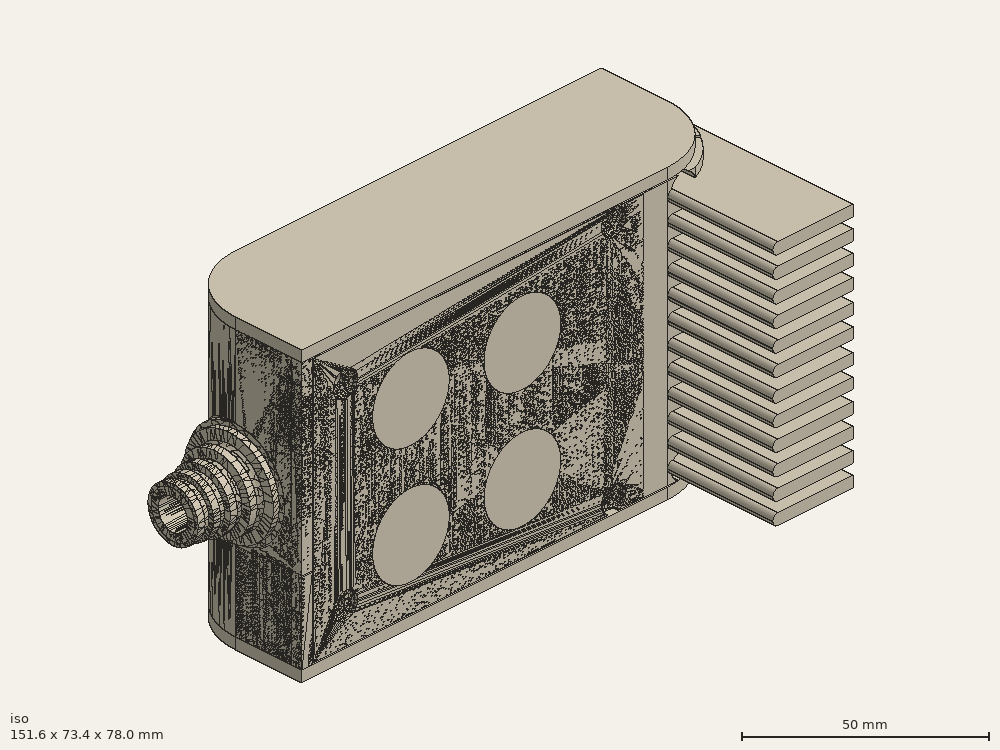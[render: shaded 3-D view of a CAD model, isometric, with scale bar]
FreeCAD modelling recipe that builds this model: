
FCSTD DOCUMENT  (FreeCAD 0.19R0.19.2)
Label: enclosure_1645FCStd
License: All rights reserved
LicenseURL: http://en.wikipedia.org/wiki/All_rights_reserved
objects: Part::Feature×140, Part::Revolution×140, Part::MultiFuse×124, Sketcher::SketchObject×70, Part::Extrusion×55, Part::Cut×53, Part::Cylinder×52, Part::Fillet×51, Part::Box×33, App::MeasureDistance×4
note: 718 computed .brp shape members not serialized (recipe doc carries the construction recipe); baked Part::Feature solids carry a one-line shape summary decoded from their .brp

FEATURE [Sketcher::SketchObject] Sketch  label="topSketch"
  FullyConstrained = true
  sketch-geometry (20):
    g0: LineSegment StartX=5.21097e-06 StartY=3 StartZ=0 EndX=5.21097e-06 EndY=19 EndZ=0
    g1: ArcOfCircle CenterX=19 CenterY=19 CenterZ=0 NormalX=0 NormalY=0 NormalZ=1 AngleXU=0 Radius=19 StartAngle=1.5708 EndAngle=3.14159
    g2: ArcOfCircle CenterX=19 CenterY=19 CenterZ=0 NormalX=0 NormalY=0 NormalZ=1 AngleXU=0 Radius=16 StartAngle=1.5708 EndAngle=3.14159
    g3: LineSegment StartX=114 StartY=35 StartZ=0 EndX=19 EndY=35 EndZ=0
    g4: LineSegment StartX=5.21097e-06 StartY=3 StartZ=0 EndX=5.21097e-06 EndY=0 EndZ=0
    g5: LineSegment StartX=3 StartY=0 StartZ=0 EndX=5.21097e-06 EndY=0 EndZ=0
    g6: LineSegment StartX=3 StartY=19 StartZ=0 EndX=3 EndY=0 EndZ=0
    g7: LineSegment StartX=19 StartY=38 StartZ=0 EndX=124 EndY=38 EndZ=0
    g8: Circle CenterX=119 CenterY=35 CenterZ=0 NormalX=0 NormalY=0 NormalZ=1 AngleXU=0 Radius=1
    g9: Circle CenterX=121 CenterY=35 CenterZ=0 NormalX=0 NormalY=0 NormalZ=1 AngleXU=0 Radius=1
    g10: Circle CenterX=121 CenterY=33 CenterZ=0 NormalX=0 NormalY=0 NormalZ=1 AngleXU=0 Radius=1
    g11: BSplineCurve PolesCount=3 KnotsCount=2 Degree=2 IsPeriodic=0
    g12: GeomPoint X=119 Y=35 Z=0
    g13: GeomPoint X=121 Y=33 Z=0
    g14: LineSegment StartX=119 StartY=35 StartZ=0 EndX=114 EndY=35 EndZ=0
    g15: ArcOfCircle CenterX=105 CenterY=19 CenterZ=0 NormalX=0 NormalY=0 NormalZ=1 AngleXU=0 Radius=19 StartAngle=5.7297 EndAngle=6.28319
    g16: ArcOfCircle CenterX=105 CenterY=19 CenterZ=0 NormalX=0 NormalY=0 NormalZ=1 AngleXU=0 Radius=16 StartAngle=5.60905 EndAngle=6.28319
    g17: LineSegment StartX=121 StartY=33 StartZ=0 EndX=121 EndY=19 EndZ=0
    g18: LineSegment StartX=124 StartY=38 StartZ=0 EndX=124 EndY=19 EndZ=0
    g19: LineSegment StartX=117.5 StartY=9.01251 StartZ=0 EndX=121.163 EndY=9.0125 EndZ=0
  constraints (46):
    c: Vertical(g0)
    c: Block(g0)
    c: Coincident(g1,g0)
    c: Block(g1)
    c: Coincident(g2,g1)
    c: Block(g2)
    c: Coincident(g3,g2)
    c: Horizontal(g3)
    c: Tangent(g3,g2)
    c: Coincident(g4,g0)
    c: Distance(g4) = 3
    c: Vertical(g4)
    c: Coincident(g5,g4)
    c: Horizontal(g5)
    c: Coincident(g6,g2)
    c: Coincident(g6,g5)
    c: Vertical(g6)
    c: Horizontal(g7)
    c: Distance(g7) = 105
    c: Coincident(g7,g1)
    c: Block(g3)
    c: Weight(g8) = 1
    c: Equal(g8,g9)
    c: Equal(g8,g10)
    c: InternalAlignment(g8,g11)
    c: InternalAlignment(g9,g11)
    c: InternalAlignment(g10,g11)
    c: InternalAlignment(g12,g11)
    c: InternalAlignment(g13,g11)
    c: Block(g11)
    c: Coincident(g14,g11)
    c: Coincident(g14,g3)
    c: Horizontal(g14)
    c: Block(g15)
    c: Coincident(g16,g15)
    c: Block(g16)
    c: Coincident(g17,g11)
    c: Coincident(g17,g16)
    c: Vertical(g17)
    c: Distance(g17) = 14
    c: Coincident(g18,g7)
    c: Coincident(g18,g15)
    c: Vertical(g18)
    c: Distance(g18) = 19
    c: Coincident(g19,g16)
    c: Coincident(g19,g15)
FEATURE [Sketcher::SketchObject] Sketch001  label="bottomSketch"
  FullyConstrained = true
  sketch-geometry (32):
    g0: LineSegment StartX=3.3 StartY=-6.03275e-07 StartZ=0 EndX=98 EndY=-6.03275e-07 EndZ=0
    g1: ArcOfCircle CenterX=98 CenterY=19 CenterZ=0 NormalX=0 NormalY=0 NormalZ=1 AngleXU=0 Radius=19 StartAngle=4.71239 EndAngle=5.71103
    g2: LineSegment StartX=6.3 StartY=8 StartZ=0 EndX=3.3 EndY=8 EndZ=0
    g3: LineSegment StartX=3.3 StartY=8 StartZ=0 EndX=3.3 EndY=-6.03275e-07 EndZ=0
    g4: ArcOfCircle CenterX=8.3 CenterY=5 CenterZ=0 NormalX=0 NormalY=0 NormalZ=1 AngleXU=0 Radius=2 StartAngle=3.14159 EndAngle=4.71239
    g5: LineSegment StartX=6.3 StartY=8 StartZ=0 EndX=6.3 EndY=5 EndZ=0
    g6: ArcOfCircle CenterX=98 CenterY=19 CenterZ=0 NormalX=0 NormalY=0 NormalZ=1 AngleXU=0 Radius=12.7 StartAngle=4.71239 EndAngle=6.28319
    g7: LineSegment StartX=94.7 StartY=3 StartZ=0 EndX=8.3 EndY=3 EndZ=0
    g8-g12: Circle x5 (B-spline internal-alignment scaffolding for g13; pole/knot coordinates omitted)
    g13: BSplineCurve PolesCount=5 KnotsCount=3 Degree=3 IsPeriodic=0
    g14: GeomPoint X=98 Y=6.3 Z=0
    g15: GeomPoint X=96.3938 Y=4.71946 Z=0
    g16: GeomPoint X=94.7 Y=3 Z=0
    g17-g23: Circle x7 (B-spline internal-alignment scaffolding for g24; pole/knot coordinates omitted)
    g24: BSplineCurve PolesCount=7 KnotsCount=5 Degree=3 IsPeriodic=0
    g25-g29: GeomPoint x5 (B-spline internal-alignment scaffolding for g24; pole/knot coordinates omitted)
    g30: ArcOfCircle CenterX=98 CenterY=19 CenterZ=0 NormalX=0 NormalY=0 NormalZ=1 AngleXU=0 Radius=15.7 StartAngle=5.81226 EndAngle=6.28319
    g31: LineSegment StartX=110.7 StartY=19 StartZ=0 EndX=113.7 EndY=19 EndZ=0
  constraints (41):
    c: Horizontal(g0)
    c: Coincident(g1,g0)
    c: Block(g1)
    c: Horizontal(g2)
    c: Distance(g2) = 3
    c: Coincident(g3,g2)
    c: Vertical(g3)
    c: Coincident(g3,g0)
    c: Block(g4)
    c: Block(g2)
    c: Coincident(g5,g2)
    c: Coincident(g5,g4)
    c: Vertical(g5)
    c: Coincident(g6,g1)
    c: Block(g6)
    c: Coincident(g7,g4)
    c: Horizontal(g7)
    c: Block(g0)
    c: Block(g7)
    c: Block(g3)
    c: Coincident(g13,g6)
    c: Weight(g8) = 1
    c: Equal(g8, g9-g12) x4
    c: Coincident(g13,g7)
    c: InternalAlignment(g8-g12 -> g13) x5
    c: InternalAlignment(g14,g13)
    c: InternalAlignment(g15,g13)
    c: InternalAlignment(g16,g13)
    c: Block(g13)
    c: Weight(g17) = 1
    c: Equal(g17, g18-g23) x6
    c: Coincident(g24,g1)
    c: InternalAlignment(g17-g23 -> g24) x7
    c: InternalAlignment(g25-g29 -> g24) x5
    c: Block(g24)
    c: Coincident(g30,g24)
    c: Coincident(g31,g6)
    c: Coincident(g31,g30)
    c: Horizontal(g31)
    c: Block(g31)
    c: Block(g30)
FEATURE [Part::Extrusion] Extrude  label="top"
  Base = -> Sketch
  Dir = (0,0,1)
  DirMode = 2
  FaceMakerClass = Part::FaceMakerBullseye
  LengthFwd = 72
  LengthRev = 0
  Solid = true
  Symmetric = false
FEATURE [Part::Extrusion] Extrude001  label="bottom"
  Base = -> Sketch001
  Dir = (0,0,1)
  DirMode = 2
  FaceMakerClass = Part::FaceMakerBullseye
  LengthFwd = 71.4
  LengthRev = 0
  Placement = pos=(0,0,0.3) rot=(0,0,1;0rad)
  Solid = true
  Symmetric = false
FEATURE [Sketcher::SketchObject] Sketch002  label="topSketch001"
  FullyConstrained = true
  sketch-geometry (6):
    g0: ArcOfCircle CenterX=19 CenterY=19 CenterZ=0 NormalX=0 NormalY=0 NormalZ=1 AngleXU=0 Radius=19 StartAngle=1.5708 EndAngle=3.14159
    g1: LineSegment StartX=5.22862e-06 StartY=19 StartZ=0 EndX=5.22862e-06 EndY=1.19904e-11 EndZ=0
    g2: LineSegment StartX=19 StartY=38 StartZ=0 EndX=124 EndY=38 EndZ=0
    g3: LineSegment StartX=5.22862e-06 StartY=1.19904e-11 StartZ=0 EndX=105 EndY=1.19904e-11 EndZ=0
    g4: ArcOfCircle CenterX=105 CenterY=19 CenterZ=0 NormalX=0 NormalY=0 NormalZ=1 AngleXU=0 Radius=19 StartAngle=4.71239 EndAngle=6.28319
    g5: LineSegment StartX=124 StartY=38 StartZ=0 EndX=124 EndY=19 EndZ=0
  constraints (16):
    c: Block(g0)
    c: Coincident(g1,g0)
    c: Vertical(g1)
    c: Horizontal(g2)
    c: Distance(g2) = 105
    c: Coincident(g2,g0)
    c: Distance(g1) = 19
    c: Coincident(g3,g1)
    c: Horizontal(g3)
    c: Distance(g3) = 105
    c: Block(g4)
    c: Coincident(g4,g3)
    c: Coincident(g5,g2)
    c: Coincident(g5,g4)
    c: Vertical(g5)
    c: Distance(g5) = 19
FEATURE [Part::Extrusion] Extrude002  label="sideA"
  Base = -> Sketch002
  Dir = (0,0,1)
  DirMode = 2
  FaceMakerClass = Part::FaceMakerBullseye
  LengthFwd = 3
  LengthRev = 0
  Placement = pos=(0,0,-3) rot=(0,0,1;0rad)
  Solid = true
  Symmetric = false
FEATURE [Sketcher::SketchObject] Sketch003  label="topSketch002"
  FullyConstrained = true
  sketch-geometry (6):
    g0: LineSegment StartX=19 StartY=38 StartZ=0 EndX=117 EndY=38 EndZ=0
    g1: ArcOfCircle CenterX=19 CenterY=19 CenterZ=0 NormalX=0 NormalY=0 NormalZ=1 AngleXU=0 Radius=19 StartAngle=1.5708 EndAngle=3.14159
    g2: LineSegment StartX=117 StartY=38 StartZ=0 EndX=117 EndY=19 EndZ=0
    g3: LineSegment StartX=98 StartY=1.0161e-12 StartZ=0 EndX=5.22862e-06 EndY=1.0161e-12 EndZ=0
    g4: LineSegment StartX=5.22862e-06 StartY=19 StartZ=0 EndX=5.22862e-06 EndY=1.0161e-12 EndZ=0
    g5: ArcOfCircle CenterX=98 CenterY=19 CenterZ=0 NormalX=0 NormalY=0 NormalZ=1 AngleXU=0 Radius=19 StartAngle=4.71239 EndAngle=6.28319
  constraints (16):
    c: Horizontal(g0)
    c: Distance(g0) = 98
    c: Coincident(g1,g0)
    c: Block(g1)
    c: Coincident(g2,g0)
    c: Vertical(g2)
    c: Distance(g2) = 19
    c: Horizontal(g3)
    c: Coincident(g4,g1)
    c: Vertical(g4)
    c: Coincident(g3,g4)
    c: Block(g3)
    c: Coincident(g5,g2)
    c: Coincident(g5,g3)
    c: Block(g0)
    c: Block(g5)
FEATURE [Sketcher::SketchObject] Sketch004
  FullyConstrained = true
  MapMode = 3
  Placement = pos=(0,0,0) rot=(1,0,0;1.5708rad)
  Support = -> [Extrude]
  sketch-geometry (8):
    g0: Circle CenterX=80.351 CenterY=-67.6202 CenterZ=0 NormalX=0 NormalY=0 NormalZ=1 AngleXU=0 Radius=2
    g1: Circle CenterX=80.351 CenterY=-67.6202 CenterZ=0 NormalX=0 NormalY=0 NormalZ=1 AngleXU=0 Radius=3
    g2: Circle CenterX=80.351 CenterY=-4.92017 CenterZ=0 NormalX=0 NormalY=0 NormalZ=1 AngleXU=0 Radius=2
    g3: Circle CenterX=80.351 CenterY=-4.92017 CenterZ=0 NormalX=0 NormalY=0 NormalZ=1 AngleXU=0 Radius=3
    g4: Circle CenterX=23.851 CenterY=-4.92017 CenterZ=0 NormalX=0 NormalY=0 NormalZ=1 AngleXU=0 Radius=2
    g5: Circle CenterX=23.851 CenterY=-4.92017 CenterZ=0 NormalX=0 NormalY=0 NormalZ=1 AngleXU=0 Radius=3
    g6: Circle CenterX=23.851 CenterY=-67.6202 CenterZ=0 NormalX=0 NormalY=0 NormalZ=1 AngleXU=0 Radius=2
    g7: Circle CenterX=23.851 CenterY=-67.6202 CenterZ=0 NormalX=0 NormalY=0 NormalZ=1 AngleXU=0 Radius=3
  constraints (8):
    c: Block(g3)
    c: Block(g2)
    c: Block(g1)
    c: Block(g0)
    c: Block(g6)
    c: Block(g7)
    c: Block(g4)
    c: Block(g5)
FEATURE [Part::Extrusion] Extrude004
  Base = -> Sketch004
  Dir = (0,-1,2e-16)
  DirMode = 2
  FaceMakerClass = Part::FaceMakerBullseye
  LengthFwd = 6
  LengthRev = 0
  Placement = pos=(0,9,0) rot=(0,0,1;0rad)
  Solid = true
  Symmetric = false
FEATURE [Sketcher::SketchObject] Sketch005
  FullyConstrained = true
  MapMode = 3
  Placement = pos=(0,0,0) rot=(1,0,0;1.5708rad)
  Support = -> [Extrude]
  sketch-geometry (8):
    g0: Circle CenterX=80.351 CenterY=-67.6202 CenterZ=0 NormalX=0 NormalY=0 NormalZ=1 AngleXU=0 Radius=3
    g1: Circle CenterX=80.351 CenterY=-4.92017 CenterZ=0 NormalX=0 NormalY=0 NormalZ=1 AngleXU=0 Radius=3
    g2: Circle CenterX=23.851 CenterY=-4.92017 CenterZ=0 NormalX=0 NormalY=0 NormalZ=1 AngleXU=0 Radius=3
    g3: Circle CenterX=23.851 CenterY=-67.6202 CenterZ=0 NormalX=0 NormalY=0 NormalZ=1 AngleXU=0 Radius=3
    g4: Circle CenterX=23.851 CenterY=-67.6202 CenterZ=0 NormalX=0 NormalY=0 NormalZ=1 AngleXU=0 Radius=5
    g5: Circle CenterX=80.351 CenterY=-67.6202 CenterZ=0 NormalX=0 NormalY=0 NormalZ=1 AngleXU=0 Radius=5
    g6: Circle CenterX=23.851 CenterY=-4.92017 CenterZ=0 NormalX=0 NormalY=0 NormalZ=1 AngleXU=0 Radius=5
    g7: Circle CenterX=80.351 CenterY=-4.92017 CenterZ=0 NormalX=0 NormalY=0 NormalZ=1 AngleXU=0 Radius=5
  constraints (8):
    c: Block(g1)
    c: Block(g0)
    c: Block(g3)
    c: Block(g2)
    c: Block(g5)
    c: Block(g4)
    c: Block(g6)
    c: Block(g7)
FEATURE [Part::Extrusion] Extrude005
  Base = -> Sketch005
  Dir = (0,-1,2e-16)
  DirMode = 2
  FaceMakerClass = Part::FaceMakerBullseye
  LengthFwd = 2
  LengthRev = 0
  Solid = true
  Symmetric = false
FEATURE [Sketcher::SketchObject] Sketch006
  FullyConstrained = true
  MapMode = 3
  Placement = pos=(0,0,0) rot=(1,0,0;1.5708rad)
  sketch-geometry (8):
    g0: Circle CenterX=80.351 CenterY=-67.6202 CenterZ=0 NormalX=0 NormalY=0 NormalZ=1 AngleXU=0 Radius=3
    g1: Circle CenterX=80.351 CenterY=-4.92017 CenterZ=0 NormalX=0 NormalY=0 NormalZ=1 AngleXU=0 Radius=3
    g2: Circle CenterX=23.851 CenterY=-4.92017 CenterZ=0 NormalX=0 NormalY=0 NormalZ=1 AngleXU=0 Radius=3
    g3: Circle CenterX=23.851 CenterY=-67.6202 CenterZ=0 NormalX=0 NormalY=0 NormalZ=1 AngleXU=0 Radius=3
    g4: Circle CenterX=23.851 CenterY=-67.6202 CenterZ=0 NormalX=0 NormalY=0 NormalZ=1 AngleXU=0 Radius=5
    g5: Circle CenterX=80.351 CenterY=-67.6202 CenterZ=0 NormalX=0 NormalY=0 NormalZ=1 AngleXU=0 Radius=5
    g6: Circle CenterX=23.851 CenterY=-4.92017 CenterZ=0 NormalX=0 NormalY=0 NormalZ=1 AngleXU=0 Radius=5
    g7: Circle CenterX=80.351 CenterY=-4.92017 CenterZ=0 NormalX=0 NormalY=0 NormalZ=1 AngleXU=0 Radius=5
  constraints (8):
    c: Block(g1)
    c: Block(g0)
    c: Block(g3)
    c: Block(g2)
    c: Block(g5)
    c: Block(g4)
    c: Block(g6)
    c: Block(g7)
FEATURE [Part::Extrusion] Extrude007
  Base = -> Sketch006
  Dir = (0,-1,2e-16)
  DirMode = 2
  FaceMakerClass = Part::FaceMakerBullseye
  LengthFwd = 2
  LengthRev = 0
  Solid = true
  Symmetric = false
FEATURE [Part::Fillet] Fillet
  Base = -> Extrude007
  Edges = 4 edges r=1.99: [Edge6,Edge12,Edge18,Edge24]
FEATURE [Part::Cut] Cut
  Base = -> Extrude005
  Placement = pos=(0,5,0) rot=(0,0,1;0rad)
  Tool = -> Fillet
FEATURE [Part::MultiFuse] Fusion  label="pCBScrews"
  Placement = pos=(-2.5,0,72.3) rot=(0,0,1;0rad)
  Shapes = -> [Extrude004,Cut]
FEATURE [App::MeasureDistance] Distance  label="Distance: 0.69 mm"
  Distance = 0.685967
  P1 = (24.0138,2.9647,0.3)
  P2 = (23.8901,3,-0.373787)
FEATURE [App::MeasureDistance] Distance001  label="Distance: 0.53 mm"
  Distance = 0.533607
  P1 = (80.2939,3,72.2334)
  P2 = (80.281,2.99661,71.7)
FEATURE [Part::Fillet] Fillet001
  Base = -> Extrude001
  Edges = 1 edges r=2.4: [Edge17]
FEATURE [Part::Fillet] Fillet002  label="bottom001"
  Base = -> Fillet001
  Edges = 1 edges r=2.4: [Edge36]
FEATURE [Part::Fillet] Fillet003  label="top001"
  Base = -> Extrude
  Edges = 1 edges r=2: [Edge1]
FEATURE [Sketcher::SketchObject] Sketch007
  FullyConstrained = true
  sketch-geometry (16):
    g0: LineSegment StartX=4 StartY=0 StartZ=0 EndX=4 EndY=2.4 EndZ=0
    g1: LineSegment StartX=4 StartY=2.4 StartZ=0 EndX=7 EndY=2.4 EndZ=0
    g2: LineSegment StartX=4 StartY=0 StartZ=0 EndX=5.7 EndY=0 EndZ=0
    g3: LineSegment StartX=5.7 StartY=0 StartZ=0 EndX=5.7 EndY=-5.6 EndZ=0
    g4-g8: Circle x5 (B-spline internal-alignment scaffolding for g9; pole/knot coordinates omitted)
    g9: BSplineCurve PolesCount=5 KnotsCount=3 Degree=3 IsPeriodic=0
    g10: GeomPoint X=7 Y=2.4 Z=0
    g11: GeomPoint X=10.4582 Y=-1.55472 Z=0
    g12: GeomPoint X=14 Y=-5.6 Z=0
    g13: LineSegment StartX=14 StartY=-5.6 StartZ=0 EndX=14 EndY=-14.1 EndZ=0
    g14: LineSegment StartX=14 StartY=-14.1 StartZ=0 EndX=6.5 EndY=-14.1 EndZ=0
    g15: LineSegment StartX=5.7 StartY=-5.6 StartZ=0 EndX=6.5 EndY=-14.1 EndZ=0
  constraints (28):
    c: Distance(g0) = 2.4
    c: Vertical(g0)
    c: Block(g0)
    c: Coincident(g1,g0)
    c: Horizontal(g1)
    c: Distance(g1) = 3
    c: Coincident(g2,g0)
    c: Horizontal(g2)
    c: Distance(g2) = 1.7
    c: Coincident(g3,g2)
    c: Vertical(g3)
    c: Distance(g3) = 5.6
    c: Coincident(g9,g1)
    c: Weight(g4) = 1
    c: Equal(g4, g5-g8) x4
    c: InternalAlignment(g4-g8 -> g9) x5
    c: InternalAlignment(g10,g9)
    c: InternalAlignment(g11,g9)
    c: InternalAlignment(g12,g9)
    c: Block(g9)
    c: Coincident(g13,g9)
    c: Vertical(g13)
    c: Distance(g13) = 8.5
    c: Coincident(g14,g13)
    c: Horizontal(g14)
    c: Distance(g14) = 7.5
    c: Coincident(g15,g3)
    c: Coincident(g15,g14)
FEATURE [Part::Feature] Face
  shape: bbox 10 x 16.5 x 2e-07 mm, 1 faces, 0 solids (baked)
FEATURE [Part::Revolution] Revolve  label="plugHousing"
  Angle = 360
  Axis = (0,1,0)
  Base = (0,0,0)
  FaceMakerClass = Part::FaceMakerBullseye
  Placement = pos=(0,0,36.15) rot=(0,0,1;0rad)
  Solid = false
  Source = -> Face
  Symmetric = false
FEATURE [Part::Feature] Face001
  shape: bbox 10 x 16.5 x 2e-07 mm, 1 faces, 0 solids (baked)
FEATURE [Part::Revolution] Revolve001  label="plugHousing001"
  Angle = 360
  Axis = (0,1,0)
  Base = (0,0,0)
  FaceMakerClass = Part::FaceMakerBullseye
  Placement = pos=(0,0,36.15) rot=(0,0,1;0rad)
  Solid = false
  Source = -> Face001
  Symmetric = false
FEATURE [Part::MultiFuse] Fusion001  label="plugHousing002"
  Placement = pos=(0,0,0) rot=(0,0,1;1.5708rad)
  Shapes = -> [Revolve001,Revolve]
FEATURE [Part::Feature] Face002
  shape: bbox 10 x 16.5 x 2e-07 mm, 1 faces, 0 solids (baked)
FEATURE [Part::Revolution] Revolve003  label="plugHousing005"
  Angle = 360
  Axis = (0,1,0)
  Base = (0,0,0)
  FaceMakerClass = Part::FaceMakerBullseye
  Placement = pos=(0,0,36.15) rot=(0,0,1;0rad)
  Solid = false
  Source = -> Face002
  Symmetric = false
FEATURE [Part::Feature] Face003
  shape: bbox 10 x 16.5 x 2e-07 mm, 1 faces, 0 solids (baked)
FEATURE [Part::Revolution] Revolve002  label="plugHousing003"
  Angle = 360
  Axis = (0,1,0)
  Base = (0,0,0)
  FaceMakerClass = Part::FaceMakerBullseye
  Placement = pos=(0,0,36.15) rot=(0,0,1;0rad)
  Solid = false
  Source = -> Face003
  Symmetric = false
FEATURE [Part::MultiFuse] Fusion002  label="plugHousing004"
  Placement = pos=(0,0,0) rot=(0,0,1;1.5708rad)
  Shapes = -> [Revolve002,Revolve003]
FEATURE [Part::MultiFuse] Fusion003  label="plugHousing006"
  Placement = pos=(0,19,0) rot=(0,0,1;3.14159rad)
  Shapes = -> [Fusion002,Fusion001]
FEATURE [Part::Feature] Face004
  shape: bbox 10 x 16.5 x 2e-07 mm, 1 faces, 0 solids (baked)
FEATURE [Part::Revolution] Revolve006  label="plugHousing010"
  Angle = 360
  Axis = (0,1,0)
  Base = (0,0,0)
  FaceMakerClass = Part::FaceMakerBullseye
  Placement = pos=(0,0,36.15) rot=(0,0,1;0rad)
  Solid = false
  Source = -> Face004
  Symmetric = false
FEATURE [Part::Feature] Face005
  shape: bbox 10 x 16.5 x 2e-07 mm, 1 faces, 0 solids (baked)
FEATURE [Part::Revolution] Revolve007  label="plugHousing011"
  Angle = 360
  Axis = (0,1,0)
  Base = (0,0,0)
  FaceMakerClass = Part::FaceMakerBullseye
  Placement = pos=(0,0,36.15) rot=(0,0,1;0rad)
  Solid = false
  Source = -> Face005
  Symmetric = false
FEATURE [Part::Feature] Face006
  shape: bbox 10 x 16.5 x 2e-07 mm, 1 faces, 0 solids (baked)
FEATURE [Part::Revolution] Revolve004  label="plugHousing007"
  Angle = 360
  Axis = (0,1,0)
  Base = (0,0,0)
  FaceMakerClass = Part::FaceMakerBullseye
  Placement = pos=(0,0,36.15) rot=(0,0,1;0rad)
  Solid = false
  Source = -> Face006
  Symmetric = false
FEATURE [Part::MultiFuse] Fusion004  label="plugHousing009"
  Placement = pos=(0,0,0) rot=(0,0,1;1.5708rad)
  Shapes = -> [Revolve004,Revolve007]
FEATURE [Part::Feature] Face007
  shape: bbox 10 x 16.5 x 2e-07 mm, 1 faces, 0 solids (baked)
FEATURE [Part::Revolution] Revolve005  label="plugHousing008"
  Angle = 360
  Axis = (0,1,0)
  Base = (0,0,0)
  FaceMakerClass = Part::FaceMakerBullseye
  Placement = pos=(0,0,36.15) rot=(0,0,1;0rad)
  Solid = false
  Source = -> Face007
  Symmetric = false
FEATURE [Part::MultiFuse] Fusion005  label="plugHousing012"
  Placement = pos=(0,0,0) rot=(0,0,1;1.5708rad)
  Shapes = -> [Revolve006,Revolve005]
FEATURE [Part::MultiFuse] Fusion006  label="plugHousing013"
  Placement = pos=(0,19,0) rot=(0,0,1;3.14159rad)
  Shapes = -> [Fusion005,Fusion004]
FEATURE [Part::MultiFuse] Fusion007  label="plugHousing014"
  Placement = pos=(122.621,0,-0.15) rot=(0,0,1;0rad)
  Shapes = -> [Fusion003,Fusion006]
FEATURE [Part::Cylinder] Cylinder002
  Angle = 360
  AttacherType = Attacher::AttachEngine3D
  Height = 20
  Placement = pos=(0,0,36.15) rot=(0,0,1;0rad)
  Radius = 4
FEATURE [Part::Cylinder] Cylinder003
  Angle = 360
  AttacherType = Attacher::AttachEngine3D
  Height = 10
  Placement = pos=(0,0,36.15) rot=(0,0,1;0rad)
  Radius = 4
FEATURE [Part::MultiFuse] Fusion009  label="removeToCreateHoleForPlugHousing"
  Placement = pos=(70,19,36.15) rot=(0,1,0;1.5708rad)
  Shapes = -> [Cylinder002,Cylinder003]
FEATURE [Part::Cylinder] Cylinder004
  Angle = 360
  AttacherType = Attacher::AttachEngine3D
  Height = 20
  Placement = pos=(0,0,36.15) rot=(0,0,1;0rad)
  Radius = 4
FEATURE [Part::Cylinder] Cylinder005
  Angle = 360
  AttacherType = Attacher::AttachEngine3D
  Height = 10
  Placement = pos=(0,0,36.15) rot=(0,0,1;0rad)
  Radius = 4
FEATURE [Part::MultiFuse] Fusion010  label="removeToCreateHoleForPlugHousing001"
  Placement = pos=(70,19,36.15) rot=(0,1,0;1.5708rad)
  Shapes = -> [Cylinder004,Cylinder005]
FEATURE [Part::Cut] Cut001
  Base = -> Fillet003
  Tool = -> Fusion010
FEATURE [Part::Cut] Cut002  label="Bottom"
  Base = -> Fillet002
  Tool = -> Fusion009
FEATURE [Part::Feature] Face008
  shape: bbox 10 x 16.5 x 2e-07 mm, 1 faces, 0 solids (baked)
FEATURE [Part::Revolution] Revolve011  label="plugHousing021"
  Angle = 360
  Axis = (0,1,0)
  Base = (0,0,0)
  FaceMakerClass = Part::FaceMakerBullseye
  Placement = pos=(0,0,36.15) rot=(0,0,1;0rad)
  Solid = false
  Source = -> Face008
  Symmetric = false
FEATURE [Part::Feature] Face009
  shape: bbox 10 x 16.5 x 2e-07 mm, 1 faces, 0 solids (baked)
FEATURE [Part::Revolution] Revolve012  label="plugHousing022"
  Angle = 360
  Axis = (0,1,0)
  Base = (0,0,0)
  FaceMakerClass = Part::FaceMakerBullseye
  Placement = pos=(0,0,36.15) rot=(0,0,1;0rad)
  Solid = false
  Source = -> Face009
  Symmetric = false
FEATURE [Part::Feature] Face010 .. Face013  x4 (patterned run collapsed; names and placements below)
  shape: bbox 10 x 16.5 x 2e-07 mm, 1 faces, 0 solids (baked)
FEATURE [Part::Revolution] Revolve015  label="plugHousing027"
  Angle = 360
  Axis = (0,1,0)
  Base = (0,0,0)
  FaceMakerClass = Part::FaceMakerBullseye
  Placement = pos=(0,0,36.15) rot=(0,0,1;0rad)
  Solid = false
  Source = -> Face013
  Symmetric = false
FEATURE [Part::Feature] Face014
  shape: bbox 10 x 16.5 x 2e-07 mm, 1 faces, 0 solids (baked)
FEATURE [Part::Feature] Face015
  shape: bbox 10 x 16.5 x 2e-07 mm, 1 faces, 0 solids (baked)
FEATURE [Part::Feature] Face016
  shape: bbox 10 x 16.5 x 2e-07 mm, 1 faces, 0 solids (baked)
FEATURE [Part::Revolution] Revolve019  label="plugHousing033"
  Angle = 360
  Axis = (0,1,0)
  Base = (0,0,0)
  FaceMakerClass = Part::FaceMakerBullseye
  Placement = pos=(0,0,36.15) rot=(0,0,1;0rad)
  Solid = false
  Source = -> Face016
  Symmetric = false
FEATURE [Part::Feature] Face017
  shape: bbox 10 x 16.5 x 2e-07 mm, 1 faces, 0 solids (baked)
FEATURE [Part::Revolution] Revolve020  label="plugHousing034"
  Angle = 360
  Axis = (0,1,0)
  Base = (0,0,0)
  FaceMakerClass = Part::FaceMakerBullseye
  Placement = pos=(0,0,36.15) rot=(0,0,1;0rad)
  Solid = false
  Source = -> Face017
  Symmetric = false
FEATURE [Part::Feature] Face018
  shape: bbox 10 x 16.5 x 2e-07 mm, 1 faces, 0 solids (baked)
FEATURE [Part::Revolution] Revolve016  label="plugHousing030"
  Angle = 360
  Axis = (0,1,0)
  Base = (0,0,0)
  FaceMakerClass = Part::FaceMakerBullseye
  Placement = pos=(0,0,36.15) rot=(0,0,1;0rad)
  Solid = false
  Source = -> Face018
  Symmetric = false
FEATURE [Part::MultiFuse] Fusion020  label="plugHousing038"
  Placement = pos=(0,0,0) rot=(0,0,1;1.5708rad)
  Shapes = -> [Revolve016,Revolve020]
FEATURE [Part::Feature] Face019
  shape: bbox 10 x 16.5 x 2e-07 mm, 1 faces, 0 solids (baked)
FEATURE [Part::Feature] Face020
  shape: bbox 10 x 16.5 x 2e-07 mm, 1 faces, 0 solids (baked)
FEATURE [Part::Revolution] Revolve017  label="plugHousing031"
  Angle = 360
  Axis = (0,1,0)
  Base = (0,0,0)
  FaceMakerClass = Part::FaceMakerBullseye
  Placement = pos=(0,0,36.15) rot=(0,0,1;0rad)
  Solid = false
  Source = -> Face020
  Symmetric = false
FEATURE [Part::MultiFuse] Fusion021  label="plugHousing039"
  Placement = pos=(0,0,0) rot=(0,0,1;1.5708rad)
  Shapes = -> [Revolve019,Revolve017]
FEATURE [Part::MultiFuse] Fusion023  label="plugHousing041"
  Placement = pos=(0,19,0) rot=(0,0,1;3.14159rad)
  Shapes = -> [Fusion021,Fusion020]
FEATURE [Part::Revolution] Revolve022  label="plugHousing043"
  Angle = 360
  Axis = (0,1,0)
  Base = (0,0,0)
  FaceMakerClass = Part::FaceMakerBullseye
  Placement = pos=(0,0,36.15) rot=(0,0,1;0rad)
  Solid = false
  Source = -> Face019
  Symmetric = false
FEATURE [Part::Feature] Face021
  shape: bbox 10 x 16.5 x 2e-07 mm, 1 faces, 0 solids (baked)
FEATURE [Part::Revolution] Revolve023  label="plugHousing044"
  Angle = 360
  Axis = (0,1,0)
  Base = (0,0,0)
  FaceMakerClass = Part::FaceMakerBullseye
  Placement = pos=(0,0,36.15) rot=(0,0,1;0rad)
  Solid = false
  Source = -> Face021
  Symmetric = false
FEATURE [Part::Feature] Face022
  shape: bbox 10 x 16.5 x 2e-07 mm, 1 faces, 0 solids (baked)
FEATURE [Part::Revolution] Revolve018  label="plugHousing032"
  Angle = 360
  Axis = (0,1,0)
  Base = (0,0,0)
  FaceMakerClass = Part::FaceMakerBullseye
  Placement = pos=(0,0,36.15) rot=(0,0,1;0rad)
  Solid = false
  Source = -> Face022
  Symmetric = false
FEATURE [Part::MultiFuse] Fusion022  label="plugHousing040"
  Placement = pos=(0,0,0) rot=(0,0,1;1.5708rad)
  Shapes = -> [Revolve018,Revolve023]
FEATURE [Part::Feature] Face023
  shape: bbox 10 x 16.5 x 2e-07 mm, 1 faces, 0 solids (baked)
FEATURE [Part::Revolution] Revolve021  label="plugHousing035"
  Angle = 360
  Axis = (0,1,0)
  Base = (0,0,0)
  FaceMakerClass = Part::FaceMakerBullseye
  Placement = pos=(0,0,36.15) rot=(0,0,1;0rad)
  Solid = false
  Source = -> Face023
  Symmetric = false
FEATURE [Part::MultiFuse] Fusion018  label="plugHousing036"
  Placement = pos=(0,0,0) rot=(0,0,1;1.5708rad)
  Shapes = -> [Revolve022,Revolve021]
FEATURE [Part::MultiFuse] Fusion019  label="plugHousing037"
  Placement = pos=(0,19,0) rot=(0,0,1;3.14159rad)
  Shapes = -> [Fusion018,Fusion022]
FEATURE [Part::MultiFuse] Fusion024  label="plugHousing042"
  Placement = pos=(122.621,0,-0.15) rot=(0,0,1;0rad)
  Shapes = -> [Fusion023,Fusion019]
FEATURE [Part::Cylinder] Cylinder006
  Angle = 360
  AttacherType = Attacher::AttachEngine3D
  Height = 20
  Placement = pos=(0,0,36.15) rot=(0,0,1;0rad)
  Radius = 14.3
FEATURE [Part::Cylinder] Cylinder007
  Angle = 360
  AttacherType = Attacher::AttachEngine3D
  Height = 10
  Placement = pos=(0,0,36.15) rot=(0,0,1;0rad)
  Radius = 4
FEATURE [Part::MultiFuse] Fusion026  label="removeToCreteHoleForPlugHousing"
  Placement = pos=(70,19,36) rot=(0,1,0;1.5708rad)
  Shapes = -> [Cylinder006,Cylinder007]
FEATURE [Part::Box] Box001  label="Cube001"
  AttacherType = Attacher::AttachEngine3D
  Height = 28
  Length = 3
  Placement = pos=(110.7,19,22) rot=(0,0,1;0rad)
  Width = 15.7
FEATURE [Part::Cut] Cut003  label="top002"
  Base = -> Cut001
  Tool = -> Fusion007
FEATURE [Part::Revolution] Revolve008  label="plugHousing015"
  Angle = 360
  Axis = (0,1,0)
  Base = (0,0,0)
  FaceMakerClass = Part::FaceMakerBullseye
  Placement = pos=(0,0,36.15) rot=(0,0,1;0rad)
  Solid = false
  Source = -> Face010
  Symmetric = false
FEATURE [Part::MultiFuse] Fusion013  label="plugHousing020"
  Placement = pos=(0,0,0) rot=(0,0,1;1.5708rad)
  Shapes = -> [Revolve008,Revolve012]
FEATURE [Part::Cut] Cut004  label="top003"
  Base = -> Cut003
  Placement = pos=(1,0,0) rot=(0,0,1;0rad)
  Tool = -> Fusion026
FEATURE [Part::Cylinder] Cylinder008
  Angle = 360
  AttacherType = Attacher::AttachEngine3D
  Height = 20
  Placement = pos=(0,0,36.15) rot=(0,0,1;0rad)
  Radius = 10.3
FEATURE [Part::Cylinder] Cylinder009
  Angle = 360
  AttacherType = Attacher::AttachEngine3D
  Height = 10
  Placement = pos=(0,0,36.15) rot=(0,0,1;0rad)
  Radius = 4
FEATURE [Part::MultiFuse] Fusion027  label="removeToCreteHoleForPlugHousing001"
  Placement = pos=(70,19,36) rot=(0,1,0;1.5708rad)
  Shapes = -> [Cylinder008,Cylinder009]
FEATURE [Part::Cut] Cut005  label="plugHousingTab"
  Base = -> Box001
  Tool = -> Fusion027
FEATURE [Part::MultiFuse] Fusion028  label="plugHousing045"
  Shapes = -> [Fusion024,Cut005]
FEATURE [Part::Box] Box002  label="Cube002"
  AttacherType = Attacher::AttachEngine3D
  Height = 28.8
  Length = 3
  Placement = pos=(107.3,28,21.6) rot=(0,0,1;0rad)
  Width = 7
FEATURE [Part::Box] Box003  label="Cube003"
  AttacherType = Attacher::AttachEngine3D
  Height = 3
  Length = 6.4
  Placement = pos=(107.3,28,18.6) rot=(0,0,1;0rad)
  Width = 7
FEATURE [Part::Box] Box004  label="Cube004"
  AttacherType = Attacher::AttachEngine3D
  Height = 3
  Length = 6.4
  Placement = pos=(107.3,28,50.4) rot=(0,0,1;0rad)
  Width = 7
FEATURE [Part::MultiFuse] Fusion029  label="plugHousingBracketHolder"
  Shapes = -> [Box004,Box002,Box003]
FEATURE [Part::Cylinder] Cylinder010
  Angle = 360
  AttacherType = Attacher::AttachEngine3D
  Height = 20
  Placement = pos=(0,0,36.15) rot=(0,0,1;0rad)
  Radius = 14.3
FEATURE [Part::Cylinder] Cylinder011
  Angle = 360
  AttacherType = Attacher::AttachEngine3D
  Height = 10
  Placement = pos=(0,0,36.15) rot=(0,0,1;0rad)
  Radius = 4
FEATURE [Part::MultiFuse] Fusion030  label="removeToCreteHoleForPlugHousing002"
  Placement = pos=(70,19,36) rot=(0,1,0;1.5708rad)
  Shapes = -> [Cylinder010,Cylinder011]
FEATURE [Part::Cut] Cut006  label="plugHousingBracketHolder001"
  Base = -> Fusion029
  Tool = -> Fusion030
FEATURE [Part::Cylinder] Cylinder012
  Angle = 360
  AttacherType = Attacher::AttachEngine3D
  Height = 20
  Placement = pos=(0,0,36.15) rot=(0,0,1;0rad)
  Radius = 7
FEATURE [Part::Cylinder] Cylinder013
  Angle = 360
  AttacherType = Attacher::AttachEngine3D
  Height = 10
  Placement = pos=(0,0,36.15) rot=(0,0,1;0rad)
  Radius = 4
FEATURE [Part::MultiFuse] Fusion032  label="removeToCreteHoleForPlugHousing003"
  Placement = pos=(70,19,36) rot=(0,1,0;1.5708rad)
  Shapes = -> [Cylinder012,Cylinder013]
FEATURE [Part::Cut] Cut007  label="bottom002"
  Base = -> Cut002
  Tool = -> Fusion032
FEATURE [Sketcher::SketchObject] Sketch008
  FullyConstrained = true
  sketch-geometry (54):
    g0: LineSegment StartX=-4.2 StartY=0 StartZ=0 EndX=-6.2 EndY=0 EndZ=0
    g1: LineSegment StartX=-14 StartY=-18 StartZ=0 EndX=-14 EndY=-26.5 EndZ=0
    g2: LineSegment StartX=-4.2 StartY=0 StartZ=0 EndX=-4.2 EndY=-13.4877 EndZ=0
    g3: Circle CenterX=-4.2 CenterY=-13.4877 CenterZ=0 NormalX=0 NormalY=0 NormalZ=1 AngleXU=0 Radius=1
    g4: Circle CenterX=-4.2 CenterY=-26.5 CenterZ=0 NormalX=0 NormalY=0 NormalZ=1 AngleXU=0 Radius=1
    g5: Circle CenterX=-8.2 CenterY=-26.5 CenterZ=0 NormalX=0 NormalY=0 NormalZ=1 AngleXU=0 Radius=1
    g6: BSplineCurve PolesCount=3 KnotsCount=2 Degree=2 IsPeriodic=0
    g7: GeomPoint X=-4.2 Y=-13.4877 Z=0
    g8: GeomPoint X=-8.2 Y=-26.5 Z=0
    g9: LineSegment StartX=-14 StartY=-26.5 StartZ=0 EndX=-8.2 EndY=-26.5 EndZ=0
    g10: LineSegment StartX=-10.15 StartY=-12 StartZ=0 EndX=-10.15 EndY=-14 EndZ=0
    g11: LineSegment StartX=-12.8401 StartY=-16 StartZ=0 EndX=-10.1571 EndY=-16 EndZ=0
    g12: LineSegment StartX=-10.15 StartY=-14 StartZ=0 EndX=-8.70761 EndY=-14 EndZ=0
    g13: LineSegment StartX=-12.8401 StartY=-16 StartZ=0 EndX=-12.8401 EndY=-17.6958 EndZ=0
    g14: LineSegment StartX=-10.15 StartY=-12 StartZ=0 EndX=-7.79258 EndY=-12 EndZ=0
    g15: Circle CenterX=-6.2215 CenterY=-2 CenterZ=0 NormalX=0 NormalY=0 NormalZ=1 AngleXU=0 Radius=1
    g16: Circle CenterX=-6.22762 CenterY=-2.58724 CenterZ=0 NormalX=0 NormalY=0 NormalZ=1 AngleXU=0 Radius=1
    g17: Circle CenterX=-6.32538 CenterY=-4 CenterZ=0 NormalX=0 NormalY=0 NormalZ=1 AngleXU=0 Radius=1
    g18: BSplineCurve PolesCount=3 KnotsCount=2 Degree=2 IsPeriodic=0
    g19: GeomPoint X=-6.2215 Y=-2 Z=0
    g20: GeomPoint X=-6.32538 Y=-4 Z=0
    g21: Circle CenterX=-6.48644 CenterY=-5.99526 CenterZ=0 NormalX=0 NormalY=0 NormalZ=1 AngleXU=0 Radius=1
    g22: Circle CenterX=-6.58486 CenterY=-6.99526 CenterZ=0 NormalX=0 NormalY=0 NormalZ=1 AngleXU=0 Radius=1
    g23: Circle CenterX=-6.77343 CenterY=-8 CenterZ=0 NormalX=0 NormalY=0 NormalZ=1 AngleXU=0 Radius=1
    g24: BSplineCurve PolesCount=3 KnotsCount=2 Degree=2 IsPeriodic=0
    g25: GeomPoint X=-6.48644 Y=-5.99526 Z=0
    g26: GeomPoint X=-6.77343 Y=-8 Z=0
    g27: Circle CenterX=-7.19003 CenterY=-10 CenterZ=0 NormalX=0 NormalY=0 NormalZ=1 AngleXU=0 Radius=1
    g28: Circle CenterX=-7.44407 CenterY=-11.0915 CenterZ=0 NormalX=0 NormalY=0 NormalZ=1 AngleXU=0 Radius=1
    g29: Circle CenterX=-7.79258 CenterY=-12 CenterZ=0 NormalX=0 NormalY=0 NormalZ=1 AngleXU=0 Radius=1
    g30: BSplineCurve PolesCount=3 KnotsCount=2 Degree=2 IsPeriodic=0
    g31: GeomPoint X=-7.19003 Y=-10 Z=0
    g32: GeomPoint X=-7.79258 Y=-12 Z=0
    g33: Circle CenterX=-8.70761 CenterY=-14 CenterZ=0 NormalX=0 NormalY=0 NormalZ=1 AngleXU=0 Radius=1
    g34: Circle CenterX=-9.33087 CenterY=-15.1837 CenterZ=0 NormalX=0 NormalY=0 NormalZ=1 AngleXU=0 Radius=1
    g35: Circle CenterX=-10.1571 CenterY=-16 CenterZ=0 NormalX=0 NormalY=0 NormalZ=1 AngleXU=0 Radius=1
    g36: BSplineCurve PolesCount=3 KnotsCount=2 Degree=2 IsPeriodic=0
    g37: GeomPoint X=-8.70761 Y=-14 Z=0
    g38: GeomPoint X=-10.1571 Y=-16 Z=0
    g39: Circle CenterX=-12.8401 CenterY=-17.6958 CenterZ=0 NormalX=0 NormalY=0 NormalZ=1 AngleXU=0 Radius=1
    g40: Circle CenterX=-13.3521 CenterY=-17.9027 CenterZ=0 NormalX=0 NormalY=0 NormalZ=1 AngleXU=0 Radius=1
    g41: Circle CenterX=-14 CenterY=-18 CenterZ=0 NormalX=0 NormalY=0 NormalZ=1 AngleXU=0 Radius=1
    g42: BSplineCurve PolesCount=3 KnotsCount=2 Degree=2 IsPeriodic=0
    g43: GeomPoint X=-12.8401 Y=-17.6958 Z=0
    g44: GeomPoint X=-14 Y=-18 Z=0
    g45: LineSegment StartX=-6.2 StartY=0 StartZ=0 EndX=-7.2 EndY=0 EndZ=0
    g46: LineSegment StartX=-7.2 StartY=0 StartZ=0 EndX=-7.2 EndY=-2 EndZ=0
    g47: LineSegment StartX=-7.2 StartY=-2 StartZ=0 EndX=-6.2215 EndY=-2 EndZ=0
    g48: LineSegment StartX=-6.32538 StartY=-4 StartZ=0 EndX=-7.65538 EndY=-4 EndZ=0
    g49: LineSegment StartX=-7.65538 StartY=-4 StartZ=0 EndX=-7.65538 EndY=-5.99526 EndZ=0
    g50: LineSegment StartX=-7.65538 StartY=-5.99526 StartZ=0 EndX=-6.48644 EndY=-5.99526 EndZ=0
    g51: LineSegment StartX=-6.77343 StartY=-8 StartZ=0 EndX=-8.43343 EndY=-8 EndZ=0
    g52: LineSegment StartX=-8.43343 StartY=-8 StartZ=0 EndX=-8.43343 EndY=-10 EndZ=0
    g53: LineSegment StartX=-8.43343 StartY=-10 StartZ=0 EndX=-7.19003 EndY=-10 EndZ=0
  constraints (112):
    c: Horizontal(g0)
    c: Distance(g0) = 2
    c: Block(g0)
    c: Vertical(g1)
    c: Coincident(g2,g0)
    c: Vertical(g2)
    c: Block(g2)
    c: Coincident(g6,g2)
    c: Weight(g3) = 1
    c: Equal(g3,g4)
    c: Equal(g3,g5)
    c: InternalAlignment(g3,g6)
    c: InternalAlignment(g4,g6)
    c: InternalAlignment(g5,g6)
    c: InternalAlignment(g7,g6)
    c: InternalAlignment(g8,g6)
    c: Block(g6)
    c: Coincident(g9,g1)
    c: Coincident(g9,g6)
    c: Horizontal(g9)
    c: Vertical(g10)
    c: Block(g10)
    c: Horizontal(g11)
    c: Block(g11)
    c: Coincident(g12,g10)
    c: Horizontal(g12)
    c: Block(g12)
    c: Coincident(g13,g11)
    c: Vertical(g13)
    c: Block(g13)
    c: Coincident(g14,g10)
    c: Horizontal(g14)
    c: Block(g14)
    c: Block(g9)
    c: Block(g1)
    c: Weight(g15) = 1
    c: Equal(g15,g16)
    c: Equal(g15,g17)
    c: InternalAlignment(g15,g18)
    c: InternalAlignment(g16,g18)
    c: InternalAlignment(g17,g18)
    c: InternalAlignment(g19,g18)
    c: InternalAlignment(g20,g18)
    c: Weight(g21) = 1
    c: Equal(g21,g22)
    c: Equal(g21,g23)
    c: InternalAlignment(g21,g24)
    c: InternalAlignment(g22,g24)
    c: InternalAlignment(g23,g24)
    c: InternalAlignment(g25,g24)
    c: InternalAlignment(g26,g24)
    c: Weight(g27) = 1
    c: Equal(g27,g28)
    c: Equal(g27,g29)
    c: Coincident(g30,g14)
    c: InternalAlignment(g27,g30)
    c: InternalAlignment(g28,g30)
    c: InternalAlignment(g29,g30)
    c: InternalAlignment(g31,g30)
    c: InternalAlignment(g32,g30)
    c: Coincident(g36,g12)
    c: Weight(g33) = 1
    c: Equal(g33,g34)
    c: Equal(g33,g35)
    c: Coincident(g36,g11)
    c: InternalAlignment(g33,g36)
    c: InternalAlignment(g34,g36)
    c: InternalAlignment(g35,g36)
    c: InternalAlignment(g37,g36)
    c: InternalAlignment(g38,g36)
    c: Coincident(g42,g13)
    c: Weight(g39) = 1
    c: Equal(g39,g40)
    c: Equal(g39,g41)
    c: Coincident(g42,g1)
    c: InternalAlignment(g39,g42)
    c: InternalAlignment(g40,g42)
    c: InternalAlignment(g41,g42)
    c: InternalAlignment(g43,g42)
    c: InternalAlignment(g44,g42)
    c: Block(g18)
    c: Block(g24)
    c: Block(g30)
    c: Block(g36)
    c: Block(g42)
    c: Horizontal(g45)
    c: Coincident(g45,g0)
    c: Vertical(g46)
    c: Coincident(g46,g45)
    c: Coincident(g47,g46)
    c: Coincident(g47,g18)
    c: Horizontal(g47)
    c: Block(g46)
    c: Coincident(g48,g18)
    c: Horizontal(g48)
    c: Distance(g48) = 1.33
    c: Vertical(g49)
    c: Coincident(g49,g48)
    c: Coincident(g50,g49)
    c: Coincident(g50,g24)
    c: Horizontal(g50)
    c: Tangent(g50,g22)
    c: Horizontal(g51)
    c: Coincident(g51,g24)
    c: Block(g51)
    c: Vertical(g52)
    c: Block(g52)
    c: Coincident(g52,g51)
    c: Coincident(g53,g52)
    c: Coincident(g53,g30)
    c: Horizontal(g53)
    c: Distance(g1) = 8.5
FEATURE [Part::Feature] Face024
  shape: bbox 9.8 x 26.5 x 2e-07 mm, 1 faces, 0 solids (baked)
FEATURE [Part::Revolution] Revolve024
  Angle = 360
  Axis = (0,1,0)
  Base = (0,0,0)
  FaceMakerClass = Part::FaceMakerBullseye
  Placement = pos=(0,0,0) rot=(0,0,1;1.5708rad)
  Solid = false
  Source = -> Face024
  Symmetric = false
FEATURE [Part::Feature] Face025
  shape: bbox 9.8 x 26.5 x 2e-07 mm, 1 faces, 0 solids (baked)
FEATURE [Part::Revolution] Revolve025
  Angle = 360
  Axis = (0,1,0)
  Base = (0,0,0)
  FaceMakerClass = Part::FaceMakerBullseye
  Placement = pos=(0,0,0) rot=(0,0,1;1.5708rad)
  Solid = false
  Source = -> Face025
  Symmetric = false
FEATURE [Part::MultiFuse] Fusion033
  Placement = pos=(-18,19,36) rot=(0,0,1;0rad)
  Shapes = -> [Revolve025,Revolve024]
FEATURE [Part::Cylinder] Cylinder014
  Angle = 360
  AttacherType = Attacher::AttachEngine3D
  Height = 20
  Placement = pos=(0,0,36.15) rot=(0,0,1;0rad)
  Radius = 14.3
FEATURE [Part::Cylinder] Cylinder015
  Angle = 360
  AttacherType = Attacher::AttachEngine3D
  Height = 10
  Placement = pos=(0,0,36.15) rot=(0,0,1;0rad)
  Radius = 4
FEATURE [Part::MultiFuse] Fusion034  label="removeToCreteHoleForPlugHousing004"
  Placement = pos=(-42,19,36) rot=(0,1,0;1.5708rad)
  Shapes = -> [Cylinder014,Cylinder015]
FEATURE [Part::Cut] Cut008  label="top004"
  Base = -> Cut004
  Placement = pos=(-1,0,0) rot=(0,0,1;0rad)
  Tool = -> Fusion034
FEATURE [Part::Box] Box005  label="Cube005"
  AttacherType = Attacher::AttachEngine3D
  Height = 28
  Length = 3
  Placement = pos=(110.7,19,22) rot=(0,0,1;0rad)
  Width = 15.7
FEATURE [Part::Cylinder] Cylinder016
  Angle = 360
  AttacherType = Attacher::AttachEngine3D
  Height = 10
  Placement = pos=(0,0,36.15) rot=(0,0,1;0rad)
  Radius = 4
FEATURE [Part::Cylinder] Cylinder017
  Angle = 360
  AttacherType = Attacher::AttachEngine3D
  Height = 20
  Placement = pos=(0,0,36.15) rot=(0,0,1;0rad)
  Radius = 10.3
FEATURE [Part::MultiFuse] Fusion035  label="removeToCreteHoleForPlugHousing005"
  Placement = pos=(70,19,36) rot=(0,1,0;1.5708rad)
  Shapes = -> [Cylinder017,Cylinder016]
FEATURE [Part::Cut] Cut009  label="plugHousingTab001"
  Base = -> Box005
  Placement = pos=(-107.4,-14,0) rot=(0,0,1;0rad)
  Tool = -> Fusion035
FEATURE [Part::Box] Box006  label="Cube006"
  AttacherType = Attacher::AttachEngine3D
  Height = 28
  Length = 3
  Placement = pos=(110.7,19,22) rot=(0,0,1;0rad)
  Width = 15.7
FEATURE [Part::Cylinder] Cylinder018
  Angle = 360
  AttacherType = Attacher::AttachEngine3D
  Height = 10
  Placement = pos=(0,0,36.15) rot=(0,0,1;0rad)
  Radius = 4
FEATURE [Part::Cylinder] Cylinder019
  Angle = 360
  AttacherType = Attacher::AttachEngine3D
  Height = 20
  Placement = pos=(0,0,36.15) rot=(0,0,1;0rad)
  Radius = 10.3
FEATURE [Part::MultiFuse] Fusion036  label="removeToCreteHoleForPlugHousing006"
  Placement = pos=(70,19,36) rot=(0,1,0;1.5708rad)
  Shapes = -> [Cylinder019,Cylinder018]
FEATURE [Part::Cut] Cut010  label="plugHousingTab002"
  Base = -> Box006
  Placement = pos=(-107.4,-14,0) rot=(0,0,1;0rad)
  Tool = -> Fusion036
FEATURE [Part::MultiFuse] Fusion037
  Placement = pos=(9.6,23,0) rot=(0,0,1;3.14159rad)
  Shapes = -> [Cut009,Cut010]
FEATURE [Part::Box] Box  label="Cube"
  AttacherType = Attacher::AttachEngine3D
  Height = 10
  Length = 3
  Placement = pos=(3.3,4,12) rot=(0,0,1;0rad)
  Width = 10
FEATURE [Part::Fillet] Fillet004
  Base = -> Fusion028
  Edges = 1 edges r=2: [Edge25]
FEATURE [Part::Fillet] Fillet005  label="plugHousing046"
  Base = -> Fillet004
  Edges = 1 edges r=2: [Edge8]
FEATURE [Part::Fillet] Fillet006
  Base = -> Box
  Edges = 1 edges r=2: [Edge11]
FEATURE [Part::Box] Box007  label="Cube007"
  AttacherType = Attacher::AttachEngine3D
  Height = 10
  Length = 3
  Placement = pos=(3.3,4,50) rot=(0,0,1;0rad)
  Width = 10
FEATURE [Part::Fillet] Fillet007
  Base = -> Box007
  Edges = 1 edges r=2: [Edge12]
FEATURE [Part::Box] Box008  label="Cube008"
  AttacherType = Attacher::AttachEngine3D
  Height = 28
  Length = 4
  Placement = pos=(5,0,22) rot=(0,0,1;0rad)
  Width = 10
FEATURE [Part::Fillet] Fillet008
  Base = -> Box008
  Edges = 1 edges r=1: [Edge7]
FEATURE [Part::Fillet] Fillet009
  Base = -> Fillet008
  Edges = 1 edges r=2: [Edge5]
FEATURE [Part::Fillet] Fillet010
  Base = -> Fillet009
  Edges = 1 edges r=2: [Edge2]
FEATURE [Sketcher::SketchObject] Sketch009  label="topSketch003"
  FullyConstrained = true
  sketch-geometry (4):
    g0: LineSegment StartX=16.8446 StartY=31.512 StartZ=0 EndX=16.3251 EndY=34.4666 EndZ=0
    g1: ArcOfCircle CenterX=19 CenterY=19.2524 CenterZ=0 NormalX=0 NormalY=0 NormalZ=1 AngleXU=0 Radius=15.4476 StartAngle=1.74483 EndAngle=2.72717
    g2: ArcOfCircle CenterX=19 CenterY=19.2524 CenterZ=0 NormalX=0 NormalY=0 NormalZ=1 AngleXU=0 Radius=12.4476 StartAngle=1.74483 EndAngle=2.73189
    g3: LineSegment StartX=4.86004 StartY=25.4725 StartZ=0 EndX=7.58253 EndY=24.2107 EndZ=0
  constraints (7):
    c: Block(g0)
    c: Coincident(g1,g0)
    c: Coincident(g2,g0)
    c: Coincident(g3,g1)
    c: Coincident(g3,g2)
    c: Block(g1)
    c: Block(g2)
FEATURE [Part::Extrusion] Extrude008
  Base = -> Sketch009
  Dir = (0,0,1)
  DirMode = 2
  FaceMakerClass = Part::FaceMakerBullseye
  LengthFwd = 10
  LengthRev = 0
  Placement = pos=(0,0,31) rot=(0,0,1;0rad)
  Solid = true
  Symmetric = false
FEATURE [Part::Cylinder] Cylinder020
  Angle = 360
  AttacherType = Attacher::AttachEngine3D
  Height = 20
  Placement = pos=(0,0,36.15) rot=(0,0,1;0rad)
  Radius = 8.2
FEATURE [Part::Cylinder] Cylinder021
  Angle = 360
  AttacherType = Attacher::AttachEngine3D
  Height = 10
  Placement = pos=(0,0,36.15) rot=(0,0,1;0rad)
  Radius = 4
FEATURE [Part::MultiFuse] Fusion038  label="removeToCreteHoleForPlugHousing007"
  Placement = pos=(-42,19,36) rot=(0,1,0;1.5708rad)
  Shapes = -> [Cylinder020,Cylinder021]
FEATURE [Part::Cut] Cut011
  Base = -> Extrude008
  Tool = -> Fusion038
FEATURE [Part::Fillet] Fillet011
  Base = -> Cut011
  Edges = 1 edges r=2: [Edge1]
FEATURE [Part::Fillet] Fillet012
  Base = -> Fillet011
  Edges = 1 edges r=2.5: [Edge1]
FEATURE [Part::Fillet] Fillet013
  Base = -> Fillet012
  Edges = 1 edges r=2.5: [Edge2]
FEATURE [Part::Box] Box010  label="Cube010"
  AttacherType = Attacher::AttachEngine3D
  Height = 16
  Length = 8
  Placement = pos=(12.7,31.52,28) rot=(0,0,1;0rad)
  Width = 4
FEATURE [Sketcher::SketchObject] Sketch010  label="topSketch004"
  FullyConstrained = true
  sketch-geometry (4):
    g0: LineSegment StartX=16.8446 StartY=31.512 StartZ=0 EndX=16.3251 EndY=34.4666 EndZ=0
    g1: ArcOfCircle CenterX=19 CenterY=19.2524 CenterZ=0 NormalX=0 NormalY=0 NormalZ=1 AngleXU=0 Radius=15.4476 StartAngle=1.74483 EndAngle=2.72717
    g2: ArcOfCircle CenterX=19 CenterY=19.2524 CenterZ=0 NormalX=0 NormalY=0 NormalZ=1 AngleXU=0 Radius=12.4476 StartAngle=1.74483 EndAngle=2.73189
    g3: LineSegment StartX=4.86004 StartY=25.4725 StartZ=0 EndX=7.58253 EndY=24.2107 EndZ=0
  constraints (7):
    c: Block(g0)
    c: Coincident(g1,g0)
    c: Coincident(g2,g0)
    c: Coincident(g3,g1)
    c: Coincident(g3,g2)
    c: Block(g1)
    c: Block(g2)
FEATURE [Part::Cylinder] Cylinder022
  Angle = 360
  AttacherType = Attacher::AttachEngine3D
  Height = 10
  Placement = pos=(0,0,36.15) rot=(0,0,1;0rad)
  Radius = 4
FEATURE [Sketcher::SketchObject] Sketch011  label="topSketch005"
  FullyConstrained = true
  sketch-geometry (4):
    g0: LineSegment StartX=16.8446 StartY=31.512 StartZ=0 EndX=16.3251 EndY=34.4666 EndZ=0
    g1: ArcOfCircle CenterX=19 CenterY=19.2524 CenterZ=0 NormalX=0 NormalY=0 NormalZ=1 AngleXU=0 Radius=15.4476 StartAngle=1.74483 EndAngle=2.72717
    g2: ArcOfCircle CenterX=19 CenterY=19.2524 CenterZ=0 NormalX=0 NormalY=0 NormalZ=1 AngleXU=0 Radius=12.4476 StartAngle=1.74483 EndAngle=2.73189
    g3: LineSegment StartX=4.86004 StartY=25.4725 StartZ=0 EndX=7.58253 EndY=24.2107 EndZ=0
  constraints (7):
    c: Block(g0)
    c: Coincident(g1,g0)
    c: Coincident(g2,g0)
    c: Coincident(g3,g1)
    c: Coincident(g3,g2)
    c: Block(g1)
    c: Block(g2)
FEATURE [Part::Extrusion] Extrude010
  Base = -> Sketch011
  Dir = (0,0,1)
  DirMode = 2
  FaceMakerClass = Part::FaceMakerBullseye
  LengthFwd = 10.6
  LengthRev = 0
  Placement = pos=(0,0,31) rot=(0,0,1;0rad)
  Solid = true
  Symmetric = false
FEATURE [Part::Cylinder] Cylinder023
  Angle = 360
  AttacherType = Attacher::AttachEngine3D
  Height = 20
  Placement = pos=(0,0,36.15) rot=(0,0,1;0rad)
  Radius = 8.2
FEATURE [Part::MultiFuse] Fusion039  label="removeToCreteHoleForPlugHousing008"
  Placement = pos=(-42,19,36) rot=(0,1,0;1.5708rad)
  Shapes = -> [Cylinder023,Cylinder022]
FEATURE [Part::Cut] Cut012
  Base = -> Extrude010
  Placement = pos=(0,0,-0.3) rot=(0,0,1;0rad)
  Tool = -> Fusion039
FEATURE [Part::Cut] Cut013
  Base = -> Box010
  Tool = -> Cut012
FEATURE [Part::Fillet] Fillet014
  Base = -> Cut013
  Edges = 1 edges r=0.7: [Edge13]
FEATURE [Part::Fillet] Fillet015
  Base = -> Fillet014
  Edges = 1 edges r=0.7: [Edge13]
FEATURE [Part::Fillet] Fillet016
  Base = -> Fillet015
  Edges = 1 edges r=0.7: [Edge16]
FEATURE [Part::Fillet] Fillet017
  Base = -> Fillet016
  Edges = 1 edges r=0.7: [Edge11]
FEATURE [Part::Fillet] Fillet018
  Base = -> Fillet017
  Edges = 1 edges r=0.7: [Edge10]
FEATURE [Part::Fillet] Fillet019
  Base = -> Fillet018
  Edges = 1 edges r=1.2: [Edge5]
FEATURE [Part::Fillet] Fillet020
  Base = -> Fillet019
  Edges = 1 edges r=1.2: [Edge12]
FEATURE [Part::Fillet] Fillet021
  Base = -> Fillet020
  Edges = 1 edges r=2: [Edge1]
  Placement = pos=(0.3,0,0) rot=(0,0,1;0rad)
FEATURE [Part::MultiFuse] Fusion040  label="top005"
  Shapes = -> [Cut008,Fillet021]
FEATURE [Part::MultiFuse] Fusion041  label="wireHolder"
  Shapes = -> [Fusion033,Fillet013]
FEATURE [Part::MultiFuse] Fusion042
  Shapes = -> [Fillet007,Fusion041]
FEATURE [Part::MultiFuse] Fusion043  label="wireHolder001"
  Shapes = -> [Fusion042,Fillet010]
FEATURE [Part::MultiFuse] Fusion044  label="wireHolder002"
  Shapes = -> [Fillet006,Fusion037,Fusion043]
FEATURE [Part::Feature] Face026
  shape: bbox 11 x 6 x 2e-07 mm, 1 faces, 0 solids (baked)
FEATURE [Part::Revolution] Revolve026
  Angle = 360
  Axis = (0,1,0)
  Base = (0,0,0)
  FaceMakerClass = Part::FaceMakerBullseye
  Placement = pos=(30.3,-1,19.7) rot=(0,0,1;0rad)
  Solid = false
  Source = -> Face026
  Symmetric = false
FEATURE [Sketcher::SketchObject] Sketch013  label="topSketch006"
  FullyConstrained = true
  sketch-geometry (13):
    g0: LineSegment StartX=117 StartY=19 StartZ=0 EndX=117 EndY=38 EndZ=0
    g1: ArcOfCircle CenterX=98 CenterY=19 CenterZ=0 NormalX=0 NormalY=0 NormalZ=1 AngleXU=0 Radius=19 StartAngle=5.7297 EndAngle=6.28319
    g2: LineSegment StartX=0 StartY=3 StartZ=0 EndX=0 EndY=19 EndZ=0
    g3: LineSegment StartX=19 StartY=38 StartZ=0 EndX=117 EndY=38 EndZ=0
    g4: ArcOfCircle CenterX=19 CenterY=19 CenterZ=0 NormalX=0 NormalY=0 NormalZ=1 AngleXU=0 Radius=19 StartAngle=1.5708 EndAngle=3.14159
    g5: ArcOfCircle CenterX=19 CenterY=19 CenterZ=0 NormalX=0 NormalY=0 NormalZ=1 AngleXU=0 Radius=16 StartAngle=1.5708 EndAngle=3.14159
    g6: ArcOfCircle CenterX=98 CenterY=19 CenterZ=0 NormalX=0 NormalY=0 NormalZ=1 AngleXU=0 Radius=16 StartAngle=5.60905 EndAngle=6.28319
    g7: LineSegment StartX=114 StartY=19 StartZ=0 EndX=114 EndY=35 EndZ=0
    g8: LineSegment StartX=110.5 StartY=9.01251 StartZ=0 EndX=114.163 EndY=9.01251 EndZ=0
    g9: LineSegment StartX=114 StartY=35 StartZ=0 EndX=19 EndY=35 EndZ=0
    g10: LineSegment StartX=0 StartY=3 StartZ=0 EndX=0 EndY=0 EndZ=0
    g11: LineSegment StartX=3 StartY=0 StartZ=0 EndX=0 EndY=0 EndZ=0
    g12: LineSegment StartX=3 StartY=19 StartZ=0 EndX=3 EndY=0 EndZ=0
  constraints (33):
    c: Vertical(g0)
    c: Distance(g0) = 19
    c: Block(g0)
    c: Coincident(g1,g0)
    c: Block(g1)
    c: Vertical(g2)
    c: Block(g2)
    c: Coincident(g3,g0)
    c: Horizontal(g3)
    c: Distance(g3) = 98
    c: Coincident(g4,g3)
    c: Coincident(g4,g2)
    c: Block(g4)
    c: Coincident(g5,g4)
    c: Coincident(g6,g1)
    c: Block(g6)
    c: Block(g5)
    c: Coincident(g7,g6)
    c: Vertical(g7)
    c: Coincident(g8,g6)
    c: Coincident(g8,g1)
    c: Coincident(g9,g7)
    c: Coincident(g9,g5)
    c: Horizontal(g9)
    c: Tangent(g9,g5)
    c: Coincident(g10,g2)
    c: Distance(g10) = 3
    c: Vertical(g10)
    c: Coincident(g11,g10)
    c: Horizontal(g11)
    c: Coincident(g12,g5)
    c: Coincident(g12,g11)
    c: Vertical(g12)
FEATURE [Part::Extrusion] Extrude011  label="top006"
  Base = -> Sketch013
  Dir = (0,0,1)
  DirMode = 2
  FaceMakerClass = Part::FaceMakerBullseye
  LengthFwd = 72
  LengthRev = 0
  Solid = true
  Symmetric = false
FEATURE [Sketcher::SketchObject] Sketch014
  FullyConstrained = true
  MapMode = 3
  Placement = pos=(0,0,0) rot=(1,0,0;1.5708rad)
  Support = -> [Extrude011]
  sketch-geometry (8):
    g0: Circle CenterX=80.351 CenterY=-67.6202 CenterZ=0 NormalX=0 NormalY=0 NormalZ=1 AngleXU=0 Radius=2
    g1: Circle CenterX=80.351 CenterY=-67.6202 CenterZ=0 NormalX=0 NormalY=0 NormalZ=1 AngleXU=0 Radius=3
    g2: Circle CenterX=80.351 CenterY=-4.92017 CenterZ=0 NormalX=0 NormalY=0 NormalZ=1 AngleXU=0 Radius=2
    g3: Circle CenterX=80.351 CenterY=-4.92017 CenterZ=0 NormalX=0 NormalY=0 NormalZ=1 AngleXU=0 Radius=3
    g4: Circle CenterX=23.851 CenterY=-4.92017 CenterZ=0 NormalX=0 NormalY=0 NormalZ=1 AngleXU=0 Radius=2
    g5: Circle CenterX=23.851 CenterY=-4.92017 CenterZ=0 NormalX=0 NormalY=0 NormalZ=1 AngleXU=0 Radius=3
    g6: Circle CenterX=23.851 CenterY=-67.6202 CenterZ=0 NormalX=0 NormalY=0 NormalZ=1 AngleXU=0 Radius=2
    g7: Circle CenterX=23.851 CenterY=-67.6202 CenterZ=0 NormalX=0 NormalY=0 NormalZ=1 AngleXU=0 Radius=3
  constraints (8):
    c: Block(g3)
    c: Block(g2)
    c: Block(g1)
    c: Block(g0)
    c: Block(g6)
    c: Block(g7)
    c: Block(g4)
    c: Block(g5)
FEATURE [Part::Feature] Face027
  shape: bbox 11 x 6 x 2e-07 mm, 1 faces, 0 solids (baked)
FEATURE [Part::Revolution] Revolve027
  Angle = 360
  Axis = (0,1,0)
  Base = (0,0,0)
  FaceMakerClass = Part::FaceMakerBullseye
  Placement = pos=(30.3,-1,51.7) rot=(0,0,1;0rad)
  Solid = false
  Source = -> Face027
  Symmetric = false
FEATURE [Part::Feature] Face028
  shape: bbox 11 x 6 x 2e-07 mm, 1 faces, 0 solids (baked)
FEATURE [Part::Revolution] Revolve028
  Angle = 360
  Axis = (0,1,0)
  Base = (0,0,0)
  FaceMakerClass = Part::FaceMakerBullseye
  Placement = pos=(62.3,-1,19.7) rot=(0,0,1;0rad)
  Solid = false
  Source = -> Face028
  Symmetric = false
FEATURE [Part::Feature] Face029
  shape: bbox 11 x 6 x 2e-07 mm, 1 faces, 0 solids (baked)
FEATURE [Part::Revolution] Revolve029
  Angle = 360
  Axis = (0,1,0)
  Base = (0,0,0)
  FaceMakerClass = Part::FaceMakerBullseye
  Placement = pos=(62.3,-1,51.7) rot=(0,0,1;0rad)
  Solid = false
  Source = -> Face029
  Symmetric = false
FEATURE [Part::Feature] Wire
  shape: bbox 11 x 5.2 x 2e-07 mm, 0 faces, 0 solids (baked)
FEATURE [Part::Revolution] Revolve030
  Angle = 360
  Axis = (0,1,0)
  Base = (0,0,0)
  FaceMakerClass = Part::FaceMakerBullseye
  Placement = pos=(30.3,38,19.7) rot=(0,0,1;0rad)
  Solid = true
  Source = -> Wire
  Symmetric = false
FEATURE [Part::Feature] Wire001
  shape: bbox 11 x 5.2 x 2e-07 mm, 0 faces, 0 solids (baked)
FEATURE [Part::Revolution] Revolve031
  Angle = 360
  Axis = (0,1,0)
  Base = (0,0,0)
  FaceMakerClass = Part::FaceMakerBullseye
  Placement = pos=(30.3,38,51.7) rot=(0,0,1;0rad)
  Solid = true
  Source = -> Wire001
  Symmetric = false
FEATURE [Part::Feature] Wire002
  shape: bbox 11 x 5.2 x 2e-07 mm, 0 faces, 0 solids (baked)
FEATURE [Part::Revolution] Revolve032
  Angle = 360
  Axis = (0,1,0)
  Base = (0,0,0)
  FaceMakerClass = Part::FaceMakerBullseye
  Placement = pos=(62.3,38,51.7) rot=(0,0,1;0rad)
  Solid = true
  Source = -> Wire002
  Symmetric = false
FEATURE [Part::Feature] Wire003
  shape: bbox 11 x 5.2 x 2e-07 mm, 0 faces, 0 solids (baked)
FEATURE [Part::Revolution] Revolve033
  Angle = 360
  Axis = (0,1,0)
  Base = (0,0,0)
  FaceMakerClass = Part::FaceMakerBullseye
  Placement = pos=(62.3,38,19.7) rot=(0,0,1;0rad)
  Solid = true
  Source = -> Wire003
  Symmetric = false
FEATURE [Part::MultiFuse] Fusion045  label="altRandScrewHousing"
  Shapes = -> [Revolve029,Revolve027,Revolve028,Revolve026]
FEATURE [Part::MultiFuse] Fusion046  label="fanScrewHousing"
  Shapes = -> [Revolve033,Revolve032,Revolve031,Revolve030]
FEATURE [Sketcher::SketchObject] Sketch015
  FullyConstrained = true
  sketch-geometry (17):
    g0: Circle CenterX=-3.5 CenterY=23.5 CenterZ=0 NormalX=0 NormalY=0 NormalZ=1 AngleXU=0 Radius=1
    g1: Circle CenterX=-1 CenterY=15.25 CenterZ=0 NormalX=0 NormalY=0 NormalZ=1 AngleXU=0 Radius=1
    g2: Circle CenterX=-3.5 CenterY=7 CenterZ=0 NormalX=0 NormalY=0 NormalZ=1 AngleXU=0 Radius=1
    g3: BSplineCurve PolesCount=3 KnotsCount=2 Degree=2 IsPeriodic=0
    g4: GeomPoint X=-3.5 Y=23.5 Z=0
    g5: GeomPoint X=-3.5 Y=7 Z=0
    g6: Circle CenterX=-4.8 CenterY=30.5 CenterZ=0 NormalX=0 NormalY=0 NormalZ=1 AngleXU=0 Radius=1
    g7: Circle CenterX=-3.5 CenterY=30.5 CenterZ=0 NormalX=0 NormalY=0 NormalZ=1 AngleXU=0 Radius=1
    g8: Circle CenterX=-3.5 CenterY=29.2 CenterZ=0 NormalX=0 NormalY=0 NormalZ=1 AngleXU=0 Radius=1
    g9: BSplineCurve PolesCount=3 KnotsCount=2 Degree=2 IsPeriodic=0
    g10: GeomPoint X=-4.8 Y=30.5 Z=0
    g11: GeomPoint X=-3.5 Y=29.2 Z=0
    g12: LineSegment StartX=-3.5 StartY=29.2 StartZ=0 EndX=-3.5 EndY=23.5 EndZ=0
    g13: LineSegment StartX=-4.8 StartY=30.5 StartZ=0 EndX=0 EndY=30.5 EndZ=0
    g14: LineSegment StartX=-3.5 StartY=0.3 StartZ=0 EndX=0 EndY=0.3 EndZ=0
    g15: LineSegment StartX=-3.5 StartY=0.3 StartZ=0 EndX=-3.5 EndY=7 EndZ=0
    g16: LineSegment StartX=0 StartY=0.3 StartZ=0 EndX=0 EndY=30.5 EndZ=0
  constraints (33):
    c: Weight(g0) = 1
    c: Equal(g0,g1)
    c: Equal(g0,g2)
    c: InternalAlignment(g0,g3)
    c: InternalAlignment(g1,g3)
    c: InternalAlignment(g2,g3)
    c: InternalAlignment(g4,g3)
    c: InternalAlignment(g5,g3)
    c: Block(g3)
    c: Weight(g6) = 1
    c: Equal(g6,g7)
    c: Equal(g6,g8)
    c: InternalAlignment(g6,g9)
    c: InternalAlignment(g7,g9)
    c: InternalAlignment(g8,g9)
    c: InternalAlignment(g10,g9)
    c: InternalAlignment(g11,g9)
    c: Block(g9)
    c: Coincident(g12,g9)
    c: Coincident(g12,g3)
    c: Vertical(g12)
    c: Coincident(g13,g9)
    c: Horizontal(g13)
    c: Distance(g13) = 4.8
    c: Horizontal(g14)
    c: Block(g14)
    c: Coincident(g15,g14)
    c: Coincident(g15,g3)
    c: Vertical(g15)
    c: Coincident(g16,g14)
    c: Coincident(g16,g13)
    c: Vertical(g16)
    c: Tangent(g16,g1)
FEATURE [Sketcher::SketchObject] Sketch016
  FullyConstrained = true
  sketch-geometry (16):
    g0: Circle CenterX=-3.5 CenterY=23.5 CenterZ=0 NormalX=0 NormalY=0 NormalZ=1 AngleXU=0 Radius=1
    g1: Circle CenterX=-1 CenterY=15.25 CenterZ=0 NormalX=0 NormalY=0 NormalZ=1 AngleXU=0 Radius=1
    g2: Circle CenterX=-3.5 CenterY=7 CenterZ=0 NormalX=0 NormalY=0 NormalZ=1 AngleXU=0 Radius=1
    g3: BSplineCurve PolesCount=3 KnotsCount=2 Degree=2 IsPeriodic=0
    g4: GeomPoint X=-3.5 Y=23.5 Z=0
    g5: GeomPoint X=-3.5 Y=7 Z=0
    g6: LineSegment StartX=-3.5 StartY=28.2 StartZ=0 EndX=-3.5 EndY=23.5 EndZ=0
    g7: LineSegment StartX=0 StartY=29.5 StartZ=0 EndX=0 EndY=30 EndZ=0
    g8: LineSegment StartX=-3.5 StartY=28.2 StartZ=0 EndX=-3.5 EndY=30 EndZ=0
    g9: LineSegment StartX=0 StartY=30 StartZ=0 EndX=0 EndY=30.5 EndZ=0
    g10: LineSegment StartX=0 StartY=30.5 StartZ=0 EndX=-3.5 EndY=30.5 EndZ=0
    g11: LineSegment StartX=-3.5 StartY=30.5 StartZ=0 EndX=-3.5 EndY=30 EndZ=0
    g12: LineSegment StartX=0 StartY=29.5 StartZ=0 EndX=0 EndY=5 EndZ=0
    g13: LineSegment StartX=-3.5 StartY=0.3 StartZ=0 EndX=-3.5 EndY=7 EndZ=0
    g14: LineSegment StartX=-3.5 StartY=0.3 StartZ=0 EndX=0 EndY=0.3 EndZ=0
    g15: LineSegment StartX=0 StartY=5 StartZ=0 EndX=0 EndY=0.3 EndZ=0
  constraints (39):
    c: Weight(g0) = 1
    c: Equal(g0,g1)
    c: Equal(g0,g2)
    c: InternalAlignment(g0,g3)
    c: InternalAlignment(g1,g3)
    c: InternalAlignment(g2,g3)
    c: InternalAlignment(g4,g3)
    c: InternalAlignment(g5,g3)
    c: Block(g3)
    c: Coincident(g6,g3)
    c: Vertical(g6)
    c: Vertical(g7)
    c: Distance(g7) = 0.5
    c: Coincident(g8,g6)
    c: Vertical(g8)
    c: Block(g6)
    c: Block(g7)
    c: Vertical(g9)
    c: Equal(g7,g9) = 0.5
    c: Block(g9)
    c: Coincident(g9,g7)
    c: Horizontal(g10)
    c: Coincident(g10,g9)
    c: Coincident(g11,g10)
    c: Coincident(g11,g8)
    c: Vertical(g11)
    c: Block(g11)
    c: Coincident(g12,g7)
    c: Vertical(g12)
    c: Coincident(g13,g3)
    c: Vertical(g13)
    c: Distance(g13) = 6.7
    c: Coincident(g14,g13)
    c: Horizontal(g14)
    c: Block(g14)
    c: Coincident(g15,g12)
    c: Coincident(g15,g14)
    c: Vertical(g15)
    c: Block(g15)
FEATURE [Sketcher::SketchObject] Sketch017
  FullyConstrained = true
  sketch-geometry (11):
    g0: LineSegment StartX=-3.5 StartY=1e-16 StartZ=0 EndX=-1.6 EndY=1e-16 EndZ=0
    g1: LineSegment StartX=-1.6 StartY=1e-16 StartZ=0 EndX=-1.6 EndY=1.5 EndZ=0
    g2: LineSegment StartX=-3.5 StartY=1.5 StartZ=0 EndX=-1.6 EndY=1.5 EndZ=0
    g3: LineSegment StartX=-3.5 StartY=1e-16 StartZ=0 EndX=-4.8 EndY=1e-16 EndZ=0
    g4: Circle CenterX=-3.5 CenterY=1.3 CenterZ=0 NormalX=0 NormalY=0 NormalZ=1 AngleXU=0 Radius=1
    g5: Circle CenterX=-3.5 CenterY=1e-16 CenterZ=0 NormalX=0 NormalY=0 NormalZ=1 AngleXU=0 Radius=1
    g6: Circle CenterX=-4.8 CenterY=1e-16 CenterZ=0 NormalX=0 NormalY=0 NormalZ=1 AngleXU=0 Radius=1
    g7: BSplineCurve PolesCount=3 KnotsCount=2 Degree=2 IsPeriodic=0
    g8: GeomPoint X=-3.5 Y=1.3 Z=0
    g9: GeomPoint X=-4.8 Y=1e-16 Z=0
    g10: LineSegment StartX=-3.5 StartY=1.3 StartZ=0 EndX=-3.5 EndY=1.5 EndZ=0
  constraints (24):
    c: Horizontal(g0)
    c: Distance(g0) = 1.9
    c: Block(g0)
    c: Coincident(g1,g0)
    c: Vertical(g1)
    c: Coincident(g2,g1)
    c: Horizontal(g2)
    c: Coincident(g3,g0)
    c: Horizontal(g3)
    c: Distance(g3) = 1.3
    c: Weight(g4) = 1
    c: Equal(g4,g5)
    c: Coincident(g5,g0)
    c: Equal(g4,g6)
    c: Coincident(g7,g3)
    c: InternalAlignment(g4,g7)
    c: InternalAlignment(g5,g7)
    c: InternalAlignment(g6,g7)
    c: InternalAlignment(g8,g7)
    c: InternalAlignment(g9,g7)
    c: Coincident(g10,g7)
    c: Coincident(g10,g2)
    c: Vertical(g10)
    c: Block(g10)
FEATURE [Part::Feature] Face035
  shape: bbox 3.2 x 1.5 x 2e-07 mm, 1 faces, 0 solids (baked)
FEATURE [Part::Revolution] Revolve039  label="backCaseScrewRetainer"
  Angle = 360
  Axis = (0,1,0)
  Base = (0,0,0)
  FaceMakerClass = Part::FaceMakerBullseye
  Placement = pos=(12.5,3,62) rot=(0,0,1;0rad)
  Solid = false
  Source = -> Face035
  Symmetric = false
FEATURE [Part::Feature] Face036
  shape: bbox 3.2 x 1.5 x 2e-07 mm, 1 faces, 0 solids (baked)
FEATURE [Part::Feature] Face039
  shape: bbox 4.8 x 30.2 x 2e-07 mm, 1 faces, 0 solids (baked)
FEATURE [Part::Revolution] Revolve043  label="frontCaseScrewPost002"
  Angle = 360
  Axis = (0,1,0)
  Base = (0,0,0)
  FaceMakerClass = Part::FaceMakerBullseye
  Placement = pos=(89.5,4.5,3.5) rot=(0,0,1;0rad)
  Solid = false
  Source = -> Face039
  Symmetric = false
FEATURE [Part::Feature] Face042
  shape: bbox 4.8 x 30.2 x 2e-07 mm, 1 faces, 0 solids (baked)
FEATURE [Part::Revolution] Revolve046  label="frontCaseScrewPost003"
  Angle = 360
  Axis = (0,1,0)
  Base = (0,0,0)
  FaceMakerClass = Part::FaceMakerBullseye
  Placement = pos=(89.5,4.5,68.5) rot=(0,0,1;0rad)
  Solid = false
  Source = -> Face042
  Symmetric = false
FEATURE [Part::Feature] Face043
  shape: bbox 3.2 x 1.5 x 2e-07 mm, 1 faces, 0 solids (baked)
FEATURE [Part::Revolution] Revolve047  label="frontCaseScrewRetainer002"
  Angle = 360
  Axis = (0,1,0)
  Base = (0,0,0)
  FaceMakerClass = Part::FaceMakerBullseye
  Placement = pos=(89.5,3,68.5) rot=(0,0,1;0rad)
  Solid = false
  Source = -> Face043
  Symmetric = false
FEATURE [Part::Feature] Face044
  shape: bbox 3.2 x 1.5 x 2e-07 mm, 1 faces, 0 solids (baked)
FEATURE [Part::Revolution] Revolve048  label="frontCaseScrewRetainer003"
  Angle = 360
  Axis = (0,1,0)
  Base = (0,0,0)
  FaceMakerClass = Part::FaceMakerBullseye
  Placement = pos=(89.5,3,3.5) rot=(0,0,1;0rad)
  Solid = false
  Source = -> Face044
  Symmetric = false
FEATURE [App::MeasureDistance] Distance002  label="Distance: 1.67 mm"
  Distance = 1.66921
  P1 = (99.2361,4.7524,71.7)
  P2 = (99.2347,6.42161,71.7)
FEATURE [Sketcher::SketchObject] Sketch018
  FullyConstrained = true
  sketch-geometry (7):
    g0: LineSegment StartX=0 StartY=0 StartZ=0 EndX=0 EndY=6 EndZ=0
    g1: Circle CenterX=0 CenterY=0 CenterZ=0 NormalX=0 NormalY=0 NormalZ=1 AngleXU=0 Radius=1
    g2: Circle CenterX=8 CenterY=6 CenterZ=0 NormalX=0 NormalY=0 NormalZ=1 AngleXU=0 Radius=1
    g3: BSplineCurve PolesCount=3 KnotsCount=2 Degree=2 IsPeriodic=0
    g4: GeomPoint X=0 Y=0 Z=0
    g5: GeomPoint X=8 Y=6 Z=0
    g6: LineSegment StartX=0 StartY=6 StartZ=0 EndX=8 EndY=6 EndZ=0
  constraints (14):
    c: Coincident(g0,g-1)
    c: Distance(g0) = 6
    c: Vertical(g0)
    c: Coincident(g3,g0)
    c: Weight(g1) = 1
    c: Equal(g1,g2)
    c: InternalAlignment(g1,g3)
    c: InternalAlignment(g2,g3)
    c: InternalAlignment(g4,g3)
    c: InternalAlignment(g5,g3)
    c: Block(g3)
    c: Coincident(g6,g0)
    c: Coincident(g6,g3)
    c: Horizontal(g6)
FEATURE [Part::Extrusion] Extrude012  label="caseScrewPillarBracket"
  Base = -> Sketch018
  Dir = (0,0,1)
  DirMode = 2
  FaceMakerClass = Part::FaceMakerBullseye
  LengthFwd = 2.4
  LengthRev = 0
  Placement = pos=(15.76,29,8.8) rot=(0,1,0;0rad)
  Solid = true
  Symmetric = false
FEATURE [Sketcher::SketchObject] Sketch019
  FullyConstrained = true
  sketch-geometry (7):
    g0: LineSegment StartX=0 StartY=0 StartZ=0 EndX=0 EndY=6 EndZ=0
    g1: Circle CenterX=0 CenterY=0 CenterZ=0 NormalX=0 NormalY=0 NormalZ=1 AngleXU=0 Radius=1
    g2: Circle CenterX=8 CenterY=6 CenterZ=0 NormalX=0 NormalY=0 NormalZ=1 AngleXU=0 Radius=1
    g3: BSplineCurve PolesCount=3 KnotsCount=2 Degree=2 IsPeriodic=0
    g4: GeomPoint X=0 Y=0 Z=0
    g5: GeomPoint X=8 Y=6 Z=0
    g6: LineSegment StartX=0 StartY=6 StartZ=0 EndX=8 EndY=6 EndZ=0
  constraints (14):
    c: Coincident(g0,g-1)
    c: Distance(g0) = 6
    c: Vertical(g0)
    c: Coincident(g3,g0)
    c: Weight(g1) = 1
    c: Equal(g1,g2)
    c: InternalAlignment(g1,g3)
    c: InternalAlignment(g2,g3)
    c: InternalAlignment(g4,g3)
    c: InternalAlignment(g5,g3)
    c: Block(g3)
    c: Coincident(g6,g0)
    c: Coincident(g6,g3)
    c: Horizontal(g6)
FEATURE [Part::Extrusion] Extrude013  label="caseScrewPillarBracket001"
  Base = -> Sketch019
  Dir = (0,0,1)
  DirMode = 2
  FaceMakerClass = Part::FaceMakerBullseye
  LengthFwd = 2.4
  LengthRev = 0
  Placement = pos=(15.76,29,60.8) rot=(0,0,1;0rad)
  Solid = true
  Symmetric = false
FEATURE [Sketcher::SketchObject] Sketch020
  FullyConstrained = true
  sketch-geometry (7):
    g0: LineSegment StartX=0 StartY=0 StartZ=0 EndX=0 EndY=6 EndZ=0
    g1: Circle CenterX=0 CenterY=0 CenterZ=0 NormalX=0 NormalY=0 NormalZ=1 AngleXU=0 Radius=1
    g2: Circle CenterX=8 CenterY=6 CenterZ=0 NormalX=0 NormalY=0 NormalZ=1 AngleXU=0 Radius=1
    g3: BSplineCurve PolesCount=3 KnotsCount=2 Degree=2 IsPeriodic=0
    g4: GeomPoint X=0 Y=0 Z=0
    g5: GeomPoint X=8 Y=6 Z=0
    g6: LineSegment StartX=0 StartY=6 StartZ=0 EndX=8 EndY=6 EndZ=0
  constraints (14):
    c: Coincident(g0,g-1)
    c: Distance(g0) = 6
    c: Vertical(g0)
    c: Coincident(g3,g0)
    c: Weight(g1) = 1
    c: Equal(g1,g2)
    c: InternalAlignment(g1,g3)
    c: InternalAlignment(g2,g3)
    c: InternalAlignment(g4,g3)
    c: InternalAlignment(g5,g3)
    c: Block(g3)
    c: Coincident(g6,g0)
    c: Coincident(g6,g3)
    c: Horizontal(g6)
FEATURE [Part::Extrusion] Extrude014  label="caseScrewPillarBracket002"
  Base = -> Sketch020
  Dir = (0,0,1)
  DirMode = 2
  FaceMakerClass = Part::FaceMakerBullseye
  LengthFwd = 2.4
  LengthRev = 0
  Placement = pos=(13.7,29,13.26) rot=(0,-1,0;1.5708rad)
  Solid = true
  Symmetric = false
FEATURE [Sketcher::SketchObject] Sketch021
  FullyConstrained = true
  sketch-geometry (7):
    g0: LineSegment StartX=0 StartY=0 StartZ=0 EndX=0 EndY=6 EndZ=0
    g1: Circle CenterX=0 CenterY=0 CenterZ=0 NormalX=0 NormalY=0 NormalZ=1 AngleXU=0 Radius=1
    g2: Circle CenterX=8 CenterY=6 CenterZ=0 NormalX=0 NormalY=0 NormalZ=1 AngleXU=0 Radius=1
    g3: BSplineCurve PolesCount=3 KnotsCount=2 Degree=2 IsPeriodic=0
    g4: GeomPoint X=0 Y=0 Z=0
    g5: GeomPoint X=8 Y=6 Z=0
    g6: LineSegment StartX=0 StartY=6 StartZ=0 EndX=8 EndY=6 EndZ=0
  constraints (14):
    c: Coincident(g0,g-1)
    c: Distance(g0) = 6
    c: Vertical(g0)
    c: Coincident(g3,g0)
    c: Weight(g1) = 1
    c: Equal(g1,g2)
    c: InternalAlignment(g1,g3)
    c: InternalAlignment(g2,g3)
    c: InternalAlignment(g4,g3)
    c: InternalAlignment(g5,g3)
    c: Block(g3)
    c: Coincident(g6,g0)
    c: Coincident(g6,g3)
    c: Horizontal(g6)
FEATURE [Part::Extrusion] Extrude015  label="caseScrewPillarBracket003"
  Base = -> Sketch021
  Dir = (0,0,1)
  DirMode = 2
  FaceMakerClass = Part::FaceMakerBullseye
  LengthFwd = 2.4
  LengthRev = 0
  Placement = pos=(11.3,29,58.74) rot=(0,1,0;1.5708rad)
  Solid = true
  Symmetric = false
FEATURE [Sketcher::SketchObject] Sketch022
  FullyConstrained = true
  sketch-geometry (7):
    g0: LineSegment StartX=0 StartY=0 StartZ=0 EndX=0 EndY=6 EndZ=0
    g1: Circle CenterX=0 CenterY=0 CenterZ=0 NormalX=0 NormalY=0 NormalZ=1 AngleXU=0 Radius=1
    g2: Circle CenterX=8 CenterY=6 CenterZ=0 NormalX=0 NormalY=0 NormalZ=1 AngleXU=0 Radius=1
    g3: BSplineCurve PolesCount=3 KnotsCount=2 Degree=2 IsPeriodic=0
    g4: GeomPoint X=0 Y=0 Z=0
    g5: GeomPoint X=8 Y=6 Z=0
    g6: LineSegment StartX=0 StartY=6 StartZ=0 EndX=8 EndY=6 EndZ=0
  constraints (14):
    c: Coincident(g0,g-1)
    c: Distance(g0) = 6
    c: Vertical(g0)
    c: Coincident(g3,g0)
    c: Weight(g1) = 1
    c: Equal(g1,g2)
    c: InternalAlignment(g1,g3)
    c: InternalAlignment(g2,g3)
    c: InternalAlignment(g4,g3)
    c: InternalAlignment(g5,g3)
    c: Block(g3)
    c: Coincident(g6,g0)
    c: Coincident(g6,g3)
    c: Horizontal(g6)
FEATURE [Part::Extrusion] Extrude016  label="caseScrewPillarBracket004"
  Base = -> Sketch022
  Dir = (0,0,1)
  DirMode = 2
  FaceMakerClass = Part::FaceMakerBullseye
  LengthFwd = 2.4
  LengthRev = 0
  Placement = pos=(88.3,29,65.23) rot=(0,1,0;1.5708rad)
  Solid = true
  Symmetric = false
FEATURE [Sketcher::SketchObject] Sketch023
  FullyConstrained = true
  sketch-geometry (7):
    g0: LineSegment StartX=0 StartY=0 StartZ=0 EndX=0 EndY=6 EndZ=0
    g1: Circle CenterX=0 CenterY=0 CenterZ=0 NormalX=0 NormalY=0 NormalZ=1 AngleXU=0 Radius=1
    g2: Circle CenterX=8 CenterY=6 CenterZ=0 NormalX=0 NormalY=0 NormalZ=1 AngleXU=0 Radius=1
    g3: BSplineCurve PolesCount=3 KnotsCount=2 Degree=2 IsPeriodic=0
    g4: GeomPoint X=0 Y=0 Z=0
    g5: GeomPoint X=8 Y=6 Z=0
    g6: LineSegment StartX=0 StartY=6 StartZ=0 EndX=8 EndY=6 EndZ=0
  constraints (14):
    c: Coincident(g0,g-1)
    c: Distance(g0) = 6
    c: Vertical(g0)
    c: Coincident(g3,g0)
    c: Weight(g1) = 1
    c: Equal(g1,g2)
    c: InternalAlignment(g1,g3)
    c: InternalAlignment(g2,g3)
    c: InternalAlignment(g4,g3)
    c: InternalAlignment(g5,g3)
    c: Block(g3)
    c: Coincident(g6,g0)
    c: Coincident(g6,g3)
    c: Horizontal(g6)
FEATURE [Part::Extrusion] Extrude017  label="caseScrewPillarBracket005"
  Base = -> Sketch023
  Dir = (0,0,1)
  DirMode = 2
  FaceMakerClass = Part::FaceMakerBullseye
  LengthFwd = 2.4
  LengthRev = 0
  Placement = pos=(90.7,29,6.77) rot=(0,-1,0;1.5708rad)
  Solid = true
  Symmetric = false
FEATURE [Sketcher::SketchObject] Sketch024
  FullyConstrained = true
  sketch-geometry (7):
    g0: LineSegment StartX=0 StartY=0 StartZ=0 EndX=0 EndY=6 EndZ=0
    g1: Circle CenterX=0 CenterY=0 CenterZ=0 NormalX=0 NormalY=0 NormalZ=1 AngleXU=0 Radius=1
    g2: Circle CenterX=8 CenterY=6 CenterZ=0 NormalX=0 NormalY=0 NormalZ=1 AngleXU=0 Radius=1
    g3: BSplineCurve PolesCount=3 KnotsCount=2 Degree=2 IsPeriodic=0
    g4: GeomPoint X=0 Y=0 Z=0
    g5: GeomPoint X=8 Y=6 Z=0
    g6: LineSegment StartX=0 StartY=6 StartZ=0 EndX=8 EndY=6 EndZ=0
  constraints (14):
    c: Coincident(g0,g-1)
    c: Distance(g0) = 6
    c: Vertical(g0)
    c: Coincident(g3,g0)
    c: Weight(g1) = 1
    c: Equal(g1,g2)
    c: InternalAlignment(g1,g3)
    c: InternalAlignment(g2,g3)
    c: InternalAlignment(g4,g3)
    c: InternalAlignment(g5,g3)
    c: Block(g3)
    c: Coincident(g6,g0)
    c: Coincident(g6,g3)
    c: Horizontal(g6)
FEATURE [Part::Extrusion] Extrude018  label="caseScrewPillarBracket006"
  Base = -> Sketch024
  Dir = (0,0,1)
  DirMode = 2
  FaceMakerClass = Part::FaceMakerBullseye
  LengthFwd = 2.4
  LengthRev = 0
  Placement = pos=(103.7,29,6.77) rot=(0,-1,0;1.5708rad)
  Solid = true
  Symmetric = false
FEATURE [Sketcher::SketchObject] Sketch025
  FullyConstrained = true
  sketch-geometry (7):
    g0: LineSegment StartX=0 StartY=0 StartZ=0 EndX=0 EndY=6 EndZ=0
    g1: Circle CenterX=0 CenterY=0 CenterZ=0 NormalX=0 NormalY=0 NormalZ=1 AngleXU=0 Radius=1
    g2: Circle CenterX=8 CenterY=6 CenterZ=0 NormalX=0 NormalY=0 NormalZ=1 AngleXU=0 Radius=1
    g3: BSplineCurve PolesCount=3 KnotsCount=2 Degree=2 IsPeriodic=0
    g4: GeomPoint X=0 Y=0 Z=0
    g5: GeomPoint X=8 Y=6 Z=0
    g6: LineSegment StartX=0 StartY=6 StartZ=0 EndX=8 EndY=6 EndZ=0
  constraints (14):
    c: Coincident(g0,g-1)
    c: Distance(g0) = 6
    c: Vertical(g0)
    c: Coincident(g3,g0)
    c: Weight(g1) = 1
    c: Equal(g1,g2)
    c: InternalAlignment(g1,g3)
    c: InternalAlignment(g2,g3)
    c: InternalAlignment(g4,g3)
    c: InternalAlignment(g5,g3)
    c: Block(g3)
    c: Coincident(g6,g0)
    c: Coincident(g6,g3)
    c: Horizontal(g6)
FEATURE [Part::Extrusion] Extrude019  label="caseScrewPillarBracket007"
  Base = -> Sketch025
  Dir = (0,0,1)
  DirMode = 2
  FaceMakerClass = Part::FaceMakerBullseye
  LengthFwd = 2.4
  LengthRev = 0
  Placement = pos=(101.3,29,65.23) rot=(0,1,0;1.5708rad)
  Solid = true
  Symmetric = false
FEATURE [Part::Box] Box011  label="frontCaseScrewPillarBracket"
  AttacherType = Attacher::AttachEngine3D
  Height = 2.4
  Length = 16
  Placement = pos=(87,28,2.3) rot=(0,0,1;0rad)
  Width = 7
FEATURE [Part::Box] Box012  label="frontCaseScrewPillarBracket001"
  AttacherType = Attacher::AttachEngine3D
  Height = 2.4
  Length = 16
  Placement = pos=(87,28,67.3) rot=(0,0,1;0rad)
  Width = 7
FEATURE [Sketcher::SketchObject] Sketch026
  FullyConstrained = true
  sketch-geometry (17):
    g0: Circle CenterX=-3.5 CenterY=23.5 CenterZ=0 NormalX=0 NormalY=0 NormalZ=1 AngleXU=0 Radius=1
    g1: Circle CenterX=-1 CenterY=15.25 CenterZ=0 NormalX=0 NormalY=0 NormalZ=1 AngleXU=0 Radius=1
    g2: Circle CenterX=-3.5 CenterY=7 CenterZ=0 NormalX=0 NormalY=0 NormalZ=1 AngleXU=0 Radius=1
    g3: BSplineCurve PolesCount=3 KnotsCount=2 Degree=2 IsPeriodic=0
    g4: GeomPoint X=-3.5 Y=23.5 Z=0
    g5: GeomPoint X=-3.5 Y=7 Z=0
    g6: Circle CenterX=-4.8 CenterY=30.5 CenterZ=0 NormalX=0 NormalY=0 NormalZ=1 AngleXU=0 Radius=1
    g7: Circle CenterX=-3.5 CenterY=30.5 CenterZ=0 NormalX=0 NormalY=0 NormalZ=1 AngleXU=0 Radius=1
    g8: Circle CenterX=-3.5 CenterY=29.2 CenterZ=0 NormalX=0 NormalY=0 NormalZ=1 AngleXU=0 Radius=1
    g9: BSplineCurve PolesCount=3 KnotsCount=2 Degree=2 IsPeriodic=0
    g10: GeomPoint X=-4.8 Y=30.5 Z=0
    g11: GeomPoint X=-3.5 Y=29.2 Z=0
    g12: LineSegment StartX=-3.5 StartY=29.2 StartZ=0 EndX=-3.5 EndY=23.5 EndZ=0
    g13: LineSegment StartX=-4.8 StartY=30.5 StartZ=0 EndX=0 EndY=30.5 EndZ=0
    g14: LineSegment StartX=-3.5 StartY=5 StartZ=0 EndX=-3.5 EndY=7 EndZ=0
    g15: LineSegment StartX=0 StartY=5 StartZ=0 EndX=0 EndY=30.5 EndZ=0
    g16: LineSegment StartX=-3.5 StartY=5 StartZ=0 EndX=0 EndY=5 EndZ=0
  constraints (33):
    c: Weight(g0) = 1
    c: Equal(g0,g1)
    c: Equal(g0,g2)
    c: InternalAlignment(g0,g3)
    c: InternalAlignment(g1,g3)
    c: InternalAlignment(g2,g3)
    c: InternalAlignment(g4,g3)
    c: InternalAlignment(g5,g3)
    c: Block(g3)
    c: Weight(g6) = 1
    c: Equal(g6,g7)
    c: Equal(g6,g8)
    c: InternalAlignment(g6,g9)
    c: InternalAlignment(g7,g9)
    c: InternalAlignment(g8,g9)
    c: InternalAlignment(g10,g9)
    c: InternalAlignment(g11,g9)
    c: Block(g9)
    c: Coincident(g12,g9)
    c: Coincident(g12,g3)
    c: Vertical(g12)
    c: Coincident(g13,g9)
    c: Horizontal(g13)
    c: Distance(g13) = 4.8
    c: Coincident(g14,g3)
    c: Vertical(g14)
    c: Coincident(g15,g13)
    c: Vertical(g15)
    c: Tangent(g15,g1)
    c: Distance(g14) = 2
    c: Coincident(g16,g14)
    c: Horizontal(g16)
    c: Coincident(g15,g16)
FEATURE [Part::Feature] Face050
  shape: bbox 4.8 x 25.5 x 2e-07 mm, 1 faces, 0 solids (baked)
FEATURE [Part::Revolution] Revolve054  label="moreFrontCaseScrewPost001"
  Angle = 360
  Axis = (0,1,0)
  Base = (0,0,0)
  FaceMakerClass = Part::FaceMakerBullseye
  Placement = pos=(102.5,4.5,3.5) rot=(0,0,1;0rad)
  Solid = false
  Source = -> Face050
  Symmetric = false
FEATURE [Part::Feature] Face051
  shape: bbox 4.8 x 25.5 x 2e-07 mm, 1 faces, 0 solids (baked)
FEATURE [Part::Revolution] Revolve055  label="moreFrontCaseScrewPost002"
  Angle = 360
  Axis = (0,1,0)
  Base = (0,0,0)
  FaceMakerClass = Part::FaceMakerBullseye
  Placement = pos=(102.5,4.5,68.5) rot=(0,0,1;0rad)
  Solid = false
  Source = -> Face051
  Symmetric = false
FEATURE [Sketcher::SketchObject] Sketch027
  FullyConstrained = true
  sketch-geometry (10):
    g0: LineSegment StartX=-1.6 StartY=4.7 StartZ=0 EndX=-1.6 EndY=1.7 EndZ=0
    g1: LineSegment StartX=-3.5 StartY=4.7 StartZ=0 EndX=-1.6 EndY=4.7 EndZ=0
    g2: LineSegment StartX=-1.6 StartY=1.7 StartZ=0 EndX=-1.6 EndY=1.5 EndZ=0
    g3: LineSegment StartX=-1.6 StartY=1.5 StartZ=0 EndX=-5.2 EndY=1.5 EndZ=0
    g4: Circle CenterX=-3.5 CenterY=4.7 CenterZ=0 NormalX=0 NormalY=0 NormalZ=1 AngleXU=0 Radius=1
    g5: Circle CenterX=-3.59627 CenterY=2.99743 CenterZ=0 NormalX=0 NormalY=0 NormalZ=1 AngleXU=0 Radius=1
    g6: Circle CenterX=-5.2 CenterY=1.5 CenterZ=0 NormalX=0 NormalY=0 NormalZ=1 AngleXU=0 Radius=1
    g7: BSplineCurve PolesCount=3 KnotsCount=2 Degree=2 IsPeriodic=0
    g8: GeomPoint X=-3.5 Y=4.7 Z=0
    g9: GeomPoint X=-5.2 Y=1.5 Z=0
  constraints (23):
    c: Vertical(g0)
    c: Distance(g0) = 3
    c: Coincident(g1,g0)
    c: Horizontal(g1)
    c: Block(g0)
    c: Block(g1)
    c: Coincident(g2,g0)
    c: Vertical(g2)
    c: Distance(g2) = 0.2
    c: Coincident(g3,g2)
    c: Horizontal(g3)
    c: Block(g3)
    c: Coincident(g7,g1)
    c: Weight(g4) = 1
    c: Equal(g4,g5)
    c: Equal(g4,g6)
    c: Coincident(g7,g3)
    c: InternalAlignment(g4,g7)
    c: InternalAlignment(g5,g7)
    c: InternalAlignment(g6,g7)
    c: InternalAlignment(g8,g7)
    c: InternalAlignment(g9,g7)
    c: Block(g7)
FEATURE [Sketcher::SketchObject] Sketch028
  FullyConstrained = true
  sketch-geometry (18):
    g0: LineSegment StartX=0 StartY=3e-16 StartZ=0 EndX=0 EndY=1.7 EndZ=0
    g1: LineSegment StartX=-3.5 StartY=0 StartZ=0 EndX=-3.5 EndY=0.9 EndZ=0
    g2: Circle CenterX=-2.7 CenterY=1.7 CenterZ=0 NormalX=0 NormalY=0 NormalZ=1 AngleXU=0 Radius=1
    g3: Circle CenterX=-3.5 CenterY=1.7 CenterZ=0 NormalX=0 NormalY=0 NormalZ=1 AngleXU=0 Radius=1
    g4: Circle CenterX=-3.5 CenterY=0.9 CenterZ=0 NormalX=0 NormalY=0 NormalZ=1 AngleXU=0 Radius=1
    g5: BSplineCurve PolesCount=3 KnotsCount=2 Degree=2 IsPeriodic=0
    g6: GeomPoint X=-2.7 Y=1.7 Z=0
    g7: GeomPoint X=-3.5 Y=0.9 Z=0
    g8: LineSegment StartX=-3.5 StartY=0 StartZ=0 EndX=-3.5 EndY=-7 EndZ=0
    g9: LineSegment StartX=0 StartY=3e-16 StartZ=0 EndX=0 EndY=-7 EndZ=0
    g10: LineSegment StartX=-3.5 StartY=-7 StartZ=0 EndX=0 EndY=-7 EndZ=0
    g11: LineSegment StartX=-2.7 StartY=1.7 StartZ=0 EndX=-1.6 EndY=1.7 EndZ=0
    g12: LineSegment StartX=0 StartY=1.7 StartZ=0 EndX=0 EndY=4.5 EndZ=0
    g13: LineSegment StartX=0 StartY=4.5 StartZ=0 EndX=0 EndY=10.8 EndZ=0
    g14: LineSegment StartX=0 StartY=10.8 StartZ=0 EndX=-2 EndY=10.8 EndZ=0
    g15: LineSegment StartX=-1.6 StartY=4.7 StartZ=0 EndX=-1.6 EndY=1.7 EndZ=0
    g16: LineSegment StartX=-1.6 StartY=4.7 StartZ=0 EndX=-2 EndY=4.7 EndZ=0
    g17: LineSegment StartX=-2 StartY=4.7 StartZ=0 EndX=-2 EndY=10.8 EndZ=0
  constraints (44):
    c: Vertical(g0)
    c: Vertical(g1)
    c: Distance(g1) = 0.9
    c: Block(g0)
    c: Distance(g0) = 1.7
    c: Weight(g2) = 1
    c: Equal(g2,g3)
    c: Equal(g2,g4)
    c: Coincident(g5,g1)
    c: InternalAlignment(g2,g5)
    c: InternalAlignment(g3,g5)
    c: InternalAlignment(g4,g5)
    c: InternalAlignment(g6,g5)
    c: InternalAlignment(g7,g5)
    c: Block(g5)
    c: Coincident(g8,g1)
    c: Vertical(g8)
    c: Distance(g8) = 7
    c: Vertical(g9)
    c: Equal(g8,g9) = 7
    c: Coincident(g9,g0)
    c: Coincident(g10,g8)
    c: Coincident(g10,g9)
    c: Horizontal(g10)
    c: Coincident(g11,g5)
    c: Horizontal(g11)
    c: Coincident(g12,g0)
    c: Vertical(g12)
    c: Distance(g12) = 2.8
    c: Coincident(g13,g12)
    c: Vertical(g13)
    c: Distance(g13) = 6.3
    c: Coincident(g14,g13)
    c: Horizontal(g14)
    c: Distance(g14) = 2
    c: Vertical(g15)
    c: Distance(g15) = 3
    c: Block(g11)
    c: Coincident(g15,g11)
    c: Coincident(g16,g15)
    c: Horizontal(g16)
    c: Coincident(g17,g16)
    c: Coincident(g17,g14)
    c: Vertical(g17)
FEATURE [Part::Revolution] Revolve040  label="backCaseScrewRetainer001"
  Angle = 360
  Axis = (0,1,0)
  Base = (0,0,0)
  FaceMakerClass = Part::FaceMakerBullseye
  Placement = pos=(12.5,3,10) rot=(0,0,1;0rad)
  Solid = false
  Source = -> Face036
  Symmetric = false
FEATURE [Part::Feature] Face055
  shape: bbox 3.5 x 30.2 x 2e-07 mm, 1 faces, 0 solids (baked)
FEATURE [Part::Revolution] Revolve059  label="backCaseScrewPost"
  Angle = 360
  Axis = (0,1,0)
  Base = (0,0,0)
  FaceMakerClass = Part::FaceMakerBullseye
  Placement = pos=(12.5,4.5,10) rot=(0,0,1;0rad)
  Solid = false
  Source = -> Face055
  Symmetric = false
FEATURE [Part::Feature] Face056
  shape: bbox 3.5 x 30.2 x 2e-07 mm, 1 faces, 0 solids (baked)
FEATURE [Part::Revolution] Revolve060  label="backCaseScrewPost001"
  Angle = 360
  Axis = (0,1,0)
  Base = (0,0,0)
  FaceMakerClass = Part::FaceMakerBullseye
  Placement = pos=(12.5,4.5,62) rot=(0,0,1;0rad)
  Solid = false
  Source = -> Face056
  Symmetric = false
FEATURE [Part::Feature] Face057
  shape: bbox 3.5 x 17.8 x 2e-07 mm, 1 faces, 0 solids (baked)
FEATURE [Part::Revolution] Revolve061  label="removeToCreateScrewAndThreadedInsertHole"
  Angle = 360
  Axis = (0,1,0)
  Base = (0,0,0)
  FaceMakerClass = Part::FaceMakerBullseye
  Placement = pos=(12.5,0,10) rot=(0,0,1;0rad)
  Solid = false
  Source = -> Face057
  Symmetric = false
FEATURE [Part::Feature] Face058
  shape: bbox 3.5 x 17.8 x 2e-07 mm, 1 faces, 0 solids (baked)
FEATURE [Part::Revolution] Revolve062  label="removeToCreateScrewAndThreadedInsertHole001"
  Angle = 360
  Axis = (0,1,0)
  Base = (0,0,0)
  FaceMakerClass = Part::FaceMakerBullseye
  Placement = pos=(12.5,0,62) rot=(0,0,1;0rad)
  Solid = false
  Source = -> Face058
  Symmetric = false
FEATURE [Part::Feature] Face059
  shape: bbox 3.5 x 17.8 x 2e-07 mm, 1 faces, 0 solids (baked)
FEATURE [Part::Revolution] Revolve063  label="removeToCreateScrewAndThreadedInsertHole002"
  Angle = 360
  Axis = (0,1,0)
  Base = (0,0,0)
  FaceMakerClass = Part::FaceMakerBullseye
  Placement = pos=(89.5,0,68.5) rot=(0,0,1;0rad)
  Solid = false
  Source = -> Face059
  Symmetric = false
FEATURE [Part::Feature] Face060
  shape: bbox 3.5 x 17.8 x 2e-07 mm, 1 faces, 0 solids (baked)
FEATURE [Part::Revolution] Revolve064  label="removeToCreateScrewAndThreadedInsertHole003"
  Angle = 360
  Axis = (0,1,0)
  Base = (0,0,0)
  FaceMakerClass = Part::FaceMakerBullseye
  Placement = pos=(89.5,0,3.5) rot=(0,0,1;0rad)
  Solid = false
  Source = -> Face060
  Symmetric = false
FEATURE [Part::Feature] Face061
  shape: bbox 3.5 x 17.8 x 2e-07 mm, 1 faces, 0 solids (baked)
FEATURE [Part::Revolution] Revolve065  label="removeToCreateScrewAndThreadedInsertHole004"
  Angle = 360
  Axis = (0,1,0)
  Base = (0,0,0)
  FaceMakerClass = Part::FaceMakerBullseye
  Placement = pos=(102.5,4.7,3.5) rot=(0,0,1;0rad)
  Solid = false
  Source = -> Face061
  Symmetric = false
FEATURE [Part::Feature] Face062
  shape: bbox 3.5 x 17.8 x 2e-07 mm, 1 faces, 0 solids (baked)
FEATURE [Part::Revolution] Revolve066  label="removeToCreateScrewAndThreadedInsertHole005"
  Angle = 360
  Axis = (0,1,0)
  Base = (0,0,0)
  FaceMakerClass = Part::FaceMakerBullseye
  Placement = pos=(102.5,4.7,68.5) rot=(0,0,1;0rad)
  Solid = false
  Source = -> Face062
  Symmetric = false
FEATURE [Part::MultiFuse] Fusion047  label="makeHoles"
  Shapes = -> [Revolve066,Revolve065,Revolve064,Revolve063,Revolve062,Revolve061]
FEATURE [Part::Feature] Face063
  shape: bbox 3.6 x 3.2 x 2e-07 mm, 1 faces, 0 solids (baked)
FEATURE [Part::Revolution] Revolve067  label="moreFrontCaseScrewRetainer002"
  Angle = 360
  Axis = (0,1,0)
  Base = (0,0,0)
  FaceMakerClass = Part::FaceMakerBullseye
  Placement = pos=(102.5,4.5,68.5) rot=(0,0,1;0rad)
  Solid = false
  Source = -> Face063
  Symmetric = false
FEATURE [Part::Feature] Face064
  shape: bbox 3.6 x 3.2 x 2e-07 mm, 1 faces, 0 solids (baked)
FEATURE [Part::Revolution] Revolve068  label="moreFrontCaseScrewRetainer003"
  Angle = 360
  Axis = (0,1,0)
  Base = (0,0,0)
  FaceMakerClass = Part::FaceMakerBullseye
  Placement = pos=(102.5,4.5,3.5) rot=(0,0,1;0rad)
  Solid = false
  Source = -> Face064
  Symmetric = false
FEATURE [Part::Feature] Face065
  shape: bbox 3.5 x 17.8 x 2e-07 mm, 1 faces, 0 solids (baked)
FEATURE [Part::Revolution] Revolve069  label="removeToCreateScrewAndThreadedInsertHole006"
  Angle = 360
  Axis = (0,1,0)
  Base = (0,0,0)
  FaceMakerClass = Part::FaceMakerBullseye
  Placement = pos=(12.5,0,10) rot=(0,0,1;0rad)
  Solid = false
  Source = -> Face065
  Symmetric = false
FEATURE [Part::Feature] Face066
  shape: bbox 3.5 x 17.8 x 2e-07 mm, 1 faces, 0 solids (baked)
FEATURE [Part::Revolution] Revolve070  label="removeToCreateScrewAndThreadedInsertHole007"
  Angle = 360
  Axis = (0,1,0)
  Base = (0,0,0)
  FaceMakerClass = Part::FaceMakerBullseye
  Placement = pos=(12.5,0,62) rot=(0,0,1;0rad)
  Solid = false
  Source = -> Face066
  Symmetric = false
FEATURE [Part::Feature] Face067
  shape: bbox 3.5 x 17.8 x 2e-07 mm, 1 faces, 0 solids (baked)
FEATURE [Part::Revolution] Revolve071  label="removeToCreateScrewAndThreadedInsertHole008"
  Angle = 360
  Axis = (0,1,0)
  Base = (0,0,0)
  FaceMakerClass = Part::FaceMakerBullseye
  Placement = pos=(89.5,0,68.5) rot=(0,0,1;0rad)
  Solid = false
  Source = -> Face067
  Symmetric = false
FEATURE [Part::Feature] Face068
  shape: bbox 3.5 x 17.8 x 2e-07 mm, 1 faces, 0 solids (baked)
FEATURE [Part::Revolution] Revolve072  label="removeToCreateScrewAndThreadedInsertHole009"
  Angle = 360
  Axis = (0,1,0)
  Base = (0,0,0)
  FaceMakerClass = Part::FaceMakerBullseye
  Placement = pos=(89.5,0,3.5) rot=(0,0,1;0rad)
  Solid = false
  Source = -> Face068
  Symmetric = false
FEATURE [Part::Feature] Face069
  shape: bbox 3.5 x 17.8 x 2e-07 mm, 1 faces, 0 solids (baked)
FEATURE [Part::Feature] Face070
  shape: bbox 3.5 x 17.8 x 2e-07 mm, 1 faces, 0 solids (baked)
FEATURE [Part::Revolution] Revolve073  label="removeToCreateScrewAndThreadedInsertHole010"
  Angle = 360
  Axis = (0,1,0)
  Base = (0,0,0)
  FaceMakerClass = Part::FaceMakerBullseye
  Placement = pos=(102.5,4.7,3.5) rot=(0,0,1;0rad)
  Solid = false
  Source = -> Face069
  Symmetric = false
FEATURE [Part::Revolution] Revolve074  label="removeToCreateScrewAndThreadedInsertHole011"
  Angle = 360
  Axis = (0,1,0)
  Base = (0,0,0)
  FaceMakerClass = Part::FaceMakerBullseye
  Placement = pos=(102.5,4.7,68.5) rot=(0,0,1;0rad)
  Solid = false
  Source = -> Face070
  Symmetric = false
FEATURE [Part::MultiFuse] Fusion048  label="makeHoles001"
  Shapes = -> [Revolve074,Revolve073,Revolve072,Revolve071,Revolve070,Revolve069]
FEATURE [Part::MultiFuse] Fusion049  label="caseScrewRetainers"
  Shapes = -> [Revolve067,Revolve068,Revolve048,Revolve047,Revolve039,Revolve040]
FEATURE [Part::Cut] Cut015  label="caseScrewRetainers001"
  Base = -> Fusion049
  Tool = -> Fusion048
FEATURE [Part::MultiFuse] Fusion050  label="casePillars"
  Shapes = -> [Revolve055,Revolve054,Revolve043,Revolve046,Revolve059,Revolve060]
FEATURE [Part::Feature] Face071 .. Face076  x6 (patterned run collapsed; names and placements below)
  shape: bbox 3.5 x 17.8 x 2e-07 mm, 1 faces, 0 solids (baked)
FEATURE [Part::Revolution] Revolve075  label="removeToCreateScrewAndThreadedInsertHole012"
  Angle = 360
  Axis = (0,1,0)
  Base = (0,0,0)
  FaceMakerClass = Part::FaceMakerBullseye
  Placement = pos=(12.5,0,10) rot=(0,0,1;0rad)
  Solid = false
  Source = -> Face071
  Symmetric = false
FEATURE [Part::Revolution] Revolve076  label="removeToCreateScrewAndThreadedInsertHole013"
  Angle = 360
  Axis = (0,1,0)
  Base = (0,0,0)
  FaceMakerClass = Part::FaceMakerBullseye
  Placement = pos=(12.5,0,62) rot=(0,0,1;0rad)
  Solid = false
  Source = -> Face072
  Symmetric = false
FEATURE [Part::Revolution] Revolve077  label="removeToCreateScrewAndThreadedInsertHole014"
  Angle = 360
  Axis = (0,1,0)
  Base = (0,0,0)
  FaceMakerClass = Part::FaceMakerBullseye
  Placement = pos=(89.5,0,68.5) rot=(0,0,1;0rad)
  Solid = false
  Source = -> Face073
  Symmetric = false
FEATURE [Part::Revolution] Revolve078  label="removeToCreateScrewAndThreadedInsertHole015"
  Angle = 360
  Axis = (0,1,0)
  Base = (0,0,0)
  FaceMakerClass = Part::FaceMakerBullseye
  Placement = pos=(89.5,0,3.5) rot=(0,0,1;0rad)
  Solid = false
  Source = -> Face074
  Symmetric = false
FEATURE [Part::Revolution] Revolve079  label="removeToCreateScrewAndThreadedInsertHole016"
  Angle = 360
  Axis = (0,1,0)
  Base = (0,0,0)
  FaceMakerClass = Part::FaceMakerBullseye
  Placement = pos=(102.5,4.7,3.5) rot=(0,0,1;0rad)
  Solid = false
  Source = -> Face075
  Symmetric = false
FEATURE [Part::Revolution] Revolve080  label="removeToCreateScrewAndThreadedInsertHole017"
  Angle = 360
  Axis = (0,1,0)
  Base = (0,0,0)
  FaceMakerClass = Part::FaceMakerBullseye
  Placement = pos=(102.5,4.7,68.5) rot=(0,0,1;0rad)
  Solid = false
  Source = -> Face076
  Symmetric = false
FEATURE [Part::MultiFuse] Fusion051  label="makeHoles002"
  Shapes = -> [Revolve080,Revolve079,Revolve078,Revolve077,Revolve076,Revolve075]
FEATURE [Part::Cut] Cut016  label="caesPillars"
  Base = -> Fusion050
  Tool = -> Fusion051
FEATURE [Part::Revolution] Revolve009  label="plugHousing016"
  Angle = 360
  Axis = (0,1,0)
  Base = (0,0,0)
  FaceMakerClass = Part::FaceMakerBullseye
  Placement = pos=(0,0,36.15) rot=(0,0,1;0rad)
  Solid = false
  Source = -> Face012
  Symmetric = false
FEATURE [Part::MultiFuse] Fusion014  label="plugHousing023"
  Placement = pos=(0,0,0) rot=(0,0,1;1.5708rad)
  Shapes = -> [Revolve011,Revolve009]
FEATURE [Part::Revolution] Revolve010  label="plugHousing017"
  Angle = 360
  Axis = (0,1,0)
  Base = (0,0,0)
  FaceMakerClass = Part::FaceMakerBullseye
  Placement = pos=(0,0,36.15) rot=(0,0,1;0rad)
  Solid = false
  Source = -> Face014
  Symmetric = false
FEATURE [Part::MultiFuse] Fusion015  label="plugHousing024"
  Placement = pos=(0,0,0) rot=(0,0,1;1.5708rad)
  Shapes = -> [Revolve010,Revolve015]
FEATURE [Part::Revolution] Revolve014  label="plugHousing026"
  Angle = 360
  Axis = (0,1,0)
  Base = (0,0,0)
  FaceMakerClass = Part::FaceMakerBullseye
  Placement = pos=(0,0,36.15) rot=(0,0,1;0rad)
  Solid = false
  Source = -> Face011
  Symmetric = false
FEATURE [Part::Revolution] Revolve013  label="plugHousing025"
  Angle = 360
  Axis = (0,1,0)
  Base = (0,0,0)
  FaceMakerClass = Part::FaceMakerBullseye
  Placement = pos=(0,0,36.15) rot=(0,0,1;0rad)
  Solid = false
  Source = -> Face015
  Symmetric = false
FEATURE [Part::MultiFuse] Fusion016  label="plugHousing028"
  Placement = pos=(0,19,0) rot=(0,0,1;3.14159rad)
  Shapes = -> [Fusion014,Fusion013]
FEATURE [Part::MultiFuse] Fusion011  label="plugHousing018"
  Placement = pos=(0,0,0) rot=(0,0,1;1.5708rad)
  Shapes = -> [Revolve014,Revolve013]
FEATURE [Part::MultiFuse] Fusion012  label="plugHousing019"
  Placement = pos=(0,19,0) rot=(0,0,1;3.14159rad)
  Shapes = -> [Fusion011,Fusion015]
FEATURE [Part::MultiFuse] Fusion017  label="plugHousing029"
  Placement = pos=(122.621,0,-0.15) rot=(0,0,1;0rad)
  Shapes = -> [Fusion016,Fusion012]
FEATURE [Part::MultiFuse] Fusion052  label="casePillarRetainers"
  Shapes = -> [Extrude012,Extrude013,Extrude014,Extrude015,Extrude016,Extrude017,Extrude018,Extrude019,Box011,Box012]
FEATURE [Part::Feature] Face077
  shape: bbox 3.5 x 17.8 x 2e-07 mm, 1 faces, 0 solids (baked)
FEATURE [Part::Revolution] Revolve081  label="removeToCreateScrewAndThreadedInsertHole018"
  Angle = 360
  Axis = (0,1,0)
  Base = (0,0,0)
  FaceMakerClass = Part::FaceMakerBullseye
  Placement = pos=(62.3,30.3,19.7) rot=(0,0,1;0rad)
  Solid = false
  Source = -> Face077
  Symmetric = false
FEATURE [Part::Feature] Face078
  shape: bbox 3.5 x 17.8 x 2e-07 mm, 1 faces, 0 solids (baked)
FEATURE [Part::Revolution] Revolve082  label="removeToCreateScrewAndThreadedInsertHole019"
  Angle = 360
  Axis = (0,1,0)
  Base = (0,0,0)
  FaceMakerClass = Part::FaceMakerBullseye
  Placement = pos=(62.3,30.3,51.7) rot=(0,0,1;0rad)
  Solid = false
  Source = -> Face078
  Symmetric = false
FEATURE [Part::Feature] Face079
  shape: bbox 3.5 x 17.8 x 2e-07 mm, 1 faces, 0 solids (baked)
FEATURE [Part::Revolution] Revolve083  label="removeToCreateScrewAndThreadedInsertHole020"
  Angle = 360
  Axis = (0,1,0)
  Base = (0,0,0)
  FaceMakerClass = Part::FaceMakerBullseye
  Placement = pos=(30.3,30.3,19.7) rot=(0,0,1;0rad)
  Solid = false
  Source = -> Face079
  Symmetric = false
FEATURE [Part::Feature] Face080
  shape: bbox 3.5 x 17.8 x 2e-07 mm, 1 faces, 0 solids (baked)
FEATURE [Part::Revolution] Revolve084  label="removeToCreateScrewAndThreadedInsertHole021"
  Angle = 360
  Axis = (0,1,0)
  Base = (0,0,0)
  FaceMakerClass = Part::FaceMakerBullseye
  Placement = pos=(30.3,30.3,51.7) rot=(0,0,1;0rad)
  Solid = false
  Source = -> Face080
  Symmetric = false
FEATURE [Part::MultiFuse] Fusion053  label="createThreadedInsertHolesForFan"
  Shapes = -> [Revolve081,Revolve082,Revolve083,Revolve084]
FEATURE [Part::Cut] Cut017  label="fanScrewHousing001"
  Base = -> Fusion046
  Tool = -> Fusion053
FEATURE [Part::Feature] Face081
  shape: bbox 3.5 x 17.8 x 2e-07 mm, 1 faces, 0 solids (baked)
FEATURE [Part::Revolution] Revolve085  label="removeToCreateScrewAndThreadedInsertHole022"
  Angle = 360
  Axis = (0,1,0)
  Base = (0,0,0)
  FaceMakerClass = Part::FaceMakerBullseye
  Placement = pos=(62.3,30.3,19.7) rot=(0,0,1;0rad)
  Solid = false
  Source = -> Face081
  Symmetric = false
FEATURE [Part::Feature] Face082
  shape: bbox 3.5 x 17.8 x 2e-07 mm, 1 faces, 0 solids (baked)
FEATURE [Part::Revolution] Revolve086  label="removeToCreateScrewAndThreadedInsertHole023"
  Angle = 360
  Axis = (0,1,0)
  Base = (0,0,0)
  FaceMakerClass = Part::FaceMakerBullseye
  Placement = pos=(62.3,30.3,51.7) rot=(0,0,1;0rad)
  Solid = false
  Source = -> Face082
  Symmetric = false
FEATURE [Part::Feature] Face083
  shape: bbox 3.5 x 17.8 x 2e-07 mm, 1 faces, 0 solids (baked)
FEATURE [Part::Revolution] Revolve087  label="removeToCreateScrewAndThreadedInsertHole024"
  Angle = 360
  Axis = (0,1,0)
  Base = (0,0,0)
  FaceMakerClass = Part::FaceMakerBullseye
  Placement = pos=(30.3,30.3,19.7) rot=(0,0,1;0rad)
  Solid = false
  Source = -> Face083
  Symmetric = false
FEATURE [Part::Feature] Face084
  shape: bbox 3.5 x 17.8 x 2e-07 mm, 1 faces, 0 solids (baked)
FEATURE [Part::Revolution] Revolve088  label="removeToCreateScrewAndThreadedInsertHole025"
  Angle = 360
  Axis = (0,1,0)
  Base = (0,0,0)
  FaceMakerClass = Part::FaceMakerBullseye
  Placement = pos=(30.3,30.3,51.7) rot=(0,0,1;0rad)
  Solid = false
  Source = -> Face084
  Symmetric = false
FEATURE [Part::MultiFuse] Fusion054  label="createThreadedInsertHolesForFan001"
  Shapes = -> [Revolve085,Revolve086,Revolve087,Revolve088]
FEATURE [Part::Cut] Cut018  label="top007"
  Base = -> Fusion040
  Tool = -> Fusion054
FEATURE [Sketcher::SketchObject] Sketch029
  FullyConstrained = false
  Placement = pos=(0,0,0) rot=(1,0,0;1.5708rad)
  sketch-geometry (24):
    g0: ArcOfCircle CenterX=-4 CenterY=-10.5 CenterZ=0 NormalX=0 NormalY=0 NormalZ=1 AngleXU=0 Radius=1.5 StartAngle=6e-16 EndAngle=3.14159
    g1: ArcOfCircle CenterX=-34.2 CenterY=-10.5 CenterZ=0 NormalX=0 NormalY=0 NormalZ=1 AngleXU=0 Radius=1.5 StartAngle=0 EndAngle=3.14159
    g2: ArcOfCircle CenterX=-34.2 CenterY=-27.7 CenterZ=0 NormalX=0 NormalY=0 NormalZ=1 AngleXU=0 Radius=1.5 StartAngle=3.14159 EndAngle=6.28319
    g3: ArcOfCircle CenterX=-4 CenterY=-27.7 CenterZ=0 NormalX=0 NormalY=0 NormalZ=1 AngleXU=0 Radius=1.5 StartAngle=3.1416 EndAngle=6.28319
    g4: ArcOfCircle CenterX=-10 CenterY=-4.3 CenterZ=0 NormalX=0 NormalY=0 NormalZ=1 AngleXU=0 Radius=1.5 StartAngle=2e-16 EndAngle=3.14159
    g5: ArcOfCircle CenterX=-16.1 CenterY=-1.8 CenterZ=0 NormalX=0 NormalY=0 NormalZ=1 AngleXU=0 Radius=1.5 StartAngle=5e-16 EndAngle=3.14159
    g6: ArcOfCircle CenterX=-22.1 CenterY=-1.8 CenterZ=0 NormalX=0 NormalY=0 NormalZ=1 AngleXU=0 Radius=1.5 StartAngle=5e-16 EndAngle=3.14159
    g7: ArcOfCircle CenterX=-28.2 CenterY=-4.3 CenterZ=0 NormalX=0 NormalY=0 NormalZ=1 AngleXU=0 Radius=1.5 StartAngle=2e-16 EndAngle=3.14159
    g8: ArcOfCircle CenterX=-10 CenterY=-33.9 CenterZ=0 NormalX=0 NormalY=0 NormalZ=1 AngleXU=0 Radius=1.5 StartAngle=3.14159 EndAngle=6.28319
    g9: ArcOfCircle CenterX=-16.1 CenterY=-36.4 CenterZ=0 NormalX=0 NormalY=0 NormalZ=1 AngleXU=0 Radius=1.5 StartAngle=3.14159 EndAngle=6.28319
    g10: ArcOfCircle CenterX=-22.1 CenterY=-36.4 CenterZ=0 NormalX=0 NormalY=0 NormalZ=1 AngleXU=0 Radius=1.5 StartAngle=3.14159 EndAngle=6.28319
    g11: ArcOfCircle CenterX=-28.2 CenterY=-33.9 CenterZ=0 NormalX=0 NormalY=0 NormalZ=1 AngleXU=0 Radius=1.5 StartAngle=3.14159 EndAngle=6.28319
    g12: LineSegment StartX=-35.7 StartY=-10.5 StartZ=0 EndX=-35.7 EndY=-27.7 EndZ=0
    g13: LineSegment StartX=-32.7 StartY=-10.5 StartZ=0 EndX=-32.7 EndY=-27.7 EndZ=0
    g14: LineSegment StartX=-29.7 StartY=-33.9 StartZ=0 EndX=-29.7 EndY=-4.3 EndZ=0
    g15: LineSegment StartX=-26.7 StartY=-33.9 StartZ=0 EndX=-26.7 EndY=-4.3 EndZ=0
    g16: LineSegment StartX=-2.5 StartY=-10.5 StartZ=0 EndX=-2.5 EndY=-27.7 EndZ=0
    g17: LineSegment StartX=-8.5 StartY=-4.3 StartZ=0 EndX=-8.5 EndY=-33.9 EndZ=0
    g18: LineSegment StartX=-5.5 StartY=-10.5 StartZ=0 EndX=-5.5 EndY=-27.7 EndZ=0
    g19: LineSegment StartX=-11.5 StartY=-4.3 StartZ=0 EndX=-11.5 EndY=-33.9 EndZ=0
    g20: LineSegment StartX=-14.6 StartY=-1.8 StartZ=0 EndX=-14.6 EndY=-36.4 EndZ=0
    g21: LineSegment StartX=-17.6 StartY=-1.8 StartZ=0 EndX=-17.6 EndY=-36.4 EndZ=0
    g22: LineSegment StartX=-20.6 StartY=-36.4 StartZ=0 EndX=-20.6 EndY=-1.8 EndZ=0
    g23: LineSegment StartX=-23.6 StartY=-1.8 StartZ=0 EndX=-23.6 EndY=-36.4 EndZ=0
  constraints (48):
    c: Block(g0)
    c: Block(g1)
    c: Block(g2)
    c: Block(g3)
    c: Block(g4)
    c: Block(g5)
    c: Block(g6)
    c: Block(g7)
    c: Block(g8)
    c: Block(g9)
    c: Block(g10)
    c: Block(g11)
    c: Coincident(g12,g1)
    c: Coincident(g12,g2)
    c: Vertical(g12)
    c: Coincident(g13,g1)
    c: Coincident(g13,g2)
    c: Vertical(g13)
    c: Coincident(g14,g11)
    c: Coincident(g14,g7)
    c: Vertical(g14)
    c: Coincident(g15,g11)
    c: Coincident(g15,g7)
    c: Vertical(g15)
    c: Coincident(g16,g0)
    c: Coincident(g16,g3)
    c: Vertical(g16)
    c: Coincident(g17,g4)
    c: Coincident(g17,g8)
    c: Vertical(g17)
    c: Coincident(g18,g0)
    c: Coincident(g18,g3)
    c: Vertical(g18)
    c: Coincident(g19,g4)
    c: Coincident(g19,g8)
    c: Vertical(g19)
    c: Coincident(g20,g5)
    c: Coincident(g20,g9)
    c: Vertical(g20)
    c: Coincident(g21,g5)
    c: Coincident(g21,g9)
    c: Vertical(g21)
    c: Coincident(g22,g10)
    c: Coincident(g22,g6)
    c: Vertical(g22)
    c: Coincident(g23,g6)
    c: Coincident(g23,g10)
    c: Vertical(g23)
FEATURE [Part::Extrusion] Extrude020  label="removeToCreateFanGrillHoles"
  Base = -> Sketch029
  Dir = (0,-1,6e-16)
  DirMode = 2
  FaceMakerClass = Part::FaceMakerBullseye
  LengthFwd = 10
  LengthRev = 0
  Placement = pos=(65.4,44,54.82) rot=(0,0,1;0rad)
  Solid = true
  Symmetric = false
FEATURE [Part::MultiFuse] Fusion055  label="top008"
  Shapes = -> [Cut017,Cut018]
FEATURE [Part::Cut] Cut019  label="top009"
  Base = -> Fusion055
  Tool = -> Extrude020
FEATURE [App::MeasureDistance] Distance003  label="Distance: 71.95 mm"
  Distance = 71.9513
  P1 = (117,38,72)
  P2 = (117,38,0.0487319)
FEATURE [Sketcher::SketchObject] Sketch030
  FullyConstrained = true
  Placement = pos=(117,19,0) rot=(0.57735,0.57735,0.57735;2.0944rad)
  sketch-geometry (48):
    g0: LineSegment StartX=-49.19 StartY=69.25 StartZ=0 EndX=-49.19 EndY=66.25 EndZ=0
    g1: LineSegment StartX=-49.19 StartY=63.5 StartZ=0 EndX=-49.19 EndY=60.5 EndZ=0
    g2: LineSegment StartX=-49.19 StartY=57.75 StartZ=0 EndX=-49.19 EndY=54.75 EndZ=0
    g3: LineSegment StartX=-49.19 StartY=52 StartZ=0 EndX=-49.19 EndY=49 EndZ=0
    g4: LineSegment StartX=-49.19 StartY=46.25 StartZ=0 EndX=-49.19 EndY=43.25 EndZ=0
    g5: LineSegment StartX=-49.19 StartY=40.5 StartZ=0 EndX=-49.19 EndY=37.5 EndZ=0
    g6: LineSegment StartX=-49.19 StartY=34.5 StartZ=0 EndX=-49.19 EndY=31.5 EndZ=0
    g7: LineSegment StartX=-49.19 StartY=28.75 StartZ=0 EndX=-49.19 EndY=25.75 EndZ=0
    g8: LineSegment StartX=-49.19 StartY=23 StartZ=0 EndX=-49.19 EndY=20 EndZ=0
    g9: LineSegment StartX=-49.19 StartY=17.25 StartZ=0 EndX=-49.19 EndY=14.25 EndZ=0
    g10: LineSegment StartX=-49.19 StartY=11.5 StartZ=0 EndX=-49.19 EndY=8.5 EndZ=0
    g11: LineSegment StartX=-49.19 StartY=5.75 StartZ=0 EndX=-49.19 EndY=2.75 EndZ=0
    g12: ArcOfCircle CenterX=-1.5 CenterY=67.75 CenterZ=0 NormalX=0 NormalY=0 NormalZ=1 AngleXU=0 Radius=1.5 StartAngle=4.71239 EndAngle=7.85398
    g13: ArcOfCircle CenterX=-1.5 CenterY=62 CenterZ=0 NormalX=0 NormalY=0 NormalZ=1 AngleXU=0 Radius=1.5 StartAngle=4.71239 EndAngle=7.85398
    g14: ArcOfCircle CenterX=-1.5 CenterY=56.25 CenterZ=0 NormalX=0 NormalY=0 NormalZ=1 AngleXU=0 Radius=1.5 StartAngle=4.71239 EndAngle=7.85398
    g15: ArcOfCircle CenterX=-11.49 CenterY=50.5 CenterZ=0 NormalX=0 NormalY=0 NormalZ=1 AngleXU=0 Radius=1.5 StartAngle=4.71239 EndAngle=7.85398
    g16: ArcOfCircle CenterX=-16.28 CenterY=44.75 CenterZ=0 NormalX=0 NormalY=0 NormalZ=1 AngleXU=0 Radius=1.5 StartAngle=4.71239 EndAngle=7.85398
    g17: ArcOfCircle CenterX=-18.2337 CenterY=39 CenterZ=0 NormalX=0 NormalY=0 NormalZ=1 AngleXU=0 Radius=1.5 StartAngle=4.71485 EndAngle=7.85398
    g18: ArcOfCircle CenterX=-16.2837 CenterY=27.25 CenterZ=0 NormalX=0 NormalY=0 NormalZ=1 AngleXU=0 Radius=1.5 StartAngle=4.71485 EndAngle=7.85398
    g19: ArcOfCircle CenterX=-18.2337 CenterY=33 CenterZ=0 NormalX=0 NormalY=0 NormalZ=1 AngleXU=0 Radius=1.5 StartAngle=4.71485 EndAngle=7.85398
    g20: ArcOfCircle CenterX=-11.49 CenterY=21.5 CenterZ=0 NormalX=0 NormalY=0 NormalZ=1 AngleXU=0 Radius=1.5 StartAngle=4.71239 EndAngle=7.85398
    g21: ArcOfCircle CenterX=-1.5 CenterY=4.25 CenterZ=0 NormalX=0 NormalY=0 NormalZ=1 AngleXU=0 Radius=1.5 StartAngle=4.71239 EndAngle=7.85398
    g22: ArcOfCircle CenterX=-1.5 CenterY=10 CenterZ=0 NormalX=0 NormalY=0 NormalZ=1 AngleXU=0 Radius=1.5 StartAngle=4.71239 EndAngle=7.85398
    g23: ArcOfCircle CenterX=-1.5 CenterY=15.75 CenterZ=0 NormalX=0 NormalY=0 NormalZ=1 AngleXU=0 Radius=1.5 StartAngle=4.71239 EndAngle=7.85398
    g24: LineSegment StartX=-49.19 StartY=69.25 StartZ=0 EndX=-1.5 EndY=69.25 EndZ=0
    g25: LineSegment StartX=-49.19 StartY=66.25 StartZ=0 EndX=-1.5 EndY=66.25 EndZ=0
    g26: LineSegment StartX=-49.19 StartY=63.5 StartZ=0 EndX=-1.5 EndY=63.5 EndZ=0
    g27: LineSegment StartX=-49.19 StartY=60.5 StartZ=0 EndX=-1.5 EndY=60.5 EndZ=0
    g28: LineSegment StartX=-49.19 StartY=57.75 StartZ=0 EndX=-1.5 EndY=57.75 EndZ=0
    g29: LineSegment StartX=-49.19 StartY=54.75 StartZ=0 EndX=-1.5 EndY=54.75 EndZ=0
    g30: LineSegment StartX=-49.19 StartY=52 StartZ=0 EndX=-11.49 EndY=52 EndZ=0
    g31: LineSegment StartX=-49.19 StartY=49 StartZ=0 EndX=-11.49 EndY=49 EndZ=0
    g32: LineSegment StartX=-49.19 StartY=46.25 StartZ=0 EndX=-16.28 EndY=46.25 EndZ=0
    g33: LineSegment StartX=-49.19 StartY=43.25 StartZ=0 EndX=-16.28 EndY=43.25 EndZ=0
    g34: LineSegment StartX=-49.19 StartY=40.5 StartZ=0 EndX=-18.2337 EndY=40.5 EndZ=0
    g35: LineSegment StartX=-49.19 StartY=37.5 StartZ=0 EndX=-18.23 EndY=37.5 EndZ=0
    g36: LineSegment StartX=-49.19 StartY=34.5 StartZ=0 EndX=-18.2337 EndY=34.5 EndZ=0
    g37: LineSegment StartX=-49.19 StartY=31.5 StartZ=0 EndX=-18.23 EndY=31.5 EndZ=0
    g38: LineSegment StartX=-49.19 StartY=28.75 StartZ=0 EndX=-16.2837 EndY=28.75 EndZ=0
    g39: LineSegment StartX=-49.19 StartY=25.75 StartZ=0 EndX=-16.28 EndY=25.75 EndZ=0
    g40: LineSegment StartX=-49.19 StartY=23 StartZ=0 EndX=-11.49 EndY=23 EndZ=0
    g41: LineSegment StartX=-49.19 StartY=20 StartZ=0 EndX=-11.49 EndY=20 EndZ=0
    g42: LineSegment StartX=-49.19 StartY=17.25 StartZ=0 EndX=-1.5 EndY=17.25 EndZ=0
    g43: LineSegment StartX=-49.19 StartY=14.25 StartZ=0 EndX=-1.5 EndY=14.25 EndZ=0
    g44: LineSegment StartX=-49.19 StartY=11.5 StartZ=0 EndX=-1.5 EndY=11.5 EndZ=0
    g45: LineSegment StartX=-49.19 StartY=8.5 StartZ=0 EndX=-1.5 EndY=8.5 EndZ=0
    g46: LineSegment StartX=-49.19 StartY=5.75 StartZ=0 EndX=-1.5 EndY=5.75 EndZ=0
    g47: LineSegment StartX=-49.19 StartY=2.75 StartZ=0 EndX=-1.5 EndY=2.75 EndZ=0
  constraints (120):
    c: Vertical(g0)
    c: Distance(g0) = 3
    c: Block(g0)
    c: Vertical(g1)
    c: Distance(g1) = 3
    c: Vertical(g2)
    c: Equal(g0,g2) = 3
    c: Block(g2)
    c: Vertical(g3)
    c: Equal(g1,g3) = 3
    c: Vertical(g4)
    c: Equal(g0,g4) = 3
    c: Block(g4)
    c: Vertical(g5)
    c: Equal(g1,g5) = 3
    c: Vertical(g6)
    c: Equal(g0,g6) = 3
    c: Block(g6)
    c: Vertical(g7)
    c: Equal(g1,g7) = 3
    c: Vertical(g8)
    c: Equal(g0,g8) = 3
    c: Block(g8)
    c: Vertical(g9)
    c: Equal(g1,g9) = 3
    c: Vertical(g10)
    c: Equal(g0,g10) = 3
    c: Block(g10)
    c: Vertical(g11)
    c: Equal(g1,g11) = 3
    c: Block(g12)
    c: Block(g13)
    c: Block(g14)
    c: Block(g15)
    c: Block(g16)
    c: Block(g17)
    c: Block(g18)
    c: Block(g19)
    c: Block(g20)
    c: Block(g21)
    c: Block(g22)
    c: Block(g23)
    c: Block(g11)
    c: Block(g9)
    c: Block(g7)
    c: Block(g5)
    c: Block(g3)
    c: Block(g1)
    c: Coincident(g24,g0)
    c: Coincident(g24,g12)
    c: Horizontal(g24)
    c: Coincident(g25,g0)
    c: Coincident(g25,g12)
    c: Horizontal(g25)
    c: Coincident(g26,g1)
    c: Coincident(g26,g13)
    c: Horizontal(g26)
    c: Coincident(g27,g1)
    c: Coincident(g27,g13)
    c: Horizontal(g27)
    c: Coincident(g28,g2)
    c: Coincident(g28,g14)
    c: Horizontal(g28)
    c: Coincident(g29,g2)
    c: Coincident(g29,g14)
    c: Horizontal(g29)
    c: Coincident(g30,g3)
    c: Coincident(g30,g15)
    c: Horizontal(g30)
    c: Coincident(g31,g3)
    c: Coincident(g31,g15)
    c: Horizontal(g31)
    c: Coincident(g32,g4)
    c: Coincident(g32,g16)
    c: Horizontal(g32)
    c: Coincident(g33,g4)
    c: Coincident(g33,g16)
    c: Horizontal(g33)
    c: Coincident(g34,g5)
    c: Coincident(g34,g17)
    c: Horizontal(g34)
    c: Coincident(g35,g5)
    c: Coincident(g35,g17)
    c: Horizontal(g35)
    c: Coincident(g36,g6)
    c: Coincident(g36,g19)
    c: Horizontal(g36)
    c: Coincident(g37,g6)
    c: Coincident(g37,g19)
    c: Horizontal(g37)
    c: Coincident(g38,g7)
    c: Coincident(g38,g18)
    c: Horizontal(g38)
    c: Coincident(g39,g7)
    c: Coincident(g39,g18)
    c: Horizontal(g39)
    c: Coincident(g40,g8)
    c: Coincident(g40,g20)
    c: Horizontal(g40)
    c: Coincident(g41,g8)
    c: Coincident(g41,g20)
    c: Horizontal(g41)
    c: Coincident(g42,g9)
    c: Coincident(g42,g23)
    c: Horizontal(g42)
    c: Coincident(g43,g9)
    c: Coincident(g43,g23)
    c: Horizontal(g43)
    c: Coincident(g44,g10)
    c: Coincident(g44,g22)
    c: Horizontal(g44)
    c: Coincident(g45,g10)
    c: Coincident(g45,g22)
    c: Horizontal(g45)
    c: Coincident(g46,g11)
    c: Coincident(g46,g21)
    c: Horizontal(g46)
    c: Coincident(g47,g11)
    c: Coincident(g47,g21)
    c: Horizontal(g47)
FEATURE [Sketcher::SketchObject] Sketch031
  FullyConstrained = true
  Placement = pos=(117,19,0) rot=(0.57735,0.57735,0.57735;2.0944rad)
  sketch-geometry (24):
    g0: ArcOfCircle CenterX=-49.19 CenterY=67.75 CenterZ=0 NormalX=0 NormalY=0 NormalZ=1 AngleXU=0 Radius=1.5 StartAngle=1.5708 EndAngle=4.71239
    g1: ArcOfCircle CenterX=-49.19 CenterY=62 CenterZ=0 NormalX=0 NormalY=0 NormalZ=1 AngleXU=0 Radius=1.5 StartAngle=1.5708 EndAngle=4.71239
    g2: ArcOfCircle CenterX=-49.19 CenterY=56.25 CenterZ=0 NormalX=0 NormalY=0 NormalZ=1 AngleXU=0 Radius=1.5 StartAngle=1.5708 EndAngle=4.71239
    g3: ArcOfCircle CenterX=-49.19 CenterY=50.5 CenterZ=0 NormalX=0 NormalY=0 NormalZ=1 AngleXU=0 Radius=1.5 StartAngle=1.5708 EndAngle=4.71239
    g4: ArcOfCircle CenterX=-49.19 CenterY=44.75 CenterZ=0 NormalX=0 NormalY=0 NormalZ=1 AngleXU=0 Radius=1.5 StartAngle=1.5708 EndAngle=4.71239
    g5: ArcOfCircle CenterX=-49.19 CenterY=39 CenterZ=0 NormalX=0 NormalY=0 NormalZ=1 AngleXU=0 Radius=1.5 StartAngle=1.5708 EndAngle=4.71239
    g6: ArcOfCircle CenterX=-49.19 CenterY=33 CenterZ=0 NormalX=0 NormalY=0 NormalZ=1 AngleXU=0 Radius=1.5 StartAngle=1.5708 EndAngle=4.71239
    g7: ArcOfCircle CenterX=-49.19 CenterY=27.25 CenterZ=0 NormalX=0 NormalY=0 NormalZ=1 AngleXU=0 Radius=1.5 StartAngle=1.5708 EndAngle=4.71239
    g8: ArcOfCircle CenterX=-49.19 CenterY=21.5 CenterZ=0 NormalX=0 NormalY=0 NormalZ=1 AngleXU=0 Radius=1.5 StartAngle=1.5708 EndAngle=4.71239
    g9: ArcOfCircle CenterX=-49.19 CenterY=15.75 CenterZ=0 NormalX=0 NormalY=0 NormalZ=1 AngleXU=0 Radius=1.5 StartAngle=1.5708 EndAngle=4.71239
    g10: ArcOfCircle CenterX=-49.19 CenterY=10 CenterZ=0 NormalX=0 NormalY=0 NormalZ=1 AngleXU=0 Radius=1.5 StartAngle=1.5708 EndAngle=4.71239
    g11: ArcOfCircle CenterX=-49.19 CenterY=4.25 CenterZ=0 NormalX=0 NormalY=0 NormalZ=1 AngleXU=0 Radius=1.5 StartAngle=1.5708 EndAngle=4.71239
    g12: LineSegment StartX=-49.19 StartY=69.25 StartZ=0 EndX=-49.19 EndY=66.25 EndZ=0
    g13: LineSegment StartX=-49.19 StartY=63.5 StartZ=0 EndX=-49.19 EndY=60.5 EndZ=0
    g14: LineSegment StartX=-49.19 StartY=57.75 StartZ=0 EndX=-49.19 EndY=54.75 EndZ=0
    g15: LineSegment StartX=-49.19 StartY=52 StartZ=0 EndX=-49.19 EndY=49 EndZ=0
    g16: LineSegment StartX=-49.19 StartY=46.25 StartZ=0 EndX=-49.19 EndY=43.25 EndZ=0
    g17: LineSegment StartX=-49.19 StartY=40.5 StartZ=0 EndX=-49.19 EndY=37.5 EndZ=0
    g18: LineSegment StartX=-49.19 StartY=34.5 StartZ=0 EndX=-49.19 EndY=31.5 EndZ=0
    g19: LineSegment StartX=-49.19 StartY=28.75 StartZ=0 EndX=-49.19 EndY=25.75 EndZ=0
    g20: LineSegment StartX=-49.19 StartY=23 StartZ=0 EndX=-49.19 EndY=20 EndZ=0
    g21: LineSegment StartX=-49.19 StartY=17.25 StartZ=0 EndX=-49.19 EndY=14.25 EndZ=0
    g22: LineSegment StartX=-49.19 StartY=11.5 StartZ=0 EndX=-49.19 EndY=8.5 EndZ=0
    g23: LineSegment StartX=-49.19 StartY=5.75 StartZ=0 EndX=-49.19 EndY=2.75 EndZ=0
  constraints (48):
    c: Block(g0)
    c: Block(g1)
    c: Block(g2)
    c: Block(g3)
    c: Block(g4)
    c: Block(g5)
    c: Block(g6)
    c: Block(g7)
    c: Block(g8)
    c: Block(g9)
    c: Block(g10)
    c: Block(g11)
    c: Coincident(g12,g0)
    c: Coincident(g12,g0)
    c: Vertical(g12)
    c: Vertical(g13)
    c: Coincident(g13,g1)
    c: Vertical(g14)
    c: Coincident(g14,g2)
    c: Vertical(g15)
    c: Coincident(g15,g3)
    c: Vertical(g16)
    c: Coincident(g16,g4)
    c: Vertical(g17)
    c: Coincident(g17,g5)
    c: Vertical(g18)
    c: Coincident(g18,g6)
    c: Vertical(g19)
    c: Coincident(g19,g7)
    c: Vertical(g20)
    c: Coincident(g20,g8)
    c: Vertical(g21)
    c: Coincident(g21,g9)
    c: Vertical(g22)
    c: Coincident(g22,g10)
    c: Vertical(g23)
    c: Coincident(g23,g11)
    c: Block(g23)
    c: Block(g22)
    c: Block(g21)
    c: Block(g20)
    c: Block(g13)
    c: Block(g14)
    c: Block(g15)
    c: Block(g16)
    c: Block(g17)
    c: Block(g18)
    c: Block(g19)
FEATURE [Part::Extrusion] Extrude022
  Base = -> Sketch030
  Dir = (1,-2e-16,2e-16)
  DirMode = 2
  FaceMakerClass = Part::FaceMakerBullseye
  LengthFwd = 19
  LengthRev = 0
  Placement = pos=(-19,0,0) rot=(0,0,1;0rad)
  Solid = true
  Symmetric = false
FEATURE [Part::Fillet] Fillet022
  Base = -> Extrude022
  Edges = 24 edges r=1.49: [Edge6,Edge11,Edge18,Edge23,Edge30,Edge35,Edge42,Edge47,Edge54,Edge59,Edge66,Edge71,Edge78,Edge83,Edge90,Edge95,Edge102,Edge107,Edge114,Edge119,Edge126,Edge131,Edge138,Edge143]
FEATURE [Part::Cut] Cut020  label="top010"
  Base = -> Cut019
  Tool = -> Fillet022
FEATURE [Sketcher::SketchObject] Sketch032
  FullyConstrained = true
  Placement = pos=(117,19,0) rot=(0.57735,0.57735,0.57735;2.0944rad)
  sketch-geometry (48):
    g0: LineSegment StartX=-49.19 StartY=69.25 StartZ=0 EndX=-49.19 EndY=66.25 EndZ=0
    g1: LineSegment StartX=-49.19 StartY=63.5 StartZ=0 EndX=-49.19 EndY=60.5 EndZ=0
    g2: LineSegment StartX=-49.19 StartY=57.75 StartZ=0 EndX=-49.19 EndY=54.75 EndZ=0
    g3: LineSegment StartX=-49.19 StartY=52 StartZ=0 EndX=-49.19 EndY=49 EndZ=0
    g4: LineSegment StartX=-49.19 StartY=46.25 StartZ=0 EndX=-49.19 EndY=43.25 EndZ=0
    g5: LineSegment StartX=-49.19 StartY=40.5 StartZ=0 EndX=-49.19 EndY=37.5 EndZ=0
    g6: LineSegment StartX=-49.19 StartY=34.5 StartZ=0 EndX=-49.19 EndY=31.5 EndZ=0
    g7: LineSegment StartX=-49.19 StartY=28.75 StartZ=0 EndX=-49.19 EndY=25.75 EndZ=0
    g8: LineSegment StartX=-49.19 StartY=23 StartZ=0 EndX=-49.19 EndY=20 EndZ=0
    g9: LineSegment StartX=-49.19 StartY=17.25 StartZ=0 EndX=-49.19 EndY=14.25 EndZ=0
    g10: LineSegment StartX=-49.19 StartY=11.5 StartZ=0 EndX=-49.19 EndY=8.5 EndZ=0
    g11: LineSegment StartX=-49.19 StartY=5.75 StartZ=0 EndX=-49.19 EndY=2.75 EndZ=0
    g12: ArcOfCircle CenterX=-1.5 CenterY=67.75 CenterZ=0 NormalX=0 NormalY=0 NormalZ=1 AngleXU=0 Radius=1.5 StartAngle=4.71239 EndAngle=7.85398
    g13: ArcOfCircle CenterX=-1.5 CenterY=62 CenterZ=0 NormalX=0 NormalY=0 NormalZ=1 AngleXU=0 Radius=1.5 StartAngle=4.71239 EndAngle=7.85398
    g14: ArcOfCircle CenterX=-1.5 CenterY=56.25 CenterZ=0 NormalX=0 NormalY=0 NormalZ=1 AngleXU=0 Radius=1.5 StartAngle=4.71239 EndAngle=7.85398
    g15: ArcOfCircle CenterX=-11.49 CenterY=50.5 CenterZ=0 NormalX=0 NormalY=0 NormalZ=1 AngleXU=0 Radius=1.5 StartAngle=4.71239 EndAngle=7.85398
    g16: ArcOfCircle CenterX=-16.28 CenterY=44.75 CenterZ=0 NormalX=0 NormalY=0 NormalZ=1 AngleXU=0 Radius=1.5 StartAngle=4.71239 EndAngle=7.85398
    g17: ArcOfCircle CenterX=-18.2337 CenterY=39 CenterZ=0 NormalX=0 NormalY=0 NormalZ=1 AngleXU=0 Radius=1.5 StartAngle=4.71485 EndAngle=7.85398
    g18: ArcOfCircle CenterX=-16.2837 CenterY=27.25 CenterZ=0 NormalX=0 NormalY=0 NormalZ=1 AngleXU=0 Radius=1.5 StartAngle=4.71485 EndAngle=7.85398
    g19: ArcOfCircle CenterX=-18.2337 CenterY=33 CenterZ=0 NormalX=0 NormalY=0 NormalZ=1 AngleXU=0 Radius=1.5 StartAngle=4.71485 EndAngle=7.85398
    g20: ArcOfCircle CenterX=-11.49 CenterY=21.5 CenterZ=0 NormalX=0 NormalY=0 NormalZ=1 AngleXU=0 Radius=1.5 StartAngle=4.71239 EndAngle=7.85398
    g21: ArcOfCircle CenterX=-1.5 CenterY=4.25 CenterZ=0 NormalX=0 NormalY=0 NormalZ=1 AngleXU=0 Radius=1.5 StartAngle=4.71239 EndAngle=7.85398
    g22: ArcOfCircle CenterX=-1.5 CenterY=10 CenterZ=0 NormalX=0 NormalY=0 NormalZ=1 AngleXU=0 Radius=1.5 StartAngle=4.71239 EndAngle=7.85398
    g23: ArcOfCircle CenterX=-1.5 CenterY=15.75 CenterZ=0 NormalX=0 NormalY=0 NormalZ=1 AngleXU=0 Radius=1.5 StartAngle=4.71239 EndAngle=7.85398
    g24: LineSegment StartX=-49.19 StartY=69.25 StartZ=0 EndX=-1.5 EndY=69.25 EndZ=0
    g25: LineSegment StartX=-49.19 StartY=66.25 StartZ=0 EndX=-1.5 EndY=66.25 EndZ=0
    g26: LineSegment StartX=-49.19 StartY=63.5 StartZ=0 EndX=-1.5 EndY=63.5 EndZ=0
    g27: LineSegment StartX=-49.19 StartY=60.5 StartZ=0 EndX=-1.5 EndY=60.5 EndZ=0
    g28: LineSegment StartX=-49.19 StartY=57.75 StartZ=0 EndX=-1.5 EndY=57.75 EndZ=0
    g29: LineSegment StartX=-49.19 StartY=54.75 StartZ=0 EndX=-1.5 EndY=54.75 EndZ=0
    g30: LineSegment StartX=-49.19 StartY=52 StartZ=0 EndX=-11.49 EndY=52 EndZ=0
    g31: LineSegment StartX=-49.19 StartY=49 StartZ=0 EndX=-11.49 EndY=49 EndZ=0
    g32: LineSegment StartX=-49.19 StartY=46.25 StartZ=0 EndX=-16.28 EndY=46.25 EndZ=0
    g33: LineSegment StartX=-49.19 StartY=43.25 StartZ=0 EndX=-16.28 EndY=43.25 EndZ=0
    g34: LineSegment StartX=-49.19 StartY=40.5 StartZ=0 EndX=-18.2337 EndY=40.5 EndZ=0
    g35: LineSegment StartX=-49.19 StartY=37.5 StartZ=0 EndX=-18.23 EndY=37.5 EndZ=0
    g36: LineSegment StartX=-49.19 StartY=34.5 StartZ=0 EndX=-18.2337 EndY=34.5 EndZ=0
    g37: LineSegment StartX=-49.19 StartY=31.5 StartZ=0 EndX=-18.23 EndY=31.5 EndZ=0
    g38: LineSegment StartX=-49.19 StartY=28.75 StartZ=0 EndX=-16.2837 EndY=28.75 EndZ=0
    g39: LineSegment StartX=-49.19 StartY=25.75 StartZ=0 EndX=-16.28 EndY=25.75 EndZ=0
    g40: LineSegment StartX=-49.19 StartY=23 StartZ=0 EndX=-11.49 EndY=23 EndZ=0
    g41: LineSegment StartX=-49.19 StartY=20 StartZ=0 EndX=-11.49 EndY=20 EndZ=0
    g42: LineSegment StartX=-49.19 StartY=17.25 StartZ=0 EndX=-1.5 EndY=17.25 EndZ=0
    g43: LineSegment StartX=-49.19 StartY=14.25 StartZ=0 EndX=-1.5 EndY=14.25 EndZ=0
    g44: LineSegment StartX=-49.19 StartY=11.5 StartZ=0 EndX=-1.5 EndY=11.5 EndZ=0
    g45: LineSegment StartX=-49.19 StartY=8.5 StartZ=0 EndX=-1.5 EndY=8.5 EndZ=0
    g46: LineSegment StartX=-49.19 StartY=5.75 StartZ=0 EndX=-1.5 EndY=5.75 EndZ=0
    g47: LineSegment StartX=-49.19 StartY=2.75 StartZ=0 EndX=-1.5 EndY=2.75 EndZ=0
  constraints (120):
    c: Vertical(g0)
    c: Distance(g0) = 3
    c: Block(g0)
    c: Vertical(g1)
    c: Distance(g1) = 3
    c: Vertical(g2)
    c: Equal(g0,g2) = 3
    c: Block(g2)
    c: Vertical(g3)
    c: Equal(g1,g3) = 3
    c: Vertical(g4)
    c: Equal(g0,g4) = 3
    c: Block(g4)
    c: Vertical(g5)
    c: Equal(g1,g5) = 3
    c: Vertical(g6)
    c: Equal(g0,g6) = 3
    c: Block(g6)
    c: Vertical(g7)
    c: Equal(g1,g7) = 3
    c: Vertical(g8)
    c: Equal(g0,g8) = 3
    c: Block(g8)
    c: Vertical(g9)
    c: Equal(g1,g9) = 3
    c: Vertical(g10)
    c: Equal(g0,g10) = 3
    c: Block(g10)
    c: Vertical(g11)
    c: Equal(g1,g11) = 3
    c: Block(g12)
    c: Block(g13)
    c: Block(g14)
    c: Block(g15)
    c: Block(g16)
    c: Block(g17)
    c: Block(g18)
    c: Block(g19)
    c: Block(g20)
    c: Block(g21)
    c: Block(g22)
    c: Block(g23)
    c: Block(g11)
    c: Block(g9)
    c: Block(g7)
    c: Block(g5)
    c: Block(g3)
    c: Block(g1)
    c: Coincident(g24,g0)
    c: Coincident(g24,g12)
    c: Horizontal(g24)
    c: Coincident(g25,g0)
    c: Coincident(g25,g12)
    c: Horizontal(g25)
    c: Coincident(g26,g1)
    c: Coincident(g26,g13)
    c: Horizontal(g26)
    c: Coincident(g27,g1)
    c: Coincident(g27,g13)
    c: Horizontal(g27)
    c: Coincident(g28,g2)
    c: Coincident(g28,g14)
    c: Horizontal(g28)
    c: Coincident(g29,g2)
    c: Coincident(g29,g14)
    c: Horizontal(g29)
    c: Coincident(g30,g3)
    c: Coincident(g30,g15)
    c: Horizontal(g30)
    c: Coincident(g31,g3)
    c: Coincident(g31,g15)
    c: Horizontal(g31)
    c: Coincident(g32,g4)
    c: Coincident(g32,g16)
    c: Horizontal(g32)
    c: Coincident(g33,g4)
    c: Coincident(g33,g16)
    c: Horizontal(g33)
    c: Coincident(g34,g5)
    c: Coincident(g34,g17)
    c: Horizontal(g34)
    c: Coincident(g35,g5)
    c: Coincident(g35,g17)
    c: Horizontal(g35)
    c: Coincident(g36,g6)
    c: Coincident(g36,g19)
    c: Horizontal(g36)
    c: Coincident(g37,g6)
    c: Coincident(g37,g19)
    c: Horizontal(g37)
    c: Coincident(g38,g7)
    c: Coincident(g38,g18)
    c: Horizontal(g38)
    c: Coincident(g39,g7)
    c: Coincident(g39,g18)
    c: Horizontal(g39)
    c: Coincident(g40,g8)
    c: Coincident(g40,g20)
    c: Horizontal(g40)
    c: Coincident(g41,g8)
    c: Coincident(g41,g20)
    c: Horizontal(g41)
    c: Coincident(g42,g9)
    c: Coincident(g42,g23)
    c: Horizontal(g42)
    c: Coincident(g43,g9)
    c: Coincident(g43,g23)
    c: Horizontal(g43)
    c: Coincident(g44,g10)
    c: Coincident(g44,g22)
    c: Horizontal(g44)
    c: Coincident(g45,g10)
    c: Coincident(g45,g22)
    c: Horizontal(g45)
    c: Coincident(g46,g11)
    c: Coincident(g46,g21)
    c: Horizontal(g46)
    c: Coincident(g47,g11)
    c: Coincident(g47,g21)
    c: Horizontal(g47)
FEATURE [Part::Extrusion] Extrude023
  Base = -> Sketch032
  Dir = (1,-2e-16,2e-16)
  DirMode = 2
  FaceMakerClass = Part::FaceMakerBullseye
  LengthFwd = 19
  LengthRev = 0
  Placement = pos=(-19,0,0) rot=(0,0,1;0rad)
  Solid = true
  Symmetric = false
FEATURE [Part::Fillet] Fillet023
  Base = -> Extrude023
  Edges = <same value as first occurrence — deduplicated (x5 in doc)>
  Placement = pos=(0,0.05,0) rot=(0,0,1;0rad)
FEATURE [Part::Cut] Cut014  label="bottom003"
  Base = -> Cut007
  Tool = -> Fusion047
FEATURE [Part::Cut] Cut021  label="bottom004"
  Base = -> Cut014
  Tool = -> Fillet023
FEATURE [Sketcher::SketchObject] Sketch033
  FullyConstrained = true
  Placement = pos=(117,19,0) rot=(0.57735,0.57735,0.57735;2.0944rad)
  sketch-geometry (8):
    g0: LineSegment StartX=-49.19 StartY=69.25 StartZ=0 EndX=-49.19 EndY=66.25 EndZ=0
    g1: LineSegment StartX=-49.19 StartY=5.75 StartZ=0 EndX=-49.19 EndY=2.75 EndZ=0
    g2: ArcOfCircle CenterX=-1.5 CenterY=67.75 CenterZ=0 NormalX=0 NormalY=0 NormalZ=1 AngleXU=0 Radius=1.5 StartAngle=4.71239 EndAngle=7.85398
    g3: ArcOfCircle CenterX=-1.5 CenterY=4.25 CenterZ=0 NormalX=0 NormalY=0 NormalZ=1 AngleXU=0 Radius=1.5 StartAngle=4.71239 EndAngle=7.85398
    g4: LineSegment StartX=-49.19 StartY=69.25 StartZ=0 EndX=-1.5 EndY=69.25 EndZ=0
    g5: LineSegment StartX=-49.19 StartY=66.25 StartZ=0 EndX=-1.5 EndY=66.25 EndZ=0
    g6: LineSegment StartX=-49.19 StartY=5.75 StartZ=0 EndX=-1.5 EndY=5.75 EndZ=0
    g7: LineSegment StartX=-49.19 StartY=2.75 StartZ=0 EndX=-1.5 EndY=2.75 EndZ=0
  constraints (19):
    c: Vertical(g0)
    c: Distance(g0) = 3
    c: Block(g0)
    c: Vertical(g1)
    c: Block(g2)
    c: Block(g3)
    c: Block(g1)
    c: Coincident(g4,g0)
    c: Coincident(g4,g2)
    c: Horizontal(g4)
    c: Coincident(g5,g0)
    c: Coincident(g5,g2)
    c: Horizontal(g5)
    c: Coincident(g6,g1)
    c: Coincident(g6,g3)
    c: Horizontal(g6)
    c: Coincident(g7,g1)
    c: Coincident(g7,g3)
    c: Horizontal(g7)
FEATURE [Sketcher::SketchObject] Sketch034
  FullyConstrained = true
  Placement = pos=(117,19,0) rot=(0.57735,0.57735,0.57735;2.0944rad)
  sketch-geometry (8):
    g0: LineSegment StartX=-49.19 StartY=63.5 StartZ=0 EndX=-49.19 EndY=60.5 EndZ=0
    g1: LineSegment StartX=-49.19 StartY=11.5 StartZ=0 EndX=-49.19 EndY=8.5 EndZ=0
    g2: ArcOfCircle CenterX=-1.5 CenterY=62 CenterZ=0 NormalX=0 NormalY=0 NormalZ=1 AngleXU=0 Radius=1.5 StartAngle=4.71239 EndAngle=7.85398
    g3: ArcOfCircle CenterX=-1.5 CenterY=10 CenterZ=0 NormalX=0 NormalY=0 NormalZ=1 AngleXU=0 Radius=1.5 StartAngle=4.71239 EndAngle=7.85398
    g4: LineSegment StartX=-49.19 StartY=63.5 StartZ=0 EndX=-1.5 EndY=63.5 EndZ=0
    g5: LineSegment StartX=-49.19 StartY=60.5 StartZ=0 EndX=-1.5 EndY=60.5 EndZ=0
    g6: LineSegment StartX=-49.19 StartY=11.5 StartZ=0 EndX=-1.5 EndY=11.5 EndZ=0
    g7: LineSegment StartX=-49.19 StartY=8.5 StartZ=0 EndX=-1.5 EndY=8.5 EndZ=0
  constraints (19):
    c: Vertical(g0)
    c: Distance(g0) = 3
    c: Vertical(g1)
    c: Block(g1)
    c: Block(g2)
    c: Block(g3)
    c: Block(g0)
    c: Coincident(g4,g0)
    c: Coincident(g4,g2)
    c: Horizontal(g4)
    c: Coincident(g5,g0)
    c: Coincident(g5,g2)
    c: Horizontal(g5)
    c: Coincident(g6,g1)
    c: Coincident(g6,g3)
    c: Horizontal(g6)
    c: Coincident(g7,g1)
    c: Coincident(g7,g3)
    c: Horizontal(g7)
FEATURE [Part::Extrusion] Extrude024
  Base = -> Sketch033
  Dir = (1,0,0)
  DirMode = 2
  FaceMakerClass = Part::FaceMakerBullseye
  LengthFwd = 10
  LengthRev = 0
  Solid = true
  Symmetric = false
FEATURE [Part::Extrusion] Extrude025
  Base = -> Sketch034
  Dir = (1,0,0)
  DirMode = 2
  FaceMakerClass = Part::FaceMakerBullseye
  LengthFwd = 10
  LengthRev = 0
  Solid = true
  Symmetric = false
FEATURE [Part::Fillet] Fillet024  label="removeFromtMoreFrontCaseScrewRetainers"
  Base = -> Extrude024
  Edges = 4 edges r=1.49: [Edge6,Edge11,Edge18,Edge23]
  Placement = pos=(-11,0,0) rot=(0,0,1;0rad)
FEATURE [Part::Fillet] Fillet025  label="removeFromtMoreFrontCaseScrewRetainers001"
  Base = -> Extrude025
  Edges = 4 edges r=1.49: [Edge6,Edge11,Edge18,Edge23]
  Placement = pos=(-19,0,0) rot=(0,0,1;0rad)
FEATURE [Part::Cut] Cut022
  Base = -> Cut015
  Tool = -> Fillet025
FEATURE [Part::Cut] Cut023  label="screwRetainers"
  Base = -> Cut022
  Tool = -> Fillet024
FEATURE [Part::MultiFuse] Fusion056  label="bottom005"
  Shapes = -> [Fusion044,Cut021]
FEATURE [Part::MultiFuse] Fusion057  label="casePillars001"
  Shapes = -> [Cut016,Fusion052]
FEATURE [Part::MultiFuse] Fusion058  label="bottom006"
  Shapes = -> [Fusion056,Cut023]
FEATURE [Part::MultiFuse] Fusion059  label="bottom007"
  Shapes = -> [Fusion058,Fillet005]
FEATURE [Part::MultiFuse] Fusion060  label="bottom008"
  Shapes = -> [Fusion059,Fusion]
FEATURE [Part::MultiFuse] Fusion061  label="top011"
  Shapes = -> [Cut006,Cut020]
FEATURE [Part::MultiFuse] Fusion062  label="top012"
  Shapes = -> [Fusion057,Fusion061]
FEATURE [Sketcher::SketchObject] Sketch035  label="topSketch007"
  FullyConstrained = true
  sketch-geometry (6):
    g0: LineSegment StartX=19 StartY=38 StartZ=0 EndX=117 EndY=38 EndZ=0
    g1: ArcOfCircle CenterX=19 CenterY=19 CenterZ=0 NormalX=0 NormalY=0 NormalZ=1 AngleXU=0 Radius=19 StartAngle=1.5708 EndAngle=3.14159
    g2: LineSegment StartX=117 StartY=38 StartZ=0 EndX=117 EndY=19 EndZ=0
    g3: LineSegment StartX=98 StartY=1.0161e-12 StartZ=0 EndX=5.22862e-06 EndY=1.0161e-12 EndZ=0
    g4: LineSegment StartX=5.22862e-06 StartY=19 StartZ=0 EndX=5.22862e-06 EndY=1.0161e-12 EndZ=0
    g5: ArcOfCircle CenterX=98 CenterY=19 CenterZ=0 NormalX=0 NormalY=0 NormalZ=1 AngleXU=0 Radius=19 StartAngle=4.71239 EndAngle=6.28319
  constraints (16):
    c: Horizontal(g0)
    c: Distance(g0) = 98
    c: Coincident(g1,g0)
    c: Block(g1)
    c: Coincident(g2,g0)
    c: Vertical(g2)
    c: Distance(g2) = 19
    c: Horizontal(g3)
    c: Coincident(g4,g1)
    c: Vertical(g4)
    c: Coincident(g3,g4)
    c: Block(g3)
    c: Coincident(g5,g2)
    c: Coincident(g5,g3)
    c: Block(g0)
    c: Block(g5)
FEATURE [Part::Extrusion] Extrude026  label="sideA001"
  Base = -> Sketch035
  Dir = (0,0,1)
  DirMode = 2
  FaceMakerClass = Part::FaceMakerBullseye
  LengthFwd = 3
  LengthRev = 0
  Placement = pos=(0,0,-2.7) rot=(0,0,1;0rad)
  Solid = true
  Symmetric = false
FEATURE [Sketcher::SketchObject] Sketch036  label="topSketch008"
  FullyConstrained = true
  sketch-geometry (6):
    g0: LineSegment StartX=19 StartY=38 StartZ=0 EndX=117 EndY=38 EndZ=0
    g1: ArcOfCircle CenterX=19 CenterY=19 CenterZ=0 NormalX=0 NormalY=0 NormalZ=1 AngleXU=0 Radius=19 StartAngle=1.5708 EndAngle=3.14159
    g2: LineSegment StartX=117 StartY=38 StartZ=0 EndX=117 EndY=19 EndZ=0
    g3: LineSegment StartX=98 StartY=1.0161e-12 StartZ=0 EndX=5.22862e-06 EndY=1.0161e-12 EndZ=0
    g4: LineSegment StartX=5.22862e-06 StartY=19 StartZ=0 EndX=5.22862e-06 EndY=1.0161e-12 EndZ=0
    g5: ArcOfCircle CenterX=98 CenterY=19 CenterZ=0 NormalX=0 NormalY=0 NormalZ=1 AngleXU=0 Radius=19 StartAngle=4.71239 EndAngle=6.28319
  constraints (16):
    c: Horizontal(g0)
    c: Distance(g0) = 98
    c: Coincident(g1,g0)
    c: Block(g1)
    c: Coincident(g2,g0)
    c: Vertical(g2)
    c: Distance(g2) = 19
    c: Horizontal(g3)
    c: Coincident(g4,g1)
    c: Vertical(g4)
    c: Coincident(g3,g4)
    c: Block(g3)
    c: Coincident(g5,g2)
    c: Coincident(g5,g3)
    c: Block(g0)
    c: Block(g5)
FEATURE [Part::Extrusion] Extrude027  label="sideB001"
  Base = -> Sketch036
  Dir = (0,0,1)
  DirMode = 2
  FaceMakerClass = Part::FaceMakerBullseye
  LengthFwd = 3
  LengthRev = 0
  Placement = pos=(0,0,71.7) rot=(0,0,1;0rad)
  Solid = true
  Symmetric = false
FEATURE [Part::MultiFuse] Fusion064  label="removeFromBottom"
  Shapes = -> [Extrude026,Extrude027]
FEATURE [Part::Cut] Cut024  label="bottom009"
  Base = -> Fusion060
  Tool = -> Fusion064
FEATURE [Sketcher::SketchObject] Sketch037  label="topSketch009"
  FullyConstrained = true
  sketch-geometry (6):
    g0: ArcOfCircle CenterX=19 CenterY=19 CenterZ=0 NormalX=0 NormalY=0 NormalZ=1 AngleXU=0 Radius=19 StartAngle=1.5708 EndAngle=3.14159
    g1: LineSegment StartX=5.22862e-06 StartY=19 StartZ=0 EndX=5.22862e-06 EndY=1.19904e-11 EndZ=0
    g2: LineSegment StartX=19 StartY=38 StartZ=0 EndX=124 EndY=38 EndZ=0
    g3: LineSegment StartX=5.22862e-06 StartY=1.19904e-11 StartZ=0 EndX=105 EndY=1.19904e-11 EndZ=0
    g4: ArcOfCircle CenterX=105 CenterY=19 CenterZ=0 NormalX=0 NormalY=0 NormalZ=1 AngleXU=0 Radius=19 StartAngle=4.71239 EndAngle=6.28319
    g5: LineSegment StartX=124 StartY=38 StartZ=0 EndX=124 EndY=19 EndZ=0
  constraints (16):
    c: Block(g0)
    c: Coincident(g1,g0)
    c: Vertical(g1)
    c: Horizontal(g2)
    c: Distance(g2) = 105
    c: Coincident(g2,g0)
    c: Distance(g1) = 19
    c: Coincident(g3,g1)
    c: Horizontal(g3)
    c: Distance(g3) = 105
    c: Block(g4)
    c: Coincident(g4,g3)
    c: Coincident(g5,g2)
    c: Coincident(g5,g4)
    c: Vertical(g5)
    c: Distance(g5) = 19
FEATURE [Part::Extrusion] Extrude028  label="sideB"
  Base = -> Sketch037
  Dir = (0,0,1)
  DirMode = 2
  FaceMakerClass = Part::FaceMakerBullseye
  LengthFwd = 3
  LengthRev = 0
  Placement = pos=(0,0,72) rot=(0,0,1;0rad)
  Solid = true
  Symmetric = false
FEATURE [Sketcher::SketchObject] Sketch038  label="topSketch010"
  FullyConstrained = true
  sketch-geometry (22):
    g0: LineSegment StartX=5.21097e-06 StartY=3 StartZ=0 EndX=5.21097e-06 EndY=19 EndZ=0
    g1: ArcOfCircle CenterX=19 CenterY=19 CenterZ=0 NormalX=0 NormalY=0 NormalZ=1 AngleXU=0 Radius=19 StartAngle=1.5708 EndAngle=3.14159
    g2: ArcOfCircle CenterX=19 CenterY=19 CenterZ=0 NormalX=0 NormalY=0 NormalZ=1 AngleXU=0 Radius=16 StartAngle=1.5708 EndAngle=3.14159
    g3: LineSegment StartX=114 StartY=35 StartZ=0 EndX=19 EndY=35 EndZ=0
    g4: LineSegment StartX=5.21097e-06 StartY=3 StartZ=0 EndX=5.21097e-06 EndY=0 EndZ=0
    g5: LineSegment StartX=3 StartY=0 StartZ=0 EndX=5.21097e-06 EndY=0 EndZ=0
    g6: LineSegment StartX=3 StartY=19 StartZ=0 EndX=3 EndY=0 EndZ=0
    g7: LineSegment StartX=19 StartY=38 StartZ=0 EndX=124 EndY=38 EndZ=0
    g8: Circle CenterX=119 CenterY=35 CenterZ=0 NormalX=0 NormalY=0 NormalZ=1 AngleXU=0 Radius=1
    g9: Circle CenterX=121 CenterY=35 CenterZ=0 NormalX=0 NormalY=0 NormalZ=1 AngleXU=0 Radius=1
    g10: Circle CenterX=121 CenterY=33 CenterZ=0 NormalX=0 NormalY=0 NormalZ=1 AngleXU=0 Radius=1
    g11: BSplineCurve PolesCount=3 KnotsCount=2 Degree=2 IsPeriodic=0
    g12: GeomPoint X=119 Y=35 Z=0
    g13: GeomPoint X=121 Y=33 Z=0
    g14: LineSegment StartX=119 StartY=35 StartZ=0 EndX=114 EndY=35 EndZ=0
    g15: ArcOfCircle CenterX=105 CenterY=19 CenterZ=0 NormalX=0 NormalY=0 NormalZ=1 AngleXU=0 Radius=16 StartAngle=5.60905 EndAngle=6.28319
    g16: LineSegment StartX=121 StartY=33 StartZ=0 EndX=121 EndY=19 EndZ=0
    g17: LineSegment StartX=117.5 StartY=9.01251 StartZ=0 EndX=121.163 EndY=9.0125 EndZ=0
    g18: ArcOfCircle CenterX=105 CenterY=19 CenterZ=0 NormalX=0 NormalY=0 NormalZ=1 AngleXU=0 Radius=20.6155 StartAngle=5.7297 EndAngle=6.28319
    g19: LineSegment StartX=121.163 StartY=9.0125 StartZ=0 EndX=122.538 EndY=8.16329 EndZ=0
    g20: LineSegment StartX=124 StartY=38 StartZ=0 EndX=125.616 EndY=38 EndZ=0
    g21: LineSegment StartX=125.616 StartY=19 StartZ=0 EndX=125.616 EndY=38 EndZ=0
  constraints (49):
    c: Vertical(g0)
    c: Block(g0)
    c: Coincident(g1,g0)
    c: Block(g1)
    c: Coincident(g2,g1)
    c: Block(g2)
    c: Coincident(g3,g2)
    c: Horizontal(g3)
    c: Tangent(g3,g2)
    c: Coincident(g4,g0)
    c: Distance(g4) = 3
    c: Vertical(g4)
    c: Coincident(g5,g4)
    c: Horizontal(g5)
    c: Coincident(g6,g2)
    c: Coincident(g6,g5)
    c: Vertical(g6)
    c: Horizontal(g7)
    c: Distance(g7) = 105
    c: Coincident(g7,g1)
    c: Block(g3)
    c: Weight(g8) = 1
    c: Equal(g8,g9)
    c: Equal(g8,g10)
    c: InternalAlignment(g8,g11)
    c: InternalAlignment(g9,g11)
    c: InternalAlignment(g10,g11)
    c: InternalAlignment(g12,g11)
    c: InternalAlignment(g13,g11)
    c: Block(g11)
    c: Coincident(g14,g11)
    c: Coincident(g14,g3)
    c: Horizontal(g14)
    c: Block(g15)
    c: Coincident(g16,g11)
    c: Coincident(g16,g15)
    c: Vertical(g16)
    c: Distance(g16) = 14
    c: Coincident(g17,g15)
    c: Block(g18)
    c: Coincident(g19,g18)
    c: Coincident(g20,g7)
    c: Horizontal(g20)
    c: Vertical(g21)
    c: Coincident(g20,g21)
    c: Block(g20)
    c: Block(g21)
    c: Block(g19)
    c: Block(g17)
FEATURE [Part::Extrusion] Extrude029
  Base = -> Sketch038
  Dir = (0,0,1)
  DirMode = 2
  FaceMakerClass = Part::FaceMakerBullseye
  LengthFwd = 72
  LengthRev = 0
  Solid = true
  Symmetric = false
FEATURE [Part::Feature] Face085
  shape: bbox 4.8 x 25.5 x 2e-07 mm, 1 faces, 0 solids (baked)
FEATURE [Part::Revolution] Revolve089  label="moreFrontCaseScrewPost003"
  Angle = 360
  Axis = (0,1,0)
  Base = (0,0,0)
  FaceMakerClass = Part::FaceMakerBullseye
  Placement = pos=(109.5,4.5,3.5) rot=(0,0,1;0rad)
  Solid = false
  Source = -> Face085
  Symmetric = false
FEATURE [Part::Feature] Face086
  shape: bbox 4.8 x 25.5 x 2e-07 mm, 1 faces, 0 solids (baked)
FEATURE [Part::Revolution] Revolve090  label="moreFrontCaseScrewPost004"
  Angle = 360
  Axis = (0,1,0)
  Base = (0,0,0)
  FaceMakerClass = Part::FaceMakerBullseye
  Placement = pos=(109.5,4.5,68.5) rot=(0,0,1;0rad)
  Solid = false
  Source = -> Face086
  Symmetric = false
FEATURE [Part::Fillet] Fillet026  label="top013"
  Base = -> Extrude029
  Edges = 1 edges r=2: [Edge35]
FEATURE [Sketcher::SketchObject] Sketch039
  FullyConstrained = true
  sketch-geometry (7):
    g0: LineSegment StartX=0 StartY=0 StartZ=0 EndX=0 EndY=6 EndZ=0
    g1: Circle CenterX=0 CenterY=0 CenterZ=0 NormalX=0 NormalY=0 NormalZ=1 AngleXU=0 Radius=1
    g2: Circle CenterX=8 CenterY=6 CenterZ=0 NormalX=0 NormalY=0 NormalZ=1 AngleXU=0 Radius=1
    g3: BSplineCurve PolesCount=3 KnotsCount=2 Degree=2 IsPeriodic=0
    g4: GeomPoint X=0 Y=0 Z=0
    g5: GeomPoint X=8 Y=6 Z=0
    g6: LineSegment StartX=0 StartY=6 StartZ=0 EndX=8 EndY=6 EndZ=0
  constraints (14):
    c: Coincident(g0,g-1)
    c: Distance(g0) = 6
    c: Vertical(g0)
    c: Coincident(g3,g0)
    c: Weight(g1) = 1
    c: Equal(g1,g2)
    c: InternalAlignment(g1,g3)
    c: InternalAlignment(g2,g3)
    c: InternalAlignment(g4,g3)
    c: InternalAlignment(g5,g3)
    c: Block(g3)
    c: Coincident(g6,g0)
    c: Coincident(g6,g3)
    c: Horizontal(g6)
FEATURE [Sketcher::SketchObject] Sketch040
  FullyConstrained = true
  sketch-geometry (7):
    g0: LineSegment StartX=0 StartY=0 StartZ=0 EndX=0 EndY=6 EndZ=0
    g1: Circle CenterX=0 CenterY=0 CenterZ=0 NormalX=0 NormalY=0 NormalZ=1 AngleXU=0 Radius=1
    g2: Circle CenterX=8 CenterY=6 CenterZ=0 NormalX=0 NormalY=0 NormalZ=1 AngleXU=0 Radius=1
    g3: BSplineCurve PolesCount=3 KnotsCount=2 Degree=2 IsPeriodic=0
    g4: GeomPoint X=0 Y=0 Z=0
    g5: GeomPoint X=8 Y=6 Z=0
    g6: LineSegment StartX=0 StartY=6 StartZ=0 EndX=8 EndY=6 EndZ=0
  constraints (14):
    c: Coincident(g0,g-1)
    c: Distance(g0) = 6
    c: Vertical(g0)
    c: Coincident(g3,g0)
    c: Weight(g1) = 1
    c: Equal(g1,g2)
    c: InternalAlignment(g1,g3)
    c: InternalAlignment(g2,g3)
    c: InternalAlignment(g4,g3)
    c: InternalAlignment(g5,g3)
    c: Block(g3)
    c: Coincident(g6,g0)
    c: Coincident(g6,g3)
    c: Horizontal(g6)
FEATURE [Sketcher::SketchObject] Sketch041
  FullyConstrained = true
  sketch-geometry (7):
    g0: LineSegment StartX=0 StartY=0 StartZ=0 EndX=0 EndY=6 EndZ=0
    g1: Circle CenterX=0 CenterY=0 CenterZ=0 NormalX=0 NormalY=0 NormalZ=1 AngleXU=0 Radius=1
    g2: Circle CenterX=8 CenterY=6 CenterZ=0 NormalX=0 NormalY=0 NormalZ=1 AngleXU=0 Radius=1
    g3: BSplineCurve PolesCount=3 KnotsCount=2 Degree=2 IsPeriodic=0
    g4: GeomPoint X=0 Y=0 Z=0
    g5: GeomPoint X=8 Y=6 Z=0
    g6: LineSegment StartX=0 StartY=6 StartZ=0 EndX=8 EndY=6 EndZ=0
  constraints (14):
    c: Coincident(g0,g-1)
    c: Distance(g0) = 6
    c: Vertical(g0)
    c: Coincident(g3,g0)
    c: Weight(g1) = 1
    c: Equal(g1,g2)
    c: InternalAlignment(g1,g3)
    c: InternalAlignment(g2,g3)
    c: InternalAlignment(g4,g3)
    c: InternalAlignment(g5,g3)
    c: Block(g3)
    c: Coincident(g6,g0)
    c: Coincident(g6,g3)
    c: Horizontal(g6)
FEATURE [Sketcher::SketchObject] Sketch042
  FullyConstrained = true
  sketch-geometry (7):
    g0: LineSegment StartX=0 StartY=0 StartZ=0 EndX=0 EndY=6 EndZ=0
    g1: Circle CenterX=0 CenterY=0 CenterZ=0 NormalX=0 NormalY=0 NormalZ=1 AngleXU=0 Radius=1
    g2: Circle CenterX=8 CenterY=6 CenterZ=0 NormalX=0 NormalY=0 NormalZ=1 AngleXU=0 Radius=1
    g3: BSplineCurve PolesCount=3 KnotsCount=2 Degree=2 IsPeriodic=0
    g4: GeomPoint X=0 Y=0 Z=0
    g5: GeomPoint X=8 Y=6 Z=0
    g6: LineSegment StartX=0 StartY=6 StartZ=0 EndX=8 EndY=6 EndZ=0
  constraints (14):
    c: Coincident(g0,g-1)
    c: Distance(g0) = 6
    c: Vertical(g0)
    c: Coincident(g3,g0)
    c: Weight(g1) = 1
    c: Equal(g1,g2)
    c: InternalAlignment(g1,g3)
    c: InternalAlignment(g2,g3)
    c: InternalAlignment(g4,g3)
    c: InternalAlignment(g5,g3)
    c: Block(g3)
    c: Coincident(g6,g0)
    c: Coincident(g6,g3)
    c: Horizontal(g6)
FEATURE [Part::Extrusion] Extrude030  label="caseScrewPillarBracket008"
  Base = -> Sketch039
  Dir = (0,0,1)
  DirMode = 2
  FaceMakerClass = Part::FaceMakerBullseye
  LengthFwd = 2.4
  LengthRev = 0
  Placement = pos=(15.76,29,8.8) rot=(0,1,0;0rad)
  Solid = true
  Symmetric = false
FEATURE [Part::Extrusion] Extrude031  label="caseScrewPillarBracket009"
  Base = -> Sketch040
  Dir = (0,0,1)
  DirMode = 2
  FaceMakerClass = Part::FaceMakerBullseye
  LengthFwd = 2.4
  LengthRev = 0
  Placement = pos=(15.76,29,60.8) rot=(0,0,1;0rad)
  Solid = true
  Symmetric = false
FEATURE [Part::Extrusion] Extrude032  label="caseScrewPillarBracket010"
  Base = -> Sketch041
  Dir = (0,0,1)
  DirMode = 2
  FaceMakerClass = Part::FaceMakerBullseye
  LengthFwd = 2.4
  LengthRev = 0
  Placement = pos=(13.7,29,13.26) rot=(0,-1,0;1.5708rad)
  Solid = true
  Symmetric = false
FEATURE [Part::Extrusion] Extrude033  label="caseScrewPillarBracket011"
  Base = -> Sketch042
  Dir = (0,0,1)
  DirMode = 2
  FaceMakerClass = Part::FaceMakerBullseye
  LengthFwd = 2.4
  LengthRev = 0
  Placement = pos=(11.3,29,58.74) rot=(0,1,0;1.5708rad)
  Solid = true
  Symmetric = false
FEATURE [Sketcher::SketchObject] Sketch043
  FullyConstrained = true
  sketch-geometry (7):
    g0: LineSegment StartX=0 StartY=0 StartZ=0 EndX=0 EndY=6 EndZ=0
    g1: Circle CenterX=0 CenterY=0 CenterZ=0 NormalX=0 NormalY=0 NormalZ=1 AngleXU=0 Radius=1
    g2: Circle CenterX=8 CenterY=6 CenterZ=0 NormalX=0 NormalY=0 NormalZ=1 AngleXU=0 Radius=1
    g3: BSplineCurve PolesCount=3 KnotsCount=2 Degree=2 IsPeriodic=0
    g4: GeomPoint X=0 Y=0 Z=0
    g5: GeomPoint X=8 Y=6 Z=0
    g6: LineSegment StartX=0 StartY=6 StartZ=0 EndX=8 EndY=6 EndZ=0
  constraints (14):
    c: Coincident(g0,g-1)
    c: Distance(g0) = 6
    c: Vertical(g0)
    c: Coincident(g3,g0)
    c: Weight(g1) = 1
    c: Equal(g1,g2)
    c: InternalAlignment(g1,g3)
    c: InternalAlignment(g2,g3)
    c: InternalAlignment(g4,g3)
    c: InternalAlignment(g5,g3)
    c: Block(g3)
    c: Coincident(g6,g0)
    c: Coincident(g6,g3)
    c: Horizontal(g6)
FEATURE [Part::Extrusion] Extrude034  label="caseScrewPillarBracket012"
  Base = -> Sketch043
  Dir = (0,0,1)
  DirMode = 2
  FaceMakerClass = Part::FaceMakerBullseye
  LengthFwd = 2.4
  LengthRev = 0
  Placement = pos=(88.3,29,65.23) rot=(0,1,0;1.5708rad)
  Solid = true
  Symmetric = false
FEATURE [Sketcher::SketchObject] Sketch044
  FullyConstrained = true
  sketch-geometry (7):
    g0: LineSegment StartX=0 StartY=0 StartZ=0 EndX=0 EndY=6 EndZ=0
    g1: Circle CenterX=0 CenterY=0 CenterZ=0 NormalX=0 NormalY=0 NormalZ=1 AngleXU=0 Radius=1
    g2: Circle CenterX=8 CenterY=6 CenterZ=0 NormalX=0 NormalY=0 NormalZ=1 AngleXU=0 Radius=1
    g3: BSplineCurve PolesCount=3 KnotsCount=2 Degree=2 IsPeriodic=0
    g4: GeomPoint X=0 Y=0 Z=0
    g5: GeomPoint X=8 Y=6 Z=0
    g6: LineSegment StartX=0 StartY=6 StartZ=0 EndX=8 EndY=6 EndZ=0
  constraints (14):
    c: Coincident(g0,g-1)
    c: Distance(g0) = 6
    c: Vertical(g0)
    c: Coincident(g3,g0)
    c: Weight(g1) = 1
    c: Equal(g1,g2)
    c: InternalAlignment(g1,g3)
    c: InternalAlignment(g2,g3)
    c: InternalAlignment(g4,g3)
    c: InternalAlignment(g5,g3)
    c: Block(g3)
    c: Coincident(g6,g0)
    c: Coincident(g6,g3)
    c: Horizontal(g6)
FEATURE [Part::Extrusion] Extrude035  label="caseScrewPillarBracket013"
  Base = -> Sketch044
  Dir = (0,0,1)
  DirMode = 2
  FaceMakerClass = Part::FaceMakerBullseye
  LengthFwd = 2.4
  LengthRev = 0
  Placement = pos=(90.7,29,6.77) rot=(0,-1,0;1.5708rad)
  Solid = true
  Symmetric = false
FEATURE [Sketcher::SketchObject] Sketch045
  FullyConstrained = true
  sketch-geometry (7):
    g0: LineSegment StartX=0 StartY=0 StartZ=0 EndX=0 EndY=6 EndZ=0
    g1: Circle CenterX=0 CenterY=0 CenterZ=0 NormalX=0 NormalY=0 NormalZ=1 AngleXU=0 Radius=1
    g2: Circle CenterX=8 CenterY=6 CenterZ=0 NormalX=0 NormalY=0 NormalZ=1 AngleXU=0 Radius=1
    g3: BSplineCurve PolesCount=3 KnotsCount=2 Degree=2 IsPeriodic=0
    g4: GeomPoint X=0 Y=0 Z=0
    g5: GeomPoint X=8 Y=6 Z=0
    g6: LineSegment StartX=0 StartY=6 StartZ=0 EndX=8 EndY=6 EndZ=0
  constraints (14):
    c: Coincident(g0,g-1)
    c: Distance(g0) = 6
    c: Vertical(g0)
    c: Coincident(g3,g0)
    c: Weight(g1) = 1
    c: Equal(g1,g2)
    c: InternalAlignment(g1,g3)
    c: InternalAlignment(g2,g3)
    c: InternalAlignment(g4,g3)
    c: InternalAlignment(g5,g3)
    c: Block(g3)
    c: Coincident(g6,g0)
    c: Coincident(g6,g3)
    c: Horizontal(g6)
FEATURE [Sketcher::SketchObject] Sketch046
  FullyConstrained = true
  sketch-geometry (7):
    g0: LineSegment StartX=0 StartY=0 StartZ=0 EndX=0 EndY=6 EndZ=0
    g1: Circle CenterX=0 CenterY=0 CenterZ=0 NormalX=0 NormalY=0 NormalZ=1 AngleXU=0 Radius=1
    g2: Circle CenterX=8 CenterY=6 CenterZ=0 NormalX=0 NormalY=0 NormalZ=1 AngleXU=0 Radius=1
    g3: BSplineCurve PolesCount=3 KnotsCount=2 Degree=2 IsPeriodic=0
    g4: GeomPoint X=0 Y=0 Z=0
    g5: GeomPoint X=8 Y=6 Z=0
    g6: LineSegment StartX=0 StartY=6 StartZ=0 EndX=8 EndY=6 EndZ=0
  constraints (14):
    c: Coincident(g0,g-1)
    c: Distance(g0) = 6
    c: Vertical(g0)
    c: Coincident(g3,g0)
    c: Weight(g1) = 1
    c: Equal(g1,g2)
    c: InternalAlignment(g1,g3)
    c: InternalAlignment(g2,g3)
    c: InternalAlignment(g4,g3)
    c: InternalAlignment(g5,g3)
    c: Block(g3)
    c: Coincident(g6,g0)
    c: Coincident(g6,g3)
    c: Horizontal(g6)
FEATURE [Part::Extrusion] Extrude036  label="caseScrewPillarBracket014"
  Base = -> Sketch045
  Dir = (0,0,1)
  DirMode = 2
  FaceMakerClass = Part::FaceMakerBullseye
  LengthFwd = 2.4
  LengthRev = 0
  Placement = pos=(110.7,29,6.77) rot=(0,-1,0;1.5708rad)
  Solid = true
  Symmetric = false
FEATURE [Part::Extrusion] Extrude037  label="caseScrewPillarBracket015"
  Base = -> Sketch046
  Dir = (0,0,1)
  DirMode = 2
  FaceMakerClass = Part::FaceMakerBullseye
  LengthFwd = 2.4
  LengthRev = 0
  Placement = pos=(108.3,29,65.23) rot=(0,1,0;1.5708rad)
  Solid = true
  Symmetric = false
FEATURE [Part::Box] Box013  label="frontCaseScrewPillarBracket002"
  AttacherType = Attacher::AttachEngine3D
  Height = 2.4
  Length = 22
  Placement = pos=(87,28,2.3) rot=(0,0,1;0rad)
  Width = 7
FEATURE [Part::Box] Box014  label="frontCaseScrewPillarBracket003"
  AttacherType = Attacher::AttachEngine3D
  Height = 2.4
  Length = 22
  Placement = pos=(87,28,67.3) rot=(0,0,1;0rad)
  Width = 7
FEATURE [Part::Feature] Face087
  shape: bbox 4.8 x 30.2 x 2e-07 mm, 1 faces, 0 solids (baked)
FEATURE [Part::Revolution] Revolve091  label="frontCaseScrewPost004"
  Angle = 360
  Axis = (0,1,0)
  Base = (0,0,0)
  FaceMakerClass = Part::FaceMakerBullseye
  Placement = pos=(89.5,4.5,3.5) rot=(0,0,1;0rad)
  Solid = false
  Source = -> Face087
  Symmetric = false
FEATURE [Part::Feature] Face088
  shape: bbox 4.8 x 30.2 x 2e-07 mm, 1 faces, 0 solids (baked)
FEATURE [Part::Revolution] Revolve092  label="frontCaseScrewPost005"
  Angle = 360
  Axis = (0,1,0)
  Base = (0,0,0)
  FaceMakerClass = Part::FaceMakerBullseye
  Placement = pos=(89.5,4.5,68.5) rot=(0,0,1;0rad)
  Solid = false
  Source = -> Face088
  Symmetric = false
FEATURE [Part::Feature] Face089
  shape: bbox 3.5 x 30.2 x 2e-07 mm, 1 faces, 0 solids (baked)
FEATURE [Part::Revolution] Revolve093  label="backCaseScrewPost002"
  Angle = 360
  Axis = (0,1,0)
  Base = (0,0,0)
  FaceMakerClass = Part::FaceMakerBullseye
  Placement = pos=(12.5,4.5,10) rot=(0,0,1;0rad)
  Solid = false
  Source = -> Face089
  Symmetric = false
FEATURE [Part::Feature] Face090
  shape: bbox 3.5 x 30.2 x 2e-07 mm, 1 faces, 0 solids (baked)
FEATURE [Part::Revolution] Revolve094  label="backCaseScrewPost003"
  Angle = 360
  Axis = (0,1,0)
  Base = (0,0,0)
  FaceMakerClass = Part::FaceMakerBullseye
  Placement = pos=(12.5,4.5,62) rot=(0,0,1;0rad)
  Solid = false
  Source = -> Face090
  Symmetric = false
FEATURE [Part::Box] Box015  label="Cube011"
  AttacherType = Attacher::AttachEngine3D
  Height = 28.8
  Length = 3
  Placement = pos=(107.3,28,21.6) rot=(0,0,1;0rad)
  Width = 7
FEATURE [Part::Box] Box016  label="Cube012"
  AttacherType = Attacher::AttachEngine3D
  Height = 3
  Length = 7.4
  Placement = pos=(107.3,28,18.6) rot=(0,0,1;0rad)
  Width = 7
FEATURE [Part::Box] Box017  label="Cube013"
  AttacherType = Attacher::AttachEngine3D
  Height = 3
  Length = 7.4
  Placement = pos=(107.3,28,50.4) rot=(0,0,1;0rad)
  Width = 7
FEATURE [Part::Cylinder] Cylinder024
  Angle = 360
  AttacherType = Attacher::AttachEngine3D
  Height = 20
  Placement = pos=(0,0,36.15) rot=(0,0,1;0rad)
  Radius = 14.3
FEATURE [Part::Cylinder] Cylinder025
  Angle = 360
  AttacherType = Attacher::AttachEngine3D
  Height = 10
  Placement = pos=(0,0,36.15) rot=(0,0,1;0rad)
  Radius = 4
FEATURE [Part::MultiFuse] Fusion066  label="removeToCreteHoleForPlugHousing009"
  Placement = pos=(70,19,36) rot=(0,1,0;1.5708rad)
  Shapes = -> [Cylinder024,Cylinder025]
FEATURE [Part::MultiFuse] Fusion065  label="plugHousingBracketHolder002"
  Shapes = -> [Box017,Box015,Box016]
FEATURE [Part::Cut] Cut025  label="plugHousingBracketHolder003"
  Base = -> Fusion065
  Placement = pos=(7,0,0) rot=(0,0,1;0rad)
  Tool = -> Fusion066
FEATURE [Sketcher::SketchObject] Sketch047
  FullyConstrained = false
  Placement = pos=(0,0,0) rot=(1,0,0;1.5708rad)
  sketch-geometry (24):
    g0: ArcOfCircle CenterX=-4 CenterY=-10.5 CenterZ=0 NormalX=0 NormalY=0 NormalZ=1 AngleXU=0 Radius=1.5 StartAngle=6e-16 EndAngle=3.14159
    g1: ArcOfCircle CenterX=-34.2 CenterY=-10.5 CenterZ=0 NormalX=0 NormalY=0 NormalZ=1 AngleXU=0 Radius=1.5 StartAngle=0 EndAngle=3.14159
    g2: ArcOfCircle CenterX=-34.2 CenterY=-27.7 CenterZ=0 NormalX=0 NormalY=0 NormalZ=1 AngleXU=0 Radius=1.5 StartAngle=3.14159 EndAngle=6.28319
    g3: ArcOfCircle CenterX=-4 CenterY=-27.7 CenterZ=0 NormalX=0 NormalY=0 NormalZ=1 AngleXU=0 Radius=1.5 StartAngle=3.1416 EndAngle=6.28319
    g4: ArcOfCircle CenterX=-10 CenterY=-4.3 CenterZ=0 NormalX=0 NormalY=0 NormalZ=1 AngleXU=0 Radius=1.5 StartAngle=2e-16 EndAngle=3.14159
    g5: ArcOfCircle CenterX=-16.1 CenterY=-1.8 CenterZ=0 NormalX=0 NormalY=0 NormalZ=1 AngleXU=0 Radius=1.5 StartAngle=5e-16 EndAngle=3.14159
    g6: ArcOfCircle CenterX=-22.1 CenterY=-1.8 CenterZ=0 NormalX=0 NormalY=0 NormalZ=1 AngleXU=0 Radius=1.5 StartAngle=5e-16 EndAngle=3.14159
    g7: ArcOfCircle CenterX=-28.2 CenterY=-4.3 CenterZ=0 NormalX=0 NormalY=0 NormalZ=1 AngleXU=0 Radius=1.5 StartAngle=2e-16 EndAngle=3.14159
    g8: ArcOfCircle CenterX=-10 CenterY=-33.9 CenterZ=0 NormalX=0 NormalY=0 NormalZ=1 AngleXU=0 Radius=1.5 StartAngle=3.14159 EndAngle=6.28319
    g9: ArcOfCircle CenterX=-16.1 CenterY=-36.4 CenterZ=0 NormalX=0 NormalY=0 NormalZ=1 AngleXU=0 Radius=1.5 StartAngle=3.14159 EndAngle=6.28319
    g10: ArcOfCircle CenterX=-22.1 CenterY=-36.4 CenterZ=0 NormalX=0 NormalY=0 NormalZ=1 AngleXU=0 Radius=1.5 StartAngle=3.14159 EndAngle=6.28319
    g11: ArcOfCircle CenterX=-28.2 CenterY=-33.9 CenterZ=0 NormalX=0 NormalY=0 NormalZ=1 AngleXU=0 Radius=1.5 StartAngle=3.14159 EndAngle=6.28319
    g12: LineSegment StartX=-35.7 StartY=-10.5 StartZ=0 EndX=-35.7 EndY=-27.7 EndZ=0
    g13: LineSegment StartX=-32.7 StartY=-10.5 StartZ=0 EndX=-32.7 EndY=-27.7 EndZ=0
    g14: LineSegment StartX=-29.7 StartY=-33.9 StartZ=0 EndX=-29.7 EndY=-4.3 EndZ=0
    g15: LineSegment StartX=-26.7 StartY=-33.9 StartZ=0 EndX=-26.7 EndY=-4.3 EndZ=0
    g16: LineSegment StartX=-2.5 StartY=-10.5 StartZ=0 EndX=-2.5 EndY=-27.7 EndZ=0
    g17: LineSegment StartX=-8.5 StartY=-4.3 StartZ=0 EndX=-8.5 EndY=-33.9 EndZ=0
    g18: LineSegment StartX=-5.5 StartY=-10.5 StartZ=0 EndX=-5.5 EndY=-27.7 EndZ=0
    g19: LineSegment StartX=-11.5 StartY=-4.3 StartZ=0 EndX=-11.5 EndY=-33.9 EndZ=0
    g20: LineSegment StartX=-14.6 StartY=-1.8 StartZ=0 EndX=-14.6 EndY=-36.4 EndZ=0
    g21: LineSegment StartX=-17.6 StartY=-1.8 StartZ=0 EndX=-17.6 EndY=-36.4 EndZ=0
    g22: LineSegment StartX=-20.6 StartY=-36.4 StartZ=0 EndX=-20.6 EndY=-1.8 EndZ=0
    g23: LineSegment StartX=-23.6 StartY=-1.8 StartZ=0 EndX=-23.6 EndY=-36.4 EndZ=0
  constraints (48):
    c: Block(g0)
    c: Block(g1)
    c: Block(g2)
    c: Block(g3)
    c: Block(g4)
    c: Block(g5)
    c: Block(g6)
    c: Block(g7)
    c: Block(g8)
    c: Block(g9)
    c: Block(g10)
    c: Block(g11)
    c: Coincident(g12,g1)
    c: Coincident(g12,g2)
    c: Vertical(g12)
    c: Coincident(g13,g1)
    c: Coincident(g13,g2)
    c: Vertical(g13)
    c: Coincident(g14,g11)
    c: Coincident(g14,g7)
    c: Vertical(g14)
    c: Coincident(g15,g11)
    c: Coincident(g15,g7)
    c: Vertical(g15)
    c: Coincident(g16,g0)
    c: Coincident(g16,g3)
    c: Vertical(g16)
    c: Coincident(g17,g4)
    c: Coincident(g17,g8)
    c: Vertical(g17)
    c: Coincident(g18,g0)
    c: Coincident(g18,g3)
    c: Vertical(g18)
    c: Coincident(g19,g4)
    c: Coincident(g19,g8)
    c: Vertical(g19)
    c: Coincident(g20,g5)
    c: Coincident(g20,g9)
    c: Vertical(g20)
    c: Coincident(g21,g5)
    c: Coincident(g21,g9)
    c: Vertical(g21)
    c: Coincident(g22,g10)
    c: Coincident(g22,g6)
    c: Vertical(g22)
    c: Coincident(g23,g6)
    c: Coincident(g23,g10)
    c: Vertical(g23)
FEATURE [Part::Extrusion] Extrude038  label="removeToCreateFanGrillHoles001"
  Base = -> Sketch047
  Dir = (0,-1,6e-16)
  DirMode = 2
  FaceMakerClass = Part::FaceMakerBullseye
  LengthFwd = 10
  LengthRev = 0
  Placement = pos=(65.4,44,54.82) rot=(0,0,1;0rad)
  Solid = true
  Symmetric = false
FEATURE [Part::Feature] Wire004
  shape: bbox 11 x 5.2 x 2e-07 mm, 0 faces, 0 solids (baked)
FEATURE [Part::Revolution] Revolve095
  Angle = 360
  Axis = (0,1,0)
  Base = (0,0,0)
  FaceMakerClass = Part::FaceMakerBullseye
  Placement = pos=(30.3,38,19.7) rot=(0,0,1;0rad)
  Solid = true
  Source = -> Wire004
  Symmetric = false
FEATURE [Part::Feature] Wire005
  shape: bbox 11 x 5.2 x 2e-07 mm, 0 faces, 0 solids (baked)
FEATURE [Part::Revolution] Revolve096
  Angle = 360
  Axis = (0,1,0)
  Base = (0,0,0)
  FaceMakerClass = Part::FaceMakerBullseye
  Placement = pos=(30.3,38,51.7) rot=(0,0,1;0rad)
  Solid = true
  Source = -> Wire005
  Symmetric = false
FEATURE [Part::Feature] Wire006
  shape: bbox 11 x 5.2 x 2e-07 mm, 0 faces, 0 solids (baked)
FEATURE [Part::Revolution] Revolve097
  Angle = 360
  Axis = (0,1,0)
  Base = (0,0,0)
  FaceMakerClass = Part::FaceMakerBullseye
  Placement = pos=(62.3,38,51.7) rot=(0,0,1;0rad)
  Solid = true
  Source = -> Wire006
  Symmetric = false
FEATURE [Part::Feature] Wire007
  shape: bbox 11 x 5.2 x 2e-07 mm, 0 faces, 0 solids (baked)
FEATURE [Part::Revolution] Revolve098
  Angle = 360
  Axis = (0,1,0)
  Base = (0,0,0)
  FaceMakerClass = Part::FaceMakerBullseye
  Placement = pos=(62.3,38,19.7) rot=(0,0,1;0rad)
  Solid = true
  Source = -> Wire007
  Symmetric = false
FEATURE [Part::MultiFuse] Fusion067  label="fanScrewHousing002"
  Shapes = -> [Revolve098,Revolve097,Revolve096,Revolve095]
FEATURE [Part::Feature] Face091 .. Face094  x4 (patterned run collapsed; names and placements below)
  shape: bbox 3.5 x 17.8 x 2e-07 mm, 1 faces, 0 solids (baked)
FEATURE [Part::Revolution] Revolve099  label="removeToCreateScrewAndThreadedInsertHole026"
  Angle = 360
  Axis = (0,1,0)
  Base = (0,0,0)
  FaceMakerClass = Part::FaceMakerBullseye
  Placement = pos=(62.3,30.3,19.7) rot=(0,0,1;0rad)
  Solid = false
  Source = -> Face091
  Symmetric = false
FEATURE [Part::Revolution] Revolve100  label="removeToCreateScrewAndThreadedInsertHole027"
  Angle = 360
  Axis = (0,1,0)
  Base = (0,0,0)
  FaceMakerClass = Part::FaceMakerBullseye
  Placement = pos=(62.3,30.3,51.7) rot=(0,0,1;0rad)
  Solid = false
  Source = -> Face092
  Symmetric = false
FEATURE [Part::Revolution] Revolve101  label="removeToCreateScrewAndThreadedInsertHole028"
  Angle = 360
  Axis = (0,1,0)
  Base = (0,0,0)
  FaceMakerClass = Part::FaceMakerBullseye
  Placement = pos=(30.3,30.3,19.7) rot=(0,0,1;0rad)
  Solid = false
  Source = -> Face093
  Symmetric = false
FEATURE [Part::Revolution] Revolve102  label="removeToCreateScrewAndThreadedInsertHole029"
  Angle = 360
  Axis = (0,1,0)
  Base = (0,0,0)
  FaceMakerClass = Part::FaceMakerBullseye
  Placement = pos=(30.3,30.3,51.7) rot=(0,0,1;0rad)
  Solid = false
  Source = -> Face094
  Symmetric = false
FEATURE [Part::MultiFuse] Fusion068  label="createThreadedInsertHolesForFan002"
  Shapes = -> [Revolve099,Revolve100,Revolve101,Revolve102]
FEATURE [Part::Cut] Cut026  label="fanScrewHousing003"
  Base = -> Fusion067
  Tool = -> Fusion068
FEATURE [Sketcher::SketchObject] Sketch048
  FullyConstrained = false
  Placement = pos=(0,0,0) rot=(1,0,0;1.5708rad)
  sketch-geometry (24):
    g0: ArcOfCircle CenterX=-4 CenterY=-10.5 CenterZ=0 NormalX=0 NormalY=0 NormalZ=1 AngleXU=0 Radius=1.5 StartAngle=6e-16 EndAngle=3.14159
    g1: ArcOfCircle CenterX=-34.2 CenterY=-10.5 CenterZ=0 NormalX=0 NormalY=0 NormalZ=1 AngleXU=0 Radius=1.5 StartAngle=0 EndAngle=3.14159
    g2: ArcOfCircle CenterX=-34.2 CenterY=-27.7 CenterZ=0 NormalX=0 NormalY=0 NormalZ=1 AngleXU=0 Radius=1.5 StartAngle=3.14159 EndAngle=6.28319
    g3: ArcOfCircle CenterX=-4 CenterY=-27.7 CenterZ=0 NormalX=0 NormalY=0 NormalZ=1 AngleXU=0 Radius=1.5 StartAngle=3.1416 EndAngle=6.28319
    g4: ArcOfCircle CenterX=-10 CenterY=-4.3 CenterZ=0 NormalX=0 NormalY=0 NormalZ=1 AngleXU=0 Radius=1.5 StartAngle=2e-16 EndAngle=3.14159
    g5: ArcOfCircle CenterX=-16.1 CenterY=-1.8 CenterZ=0 NormalX=0 NormalY=0 NormalZ=1 AngleXU=0 Radius=1.5 StartAngle=5e-16 EndAngle=3.14159
    g6: ArcOfCircle CenterX=-22.1 CenterY=-1.8 CenterZ=0 NormalX=0 NormalY=0 NormalZ=1 AngleXU=0 Radius=1.5 StartAngle=5e-16 EndAngle=3.14159
    g7: ArcOfCircle CenterX=-28.2 CenterY=-4.3 CenterZ=0 NormalX=0 NormalY=0 NormalZ=1 AngleXU=0 Radius=1.5 StartAngle=2e-16 EndAngle=3.14159
    g8: ArcOfCircle CenterX=-10 CenterY=-33.9 CenterZ=0 NormalX=0 NormalY=0 NormalZ=1 AngleXU=0 Radius=1.5 StartAngle=3.14159 EndAngle=6.28319
    g9: ArcOfCircle CenterX=-16.1 CenterY=-36.4 CenterZ=0 NormalX=0 NormalY=0 NormalZ=1 AngleXU=0 Radius=1.5 StartAngle=3.14159 EndAngle=6.28319
    g10: ArcOfCircle CenterX=-22.1 CenterY=-36.4 CenterZ=0 NormalX=0 NormalY=0 NormalZ=1 AngleXU=0 Radius=1.5 StartAngle=3.14159 EndAngle=6.28319
    g11: ArcOfCircle CenterX=-28.2 CenterY=-33.9 CenterZ=0 NormalX=0 NormalY=0 NormalZ=1 AngleXU=0 Radius=1.5 StartAngle=3.14159 EndAngle=6.28319
    g12: LineSegment StartX=-35.7 StartY=-10.5 StartZ=0 EndX=-35.7 EndY=-27.7 EndZ=0
    g13: LineSegment StartX=-32.7 StartY=-10.5 StartZ=0 EndX=-32.7 EndY=-27.7 EndZ=0
    g14: LineSegment StartX=-29.7 StartY=-33.9 StartZ=0 EndX=-29.7 EndY=-4.3 EndZ=0
    g15: LineSegment StartX=-26.7 StartY=-33.9 StartZ=0 EndX=-26.7 EndY=-4.3 EndZ=0
    g16: LineSegment StartX=-2.5 StartY=-10.5 StartZ=0 EndX=-2.5 EndY=-27.7 EndZ=0
    g17: LineSegment StartX=-8.5 StartY=-4.3 StartZ=0 EndX=-8.5 EndY=-33.9 EndZ=0
    g18: LineSegment StartX=-5.5 StartY=-10.5 StartZ=0 EndX=-5.5 EndY=-27.7 EndZ=0
    g19: LineSegment StartX=-11.5 StartY=-4.3 StartZ=0 EndX=-11.5 EndY=-33.9 EndZ=0
    g20: LineSegment StartX=-14.6 StartY=-1.8 StartZ=0 EndX=-14.6 EndY=-36.4 EndZ=0
    g21: LineSegment StartX=-17.6 StartY=-1.8 StartZ=0 EndX=-17.6 EndY=-36.4 EndZ=0
    g22: LineSegment StartX=-20.6 StartY=-36.4 StartZ=0 EndX=-20.6 EndY=-1.8 EndZ=0
    g23: LineSegment StartX=-23.6 StartY=-1.8 StartZ=0 EndX=-23.6 EndY=-36.4 EndZ=0
  constraints (48):
    c: Block(g0)
    c: Block(g1)
    c: Block(g2)
    c: Block(g3)
    c: Block(g4)
    c: Block(g5)
    c: Block(g6)
    c: Block(g7)
    c: Block(g8)
    c: Block(g9)
    c: Block(g10)
    c: Block(g11)
    c: Coincident(g12,g1)
    c: Coincident(g12,g2)
    c: Vertical(g12)
    c: Coincident(g13,g1)
    c: Coincident(g13,g2)
    c: Vertical(g13)
    c: Coincident(g14,g11)
    c: Coincident(g14,g7)
    c: Vertical(g14)
    c: Coincident(g15,g11)
    c: Coincident(g15,g7)
    c: Vertical(g15)
    c: Coincident(g16,g0)
    c: Coincident(g16,g3)
    c: Vertical(g16)
    c: Coincident(g17,g4)
    c: Coincident(g17,g8)
    c: Vertical(g17)
    c: Coincident(g18,g0)
    c: Coincident(g18,g3)
    c: Vertical(g18)
    c: Coincident(g19,g4)
    c: Coincident(g19,g8)
    c: Vertical(g19)
    c: Coincident(g20,g5)
    c: Coincident(g20,g9)
    c: Vertical(g20)
    c: Coincident(g21,g5)
    c: Coincident(g21,g9)
    c: Vertical(g21)
    c: Coincident(g22,g10)
    c: Coincident(g22,g6)
    c: Vertical(g22)
    c: Coincident(g23,g6)
    c: Coincident(g23,g10)
    c: Vertical(g23)
FEATURE [Part::Extrusion] Extrude039  label="removeToCreateFanGrillHoles002"
  Base = -> Sketch048
  Dir = (0,-1,6e-16)
  DirMode = 2
  FaceMakerClass = Part::FaceMakerBullseye
  LengthFwd = 10
  LengthRev = 0
  Placement = pos=(65.4,44,54.82) rot=(0,0,1;0rad)
  Solid = true
  Symmetric = false
FEATURE [Part::Cut] Cut027  label="fanScrewHousing004"
  Base = -> Cut026
  Tool = -> Extrude038
FEATURE [Part::Cut] Cut028  label="top014"
  Base = -> Fillet026
  Tool = -> Extrude039
FEATURE [Part::Feature] Face095 .. Face098  x4 (patterned run collapsed; names and placements below)
  shape: bbox 3.5 x 17.8 x 2e-07 mm, 1 faces, 0 solids (baked)
FEATURE [Part::Revolution] Revolve103  label="removeToCreateScrewAndThreadedInsertHole030"
  Angle = 360
  Axis = (0,1,0)
  Base = (0,0,0)
  FaceMakerClass = Part::FaceMakerBullseye
  Placement = pos=(62.3,30.3,19.7) rot=(0,0,1;0rad)
  Solid = false
  Source = -> Face095
  Symmetric = false
FEATURE [Part::Revolution] Revolve104  label="removeToCreateScrewAndThreadedInsertHole031"
  Angle = 360
  Axis = (0,1,0)
  Base = (0,0,0)
  FaceMakerClass = Part::FaceMakerBullseye
  Placement = pos=(62.3,30.3,51.7) rot=(0,0,1;0rad)
  Solid = false
  Source = -> Face096
  Symmetric = false
FEATURE [Part::Revolution] Revolve105  label="removeToCreateScrewAndThreadedInsertHole032"
  Angle = 360
  Axis = (0,1,0)
  Base = (0,0,0)
  FaceMakerClass = Part::FaceMakerBullseye
  Placement = pos=(30.3,30.3,19.7) rot=(0,0,1;0rad)
  Solid = false
  Source = -> Face097
  Symmetric = false
FEATURE [Part::Revolution] Revolve106  label="removeToCreateScrewAndThreadedInsertHole033"
  Angle = 360
  Axis = (0,1,0)
  Base = (0,0,0)
  FaceMakerClass = Part::FaceMakerBullseye
  Placement = pos=(30.3,30.3,51.7) rot=(0,0,1;0rad)
  Solid = false
  Source = -> Face098
  Symmetric = false
FEATURE [Part::MultiFuse] Fusion069  label="createThreadedInsertHolesForFan003"
  Shapes = -> [Revolve103,Revolve104,Revolve105,Revolve106]
FEATURE [Part::Cut] Cut029  label="top015"
  Base = -> Cut028
  Tool = -> Fusion054
FEATURE [Part::Cut] Cut030  label="fanScrewHousing005"
  Base = -> Cut027
  Tool = -> Fusion069
FEATURE [Part::Cylinder] Cylinder026  label="removeToCreteHoleForPlugHousing010"
  Angle = 360
  AttacherType = Attacher::AttachEngine3D
  Height = 20
  Placement = pos=(-2,19,36) rot=(0,1,0;1.5708rad)
  Radius = 14.3
FEATURE [Part::Box] Box018  label="removeToCreteHoleForPlugHousing011"
  AttacherType = Attacher::AttachEngine3D
  Height = 28.6
  Length = 10
  Placement = pos=(-2,0,21.7) rot=(0,0,1;0rad)
  Width = 19
FEATURE [Part::Box] Box019  label="wireHolderBottomCaseBit"
  AttacherType = Attacher::AttachEngine3D
  Height = 28
  Length = 3
  Placement = pos=(0,0,22) rot=(0,0,1;0rad)
  Width = 21
FEATURE [Part::Cylinder] Cylinder027  label="removeToCreteHoleForPlugHousing012"
  Angle = 360
  AttacherType = Attacher::AttachEngine3D
  Height = 20
  Placement = pos=(-2,19,36) rot=(0,1,0;1.5708rad)
  Radius = 14.3
FEATURE [Part::Cut] Cut031  label="wireHolderBottomCaseBit001"
  Base = -> Box019
  Tool = -> Cylinder027
FEATURE [Part::MultiFuse] Fusion070  label="removeToCreteHoleForPlugHousing013"
  Shapes = -> [Box018,Cylinder026]
FEATURE [Part::Cut] Cut032  label="top016"
  Base = -> Cut029
  Tool = -> Fusion070
FEATURE [Part::Cylinder] Cylinder028
  Angle = 360
  AttacherType = Attacher::AttachEngine3D
  Height = 20
  Placement = pos=(0,0,36.15) rot=(0,0,1;0rad)
  Radius = 14.3
FEATURE [Part::Cylinder] Cylinder029
  Angle = 360
  AttacherType = Attacher::AttachEngine3D
  Height = 10
  Placement = pos=(0,0,36.15) rot=(0,0,1;0rad)
  Radius = 4
FEATURE [Part::MultiFuse] Fusion071  label="removeToCreteHoleForPlugHousing014"
  Placement = pos=(70,19,36) rot=(0,1,0;1.5708rad)
  Shapes = -> [Cylinder028,Cylinder029]
FEATURE [Sketcher::SketchObject] Sketch049  label="topSketch011"
  FullyConstrained = true
  sketch-geometry (4):
    g0: ArcOfCircle CenterX=105 CenterY=19 CenterZ=0 NormalX=0 NormalY=0 NormalZ=1 AngleXU=0 Radius=20.6155 StartAngle=5.54125 EndAngle=6.28319
    g1: ArcOfCircle CenterX=105 CenterY=19 CenterZ=0 NormalX=0 NormalY=0 NormalZ=1 AngleXU=0 Radius=13 StartAngle=5.54125 EndAngle=6.28319
    g2: LineSegment StartX=118 StartY=19 StartZ=0 EndX=125.616 EndY=19 EndZ=0
    g3: LineSegment StartX=114.583 StartY=10.2157 StartZ=0 EndX=120.197 EndY=5.06982 EndZ=0
  constraints (7):
    c: Block(g0)
    c: Block(g1)
    c: Coincident(g2,g1)
    c: Coincident(g2,g0)
    c: Horizontal(g2)
    c: Coincident(g3,g1)
    c: Coincident(g3,g0)
FEATURE [Part::Box] Box020  label="removeToCreteHoleForPlugHousing015"
  AttacherType = Attacher::AttachEngine3D
  Height = 28.6
  Length = 20
  Placement = pos=(106.15,0,21.7) rot=(0,0,1;0rad)
  Width = 19
FEATURE [Part::MultiFuse] Fusion072  label="removeToCreteHoleForPlugHousing016"
  Shapes = -> [Box020,Fusion071]
FEATURE [Part::Cut] Cut033  label="removeToCreteHoleForPlugHousing017"
  Base = -> Cut032
  Tool = -> Fusion072
FEATURE [Part::Cylinder] Cylinder030
  Angle = 360
  AttacherType = Attacher::AttachEngine3D
  Height = 20
  Placement = pos=(0,0,36.15) rot=(0,0,1;0rad)
  Radius = 14.3
FEATURE [Part::Cylinder] Cylinder031
  Angle = 360
  AttacherType = Attacher::AttachEngine3D
  Height = 10
  Placement = pos=(0,0,36.15) rot=(0,0,1;0rad)
  Radius = 4
FEATURE [Part::Box] Box021  label="removeToCreteHoleForPlugHousing019"
  AttacherType = Attacher::AttachEngine3D
  Height = 28.6
  Length = 20
  Placement = pos=(106.15,0,21.7) rot=(0,0,1;0rad)
  Width = 19
FEATURE [Part::MultiFuse] Fusion074  label="removeToCreteHoleForPlugHousing020"
  Placement = pos=(70,19,36) rot=(0,1,0;1.5708rad)
  Shapes = -> [Cylinder030,Cylinder031]
FEATURE [Part::MultiFuse] Fusion073  label="removeToCreteHoleForPlugHousing018"
  Placement = pos=(0,0,28.3) rot=(0,0,1;0rad)
  Shapes = -> [Box021,Fusion074]
FEATURE [Part::Cylinder] Cylinder032
  Angle = 360
  AttacherType = Attacher::AttachEngine3D
  Height = 20
  Placement = pos=(0,0,36.15) rot=(0,0,1;0rad)
  Radius = 14.3
FEATURE [Part::Cylinder] Cylinder033
  Angle = 360
  AttacherType = Attacher::AttachEngine3D
  Height = 10
  Placement = pos=(0,0,36.15) rot=(0,0,1;0rad)
  Radius = 4
FEATURE [Part::Box] Box022  label="removeToCreteHoleForPlugHousing021"
  AttacherType = Attacher::AttachEngine3D
  Height = 28.6
  Length = 20
  Placement = pos=(106.15,0,21.7) rot=(0,0,1;0rad)
  Width = 19
FEATURE [Part::MultiFuse] Fusion076  label="removeToCreteHoleForPlugHousing023"
  Placement = pos=(70,19,36) rot=(0,1,0;1.5708rad)
  Shapes = -> [Cylinder032,Cylinder033]
FEATURE [Part::MultiFuse] Fusion075  label="removeToCreteHoleForPlugHousing022"
  Placement = pos=(0,0,-28.3) rot=(0,0,1;0rad)
  Shapes = -> [Box022,Fusion076]
FEATURE [Part::MultiFuse] Fusion077  label="removeToCreatePlugHousingBottomBit"
  Shapes = -> [Fusion075,Fusion073]
FEATURE [Part::Cylinder] Cylinder034
  Angle = 360
  AttacherType = Attacher::AttachEngine3D
  Height = 20
  Placement = pos=(0,0,36.15) rot=(0,0,1;0rad)
  Radius = 14
FEATURE [Part::Cylinder] Cylinder035
  Angle = 360
  AttacherType = Attacher::AttachEngine3D
  Height = 10
  Placement = pos=(0,0,36.15) rot=(0,0,1;0rad)
  Radius = 4
FEATURE [Part::MultiFuse] Fusion078  label="removeToCreteHoleForPlugHousing024"
  Placement = pos=(70,19,36) rot=(0,1,0;1.5708rad)
  Shapes = -> [Cylinder034,Cylinder035]
FEATURE [Part::MultiFuse] Fusion079  label="removeToCreatePlugHousingBottomBit001"
  Shapes = -> [Fusion078,Fusion077]
FEATURE [Part::Extrusion] Extrude040  label="bottomPlugHousingBit"
  Base = -> Sketch049
  Dir = (0,0,1)
  DirMode = 2
  FaceMakerClass = Part::FaceMakerBullseye
  LengthFwd = 72
  LengthRev = 0
  Solid = true
  Symmetric = false
FEATURE [Part::Cut] Cut034  label="bottomPlugHousingBit001"
  Base = -> Extrude040
  Placement = pos=(-0.09,0,0) rot=(0,0,1;0rad)
  Tool = -> Fusion079
FEATURE [Part::Box] Box023  label="Cube014"
  AttacherType = Attacher::AttachEngine3D
  Height = 16
  Length = 8
  Placement = pos=(12.7,31.52,28) rot=(0,0,1;0rad)
  Width = 4
FEATURE [Part::Cylinder] Cylinder036
  Angle = 360
  AttacherType = Attacher::AttachEngine3D
  Height = 10
  Placement = pos=(0,0,36.15) rot=(0,0,1;0rad)
  Radius = 4
FEATURE [Part::Cylinder] Cylinder037
  Angle = 360
  AttacherType = Attacher::AttachEngine3D
  Height = 20
  Placement = pos=(0,0,36.15) rot=(0,0,1;0rad)
  Radius = 8.2
FEATURE [Part::MultiFuse] Fusion080  label="removeToCreteHoleForPlugHousing025"
  Placement = pos=(-42,19,36) rot=(0,1,0;1.5708rad)
  Shapes = -> [Cylinder037,Cylinder036]
FEATURE [Sketcher::SketchObject] Sketch050  label="topSketch012"
  FullyConstrained = true
  sketch-geometry (4):
    g0: LineSegment StartX=16.8446 StartY=31.512 StartZ=0 EndX=16.3251 EndY=34.4666 EndZ=0
    g1: ArcOfCircle CenterX=19 CenterY=19.2524 CenterZ=0 NormalX=0 NormalY=0 NormalZ=1 AngleXU=0 Radius=15.4476 StartAngle=1.74483 EndAngle=2.72717
    g2: ArcOfCircle CenterX=19 CenterY=19.2524 CenterZ=0 NormalX=0 NormalY=0 NormalZ=1 AngleXU=0 Radius=12.4476 StartAngle=1.74483 EndAngle=2.73189
    g3: LineSegment StartX=4.86004 StartY=25.4725 StartZ=0 EndX=7.58253 EndY=24.2107 EndZ=0
  constraints (7):
    c: Block(g0)
    c: Coincident(g1,g0)
    c: Coincident(g2,g0)
    c: Coincident(g3,g1)
    c: Coincident(g3,g2)
    c: Block(g1)
    c: Block(g2)
FEATURE [Part::Extrusion] Extrude041
  Base = -> Sketch050
  Dir = (0,0,1)
  DirMode = 2
  FaceMakerClass = Part::FaceMakerBullseye
  LengthFwd = 10.6
  LengthRev = 0
  Placement = pos=(0,0,31) rot=(0,0,1;0rad)
  Solid = true
  Symmetric = false
FEATURE [Part::Cut] Cut035
  Base = -> Extrude041
  Placement = pos=(0,0,-0.3) rot=(0,0,1;0rad)
  Tool = -> Fusion080
FEATURE [Part::Cut] Cut036
  Base = -> Box023
  Tool = -> Cut035
FEATURE [Part::Fillet] Fillet027
  Base = -> Cut036
  Edges = 1 edges r=0.7: [Edge13]
FEATURE [Part::Fillet] Fillet028
  Base = -> Fillet027
  Edges = 1 edges r=0.7: [Edge13]
FEATURE [Part::Fillet] Fillet029
  Base = -> Fillet028
  Edges = 1 edges r=0.7: [Edge16]
FEATURE [Part::Fillet] Fillet030
  Base = -> Fillet029
  Edges = 1 edges r=0.7: [Edge11]
FEATURE [Part::Fillet] Fillet031
  Base = -> Fillet030
  Edges = 1 edges r=0.7: [Edge10]
FEATURE [Part::Fillet] Fillet032
  Base = -> Fillet031
  Edges = 1 edges r=1.2: [Edge5]
FEATURE [Part::Fillet] Fillet033
  Base = -> Fillet032
  Edges = 1 edges r=1.2: [Edge12]
FEATURE [Part::Fillet] Fillet034  label="wireHousingRetainer"
  Base = -> Fillet033
  Edges = 1 edges r=2: [Edge1]
  Placement = pos=(0.3,0,0) rot=(0,0,1;0rad)
FEATURE [Part::Feature] Face099
  shape: bbox 3.5 x 17.8 x 2e-07 mm, 1 faces, 0 solids (baked)
FEATURE [Part::Revolution] Revolve107  label="removeToCreateScrewAndThreadedInsertHole034"
  Angle = 360
  Axis = (0,1,0)
  Base = (0,0,0)
  FaceMakerClass = Part::FaceMakerBullseye
  Placement = pos=(12.5,0,10) rot=(0,0,1;0rad)
  Solid = false
  Source = -> Face099
  Symmetric = false
FEATURE [Part::Feature] Face100
  shape: bbox 3.5 x 17.8 x 2e-07 mm, 1 faces, 0 solids (baked)
FEATURE [Part::Revolution] Revolve108  label="removeToCreateScrewAndThreadedInsertHole035"
  Angle = 360
  Axis = (0,1,0)
  Base = (0,0,0)
  FaceMakerClass = Part::FaceMakerBullseye
  Placement = pos=(12.5,0,62) rot=(0,0,1;0rad)
  Solid = false
  Source = -> Face100
  Symmetric = false
FEATURE [Part::Feature] Face101
  shape: bbox 3.5 x 17.8 x 2e-07 mm, 1 faces, 0 solids (baked)
FEATURE [Part::Revolution] Revolve109  label="removeToCreateScrewAndThreadedInsertHole036"
  Angle = 360
  Axis = (0,1,0)
  Base = (0,0,0)
  FaceMakerClass = Part::FaceMakerBullseye
  Placement = pos=(89.5,0,68.5) rot=(0,0,1;0rad)
  Solid = false
  Source = -> Face101
  Symmetric = false
FEATURE [Part::Feature] Face102
  shape: bbox 3.5 x 17.8 x 2e-07 mm, 1 faces, 0 solids (baked)
FEATURE [Part::Revolution] Revolve110  label="removeToCreateScrewAndThreadedInsertHole037"
  Angle = 360
  Axis = (0,1,0)
  Base = (0,0,0)
  FaceMakerClass = Part::FaceMakerBullseye
  Placement = pos=(89.5,0,3.5) rot=(0,0,1;0rad)
  Solid = false
  Source = -> Face102
  Symmetric = false
FEATURE [Part::Feature] Face103
  shape: bbox 3.5 x 17.8 x 2e-07 mm, 1 faces, 0 solids (baked)
FEATURE [Part::Revolution] Revolve111  label="removeToCreateScrewAndThreadedInsertHole038"
  Angle = 360
  Axis = (0,1,0)
  Base = (0,0,0)
  FaceMakerClass = Part::FaceMakerBullseye
  Placement = pos=(109.5,4.7,3.5) rot=(0,0,1;0rad)
  Solid = false
  Source = -> Face103
  Symmetric = false
FEATURE [Part::Feature] Face104
  shape: bbox 3.5 x 17.8 x 2e-07 mm, 1 faces, 0 solids (baked)
FEATURE [Part::Revolution] Revolve112  label="removeToCreateScrewAndThreadedInsertHole039"
  Angle = 360
  Axis = (0,1,0)
  Base = (0,0,0)
  FaceMakerClass = Part::FaceMakerBullseye
  Placement = pos=(109.5,4.7,68.5) rot=(0,0,1;0rad)
  Solid = false
  Source = -> Face104
  Symmetric = false
FEATURE [Part::MultiFuse] Fusion081  label="removeToCreateScrewAndThreadedInsertHole040"
  Shapes = -> [Revolve107,Revolve108,Revolve109,Revolve110,Revolve111,Revolve112]
FEATURE [Part::MultiFuse] Fusion082  label="casePillars002"
  Shapes = -> [Revolve094,Revolve092,Revolve090,Revolve089,Revolve091,Revolve093]
FEATURE [Part::Cut] Cut037  label="casePillars003"
  Base = -> Fusion082
  Tool = -> Fusion081
FEATURE [Sketcher::SketchObject] Sketch051
  FullyConstrained = true
  Placement = pos=(117,19,0) rot=(0.57735,0.57735,0.57735;2.0944rad)
  sketch-geometry (48):
    g0: LineSegment StartX=-49.19 StartY=69.25 StartZ=0 EndX=-49.19 EndY=66.25 EndZ=0
    g1: LineSegment StartX=-49.19 StartY=63.5 StartZ=0 EndX=-49.19 EndY=60.5 EndZ=0
    g2: LineSegment StartX=-49.19 StartY=57.75 StartZ=0 EndX=-49.19 EndY=54.75 EndZ=0
    g3: LineSegment StartX=-49.19 StartY=52 StartZ=0 EndX=-49.19 EndY=49 EndZ=0
    g4: LineSegment StartX=-49.19 StartY=46.25 StartZ=0 EndX=-49.19 EndY=43.25 EndZ=0
    g5: LineSegment StartX=-49.19 StartY=40.5 StartZ=0 EndX=-49.19 EndY=37.5 EndZ=0
    g6: LineSegment StartX=-49.19 StartY=34.5 StartZ=0 EndX=-49.19 EndY=31.5 EndZ=0
    g7: LineSegment StartX=-49.19 StartY=28.75 StartZ=0 EndX=-49.19 EndY=25.75 EndZ=0
    g8: LineSegment StartX=-49.19 StartY=23 StartZ=0 EndX=-49.19 EndY=20 EndZ=0
    g9: LineSegment StartX=-49.19 StartY=17.25 StartZ=0 EndX=-49.19 EndY=14.25 EndZ=0
    g10: LineSegment StartX=-49.19 StartY=11.5 StartZ=0 EndX=-49.19 EndY=8.5 EndZ=0
    g11: LineSegment StartX=-49.19 StartY=5.75 StartZ=0 EndX=-49.19 EndY=2.75 EndZ=0
    g12: ArcOfCircle CenterX=-1.5 CenterY=67.75 CenterZ=0 NormalX=0 NormalY=0 NormalZ=1 AngleXU=0 Radius=1.5 StartAngle=4.71239 EndAngle=7.85398
    g13: ArcOfCircle CenterX=-1.5 CenterY=62 CenterZ=0 NormalX=0 NormalY=0 NormalZ=1 AngleXU=0 Radius=1.5 StartAngle=4.71239 EndAngle=7.85398
    g14: ArcOfCircle CenterX=-1.5 CenterY=56.25 CenterZ=0 NormalX=0 NormalY=0 NormalZ=1 AngleXU=0 Radius=1.5 StartAngle=4.71239 EndAngle=7.85398
    g15: ArcOfCircle CenterX=-11.49 CenterY=50.5 CenterZ=0 NormalX=0 NormalY=0 NormalZ=1 AngleXU=0 Radius=1.5 StartAngle=4.71239 EndAngle=7.85398
    g16: ArcOfCircle CenterX=-16.28 CenterY=44.75 CenterZ=0 NormalX=0 NormalY=0 NormalZ=1 AngleXU=0 Radius=1.5 StartAngle=4.71239 EndAngle=7.85398
    g17: ArcOfCircle CenterX=-18.2337 CenterY=39 CenterZ=0 NormalX=0 NormalY=0 NormalZ=1 AngleXU=0 Radius=1.5 StartAngle=4.71485 EndAngle=7.85398
    g18: ArcOfCircle CenterX=-16.2837 CenterY=27.25 CenterZ=0 NormalX=0 NormalY=0 NormalZ=1 AngleXU=0 Radius=1.5 StartAngle=4.71485 EndAngle=7.85398
    g19: ArcOfCircle CenterX=-18.2337 CenterY=33 CenterZ=0 NormalX=0 NormalY=0 NormalZ=1 AngleXU=0 Radius=1.5 StartAngle=4.71485 EndAngle=7.85398
    g20: ArcOfCircle CenterX=-11.49 CenterY=21.5 CenterZ=0 NormalX=0 NormalY=0 NormalZ=1 AngleXU=0 Radius=1.5 StartAngle=4.71239 EndAngle=7.85398
    g21: ArcOfCircle CenterX=-1.5 CenterY=4.25 CenterZ=0 NormalX=0 NormalY=0 NormalZ=1 AngleXU=0 Radius=1.5 StartAngle=4.71239 EndAngle=7.85398
    g22: ArcOfCircle CenterX=-1.5 CenterY=10 CenterZ=0 NormalX=0 NormalY=0 NormalZ=1 AngleXU=0 Radius=1.5 StartAngle=4.71239 EndAngle=7.85398
    g23: ArcOfCircle CenterX=-1.5 CenterY=15.75 CenterZ=0 NormalX=0 NormalY=0 NormalZ=1 AngleXU=0 Radius=1.5 StartAngle=4.71239 EndAngle=7.85398
    g24: LineSegment StartX=-49.19 StartY=69.25 StartZ=0 EndX=-1.5 EndY=69.25 EndZ=0
    g25: LineSegment StartX=-49.19 StartY=66.25 StartZ=0 EndX=-1.5 EndY=66.25 EndZ=0
    g26: LineSegment StartX=-49.19 StartY=63.5 StartZ=0 EndX=-1.5 EndY=63.5 EndZ=0
    g27: LineSegment StartX=-49.19 StartY=60.5 StartZ=0 EndX=-1.5 EndY=60.5 EndZ=0
    g28: LineSegment StartX=-49.19 StartY=57.75 StartZ=0 EndX=-1.5 EndY=57.75 EndZ=0
    g29: LineSegment StartX=-49.19 StartY=54.75 StartZ=0 EndX=-1.5 EndY=54.75 EndZ=0
    g30: LineSegment StartX=-49.19 StartY=52 StartZ=0 EndX=-11.49 EndY=52 EndZ=0
    g31: LineSegment StartX=-49.19 StartY=49 StartZ=0 EndX=-11.49 EndY=49 EndZ=0
    g32: LineSegment StartX=-49.19 StartY=46.25 StartZ=0 EndX=-16.28 EndY=46.25 EndZ=0
    g33: LineSegment StartX=-49.19 StartY=43.25 StartZ=0 EndX=-16.28 EndY=43.25 EndZ=0
    g34: LineSegment StartX=-49.19 StartY=40.5 StartZ=0 EndX=-18.2337 EndY=40.5 EndZ=0
    g35: LineSegment StartX=-49.19 StartY=37.5 StartZ=0 EndX=-18.23 EndY=37.5 EndZ=0
    g36: LineSegment StartX=-49.19 StartY=34.5 StartZ=0 EndX=-18.2337 EndY=34.5 EndZ=0
    g37: LineSegment StartX=-49.19 StartY=31.5 StartZ=0 EndX=-18.23 EndY=31.5 EndZ=0
    g38: LineSegment StartX=-49.19 StartY=28.75 StartZ=0 EndX=-16.2837 EndY=28.75 EndZ=0
    g39: LineSegment StartX=-49.19 StartY=25.75 StartZ=0 EndX=-16.28 EndY=25.75 EndZ=0
    g40: LineSegment StartX=-49.19 StartY=23 StartZ=0 EndX=-11.49 EndY=23 EndZ=0
    g41: LineSegment StartX=-49.19 StartY=20 StartZ=0 EndX=-11.49 EndY=20 EndZ=0
    g42: LineSegment StartX=-49.19 StartY=17.25 StartZ=0 EndX=-1.5 EndY=17.25 EndZ=0
    g43: LineSegment StartX=-49.19 StartY=14.25 StartZ=0 EndX=-1.5 EndY=14.25 EndZ=0
    g44: LineSegment StartX=-49.19 StartY=11.5 StartZ=0 EndX=-1.5 EndY=11.5 EndZ=0
    g45: LineSegment StartX=-49.19 StartY=8.5 StartZ=0 EndX=-1.5 EndY=8.5 EndZ=0
    g46: LineSegment StartX=-49.19 StartY=5.75 StartZ=0 EndX=-1.5 EndY=5.75 EndZ=0
    g47: LineSegment StartX=-49.19 StartY=2.75 StartZ=0 EndX=-1.5 EndY=2.75 EndZ=0
  constraints (120):
    c: Vertical(g0)
    c: Distance(g0) = 3
    c: Block(g0)
    c: Vertical(g1)
    c: Distance(g1) = 3
    c: Vertical(g2)
    c: Equal(g0,g2) = 3
    c: Block(g2)
    c: Vertical(g3)
    c: Equal(g1,g3) = 3
    c: Vertical(g4)
    c: Equal(g0,g4) = 3
    c: Block(g4)
    c: Vertical(g5)
    c: Equal(g1,g5) = 3
    c: Vertical(g6)
    c: Equal(g0,g6) = 3
    c: Block(g6)
    c: Vertical(g7)
    c: Equal(g1,g7) = 3
    c: Vertical(g8)
    c: Equal(g0,g8) = 3
    c: Block(g8)
    c: Vertical(g9)
    c: Equal(g1,g9) = 3
    c: Vertical(g10)
    c: Equal(g0,g10) = 3
    c: Block(g10)
    c: Vertical(g11)
    c: Equal(g1,g11) = 3
    c: Block(g12)
    c: Block(g13)
    c: Block(g14)
    c: Block(g15)
    c: Block(g16)
    c: Block(g17)
    c: Block(g18)
    c: Block(g19)
    c: Block(g20)
    c: Block(g21)
    c: Block(g22)
    c: Block(g23)
    c: Block(g11)
    c: Block(g9)
    c: Block(g7)
    c: Block(g5)
    c: Block(g3)
    c: Block(g1)
    c: Coincident(g24,g0)
    c: Coincident(g24,g12)
    c: Horizontal(g24)
    c: Coincident(g25,g0)
    c: Coincident(g25,g12)
    c: Horizontal(g25)
    c: Coincident(g26,g1)
    c: Coincident(g26,g13)
    c: Horizontal(g26)
    c: Coincident(g27,g1)
    c: Coincident(g27,g13)
    c: Horizontal(g27)
    c: Coincident(g28,g2)
    c: Coincident(g28,g14)
    c: Horizontal(g28)
    c: Coincident(g29,g2)
    c: Coincident(g29,g14)
    c: Horizontal(g29)
    c: Coincident(g30,g3)
    c: Coincident(g30,g15)
    c: Horizontal(g30)
    c: Coincident(g31,g3)
    c: Coincident(g31,g15)
    c: Horizontal(g31)
    c: Coincident(g32,g4)
    c: Coincident(g32,g16)
    c: Horizontal(g32)
    c: Coincident(g33,g4)
    c: Coincident(g33,g16)
    c: Horizontal(g33)
    c: Coincident(g34,g5)
    c: Coincident(g34,g17)
    c: Horizontal(g34)
    c: Coincident(g35,g5)
    c: Coincident(g35,g17)
    c: Horizontal(g35)
    c: Coincident(g36,g6)
    c: Coincident(g36,g19)
    c: Horizontal(g36)
    c: Coincident(g37,g6)
    c: Coincident(g37,g19)
    c: Horizontal(g37)
    c: Coincident(g38,g7)
    c: Coincident(g38,g18)
    c: Horizontal(g38)
    c: Coincident(g39,g7)
    c: Coincident(g39,g18)
    c: Horizontal(g39)
    c: Coincident(g40,g8)
    c: Coincident(g40,g20)
    c: Horizontal(g40)
    c: Coincident(g41,g8)
    c: Coincident(g41,g20)
    c: Horizontal(g41)
    c: Coincident(g42,g9)
    c: Coincident(g42,g23)
    c: Horizontal(g42)
    c: Coincident(g43,g9)
    c: Coincident(g43,g23)
    c: Horizontal(g43)
    c: Coincident(g44,g10)
    c: Coincident(g44,g22)
    c: Horizontal(g44)
    c: Coincident(g45,g10)
    c: Coincident(g45,g22)
    c: Horizontal(g45)
    c: Coincident(g46,g11)
    c: Coincident(g46,g21)
    c: Horizontal(g46)
    c: Coincident(g47,g11)
    c: Coincident(g47,g21)
    c: Horizontal(g47)
FEATURE [Part::Extrusion] Extrude042
  Base = -> Sketch051
  Dir = (1,-2e-16,2e-16)
  DirMode = 2
  FaceMakerClass = Part::FaceMakerBullseye
  LengthFwd = 19
  LengthRev = 0
  Placement = pos=(-19,0,0) rot=(0,0,1;0rad)
  Solid = true
  Symmetric = false
FEATURE [Part::Fillet] Fillet035  label="removeToCreateVentalationHoles"
  Base = -> Extrude042
  Edges = <same value as first occurrence — deduplicated (x5 in doc)>
  Placement = pos=(7,0,0) rot=(0,0,1;0rad)
FEATURE [Part::Cut] Cut038  label="top017"
  Base = -> Cut033
  Tool = -> Fillet035
FEATURE [Sketcher::SketchObject] Sketch052  label="bottomSketch001"
  FullyConstrained = true
  sketch-geometry (45):
    g0: LineSegment StartX=6.29999 StartY=8 StartZ=0 EndX=3.29999 EndY=8 EndZ=0
    g1: LineSegment StartX=3.29999 StartY=8 StartZ=0 EndX=3.29999 EndY=-6.03275e-07 EndZ=0
    g2: ArcOfCircle CenterX=8.29999 CenterY=5 CenterZ=0 NormalX=0 NormalY=0 NormalZ=1 AngleXU=0 Radius=2 StartAngle=3.14159 EndAngle=4.71239
    g3: LineSegment StartX=6.29999 StartY=8 StartZ=0 EndX=6.29999 EndY=5 EndZ=0
    g4: ArcOfCircle CenterX=105 CenterY=19 CenterZ=0 NormalX=0 NormalY=0 NormalZ=1 AngleXU=0 Radius=12.7 StartAngle=4.71239 EndAngle=5.94289
    g5-g11: Circle x7 (B-spline internal-alignment scaffolding for g12; pole/knot coordinates omitted)
    g12: BSplineCurve PolesCount=7 KnotsCount=5 Degree=3 IsPeriodic=0
    g13-g17: GeomPoint x5 (B-spline internal-alignment scaffolding for g12; pole/knot coordinates omitted)
    g18: ArcOfCircle CenterX=105 CenterY=19 CenterZ=0 NormalX=0 NormalY=0 NormalZ=1 AngleXU=0 Radius=15.7 StartAngle=5.81226 EndAngle=6.28319
    g19: BSplineCurve PolesCount=5 KnotsCount=3 Degree=3 IsPeriodic=0
    g20: LineSegment StartX=8.29999 StartY=3 StartZ=0 EndX=101.7 EndY=3 EndZ=0
    g21: LineSegment StartX=3.29999 StartY=-6.03275e-07 StartZ=0 EndX=105 EndY=-6.03275e-07 EndZ=0
    g22: LineSegment StartX=120.974 StartY=8.71251 StartZ=0 EndX=122.332 EndY=7.83778 EndZ=0
    g23: LineSegment StartX=105 StartY=-6.03274e-07 StartZ=0 EndX=113 EndY=-6.03274e-07 EndZ=0
    g24: ArcOfCircle CenterX=105 CenterY=19 CenterZ=0 NormalX=0 NormalY=0 NormalZ=1 AngleXU=0 Radius=20.6155 StartAngle=5.11091 EndAngle=5.71103
    g25: ArcOfCircle CenterX=117.7 CenterY=19 CenterZ=0 NormalX=0 NormalY=0 NormalZ=1 AngleXU=0 Radius=3 StartAngle=1.2e-15 EndAngle=2.10468
    g26: Circle CenterX=116.345 CenterY=16.3232 CenterZ=0 NormalX=0 NormalY=0 NormalZ=1 AngleXU=0 Radius=1
    g27: Circle CenterX=117.24 CenterY=15.7584 CenterZ=0 NormalX=0 NormalY=0 NormalZ=1 AngleXU=0 Radius=1
    g28: Circle CenterX=116.972 CenterY=14.7612 CenterZ=0 NormalX=0 NormalY=0 NormalZ=1 AngleXU=0 Radius=1
    g29: BSplineCurve PolesCount=3 KnotsCount=2 Degree=2 IsPeriodic=0
    g30: GeomPoint X=116.345 Y=16.3232 Z=0
    g31: GeomPoint X=116.972 Y=14.7612 Z=0
    g32: Circle CenterX=115.828 CenterY=17.157 CenterZ=0 NormalX=0 NormalY=0 NormalZ=1 AngleXU=0 Radius=1
    g33: Circle CenterX=115.841 CenterY=16.639 CenterZ=0 NormalX=0 NormalY=0 NormalZ=1 AngleXU=0 Radius=1
    g34: Circle CenterX=116.345 CenterY=16.3232 CenterZ=0 NormalX=0 NormalY=0 NormalZ=1 AngleXU=0 Radius=1
    g35: BSplineCurve PolesCount=3 KnotsCount=2 Degree=2 IsPeriodic=0
    g36: GeomPoint X=115.828 Y=17.157 Z=0
    g37: GeomPoint X=116.345 Y=16.3232 Z=0
    g38: LineSegment StartX=115.828 StartY=17.157 StartZ=0 EndX=115.828 EndY=20.8307 EndZ=0
    g39: Circle CenterX=115.828 CenterY=20.8307 CenterZ=0 NormalX=0 NormalY=0 NormalZ=1 AngleXU=0 Radius=1
    g40: Circle CenterX=115.831 CenterY=21.3396 CenterZ=0 NormalX=0 NormalY=0 NormalZ=1 AngleXU=0 Radius=1
    g41: Circle CenterX=116.173 CenterY=21.5825 CenterZ=0 NormalX=0 NormalY=0 NormalZ=1 AngleXU=0 Radius=1
    g42: BSplineCurve PolesCount=3 KnotsCount=2 Degree=2 IsPeriodic=0
    g43: GeomPoint X=115.828 Y=20.8307 Z=0
    g44: GeomPoint X=116.173 Y=21.5825 Z=0
  constraints (70):
    c: Horizontal(g0)
    c: Distance(g0) = 3
    c: Coincident(g1,g0)
    c: Vertical(g1)
    c: Block(g2)
    c: Block(g0)
    c: Coincident(g3,g0)
    c: Coincident(g3,g2)
    c: Vertical(g3)
    c: Block(g1)
    c: Block(g4)
    c: Coincident(g19,g4)
    c: Block(g19)
    c: Equal(g5, g6-g11) x6
    c: InternalAlignment(g5-g11 -> g12) x7
    c: InternalAlignment(g13-g17 -> g12) x5
    c: Block(g12)
    c: Coincident(g18,g12)
    c: Block(g18)
    c: Coincident(g20,g2)
    c: Coincident(g20,g19)
    c: Horizontal(g20)
    c: Distance(g20) = 93.4
    c: Coincident(g21,g1)
    c: Horizontal(g21)
    c: Distance(g21) = 101.7
    c: Horizontal(g23)
    c: Distance(g23) = 8
    c: Coincident(g24,g23)
    c: Block(g23)
    c: Coincident(g22,g24)
    c: Block(g24)
    c: Block(g22)
    c: Distance(g22) = 1.61553
    c: Coincident(g25,g18)
    c: Block(g25)
    c: Weight(g26) = 1
    c: Equal(g26,g27)
    c: Equal(g26,g28)
    c: Coincident(g29,g4)
    c: InternalAlignment(g26,g29)
    c: InternalAlignment(g27,g29)
    c: InternalAlignment(g28,g29)
    c: InternalAlignment(g30,g29)
    c: InternalAlignment(g31,g29)
    c: Block(g29)
    c: Weight(g32) = 1
    c: Equal(g32,g33)
    c: Equal(g32,g34)
    c: Coincident(g35,g29)
    c: InternalAlignment(g32,g35)
    c: InternalAlignment(g33,g35)
    c: InternalAlignment(g34,g35)
    c: InternalAlignment(g36,g35)
    c: InternalAlignment(g37,g35)
    c: Block(g35)
    c: Coincident(g38,g35)
    c: Vertical(g38)
    c: Block(g38)
    c: Coincident(g42,g38)
    c: Weight(g39) = 1
    c: Equal(g39,g40)
    c: Equal(g39,g41)
    c: Coincident(g42,g25)
    c: InternalAlignment(g39,g42)
    c: InternalAlignment(g40,g42)
    c: InternalAlignment(g41,g42)
    c: InternalAlignment(g43,g42)
    c: InternalAlignment(g44,g42)
    c: Block(g42)
FEATURE [Part::Extrusion] Extrude043  label="bottom010"
  Base = -> Sketch052
  Dir = (0,0,1)
  DirMode = 2
  FaceMakerClass = Part::FaceMakerBullseye
  LengthFwd = 71.4
  LengthRev = 0
  Placement = pos=(0,0,0.3) rot=(0,0,1;0rad)
  Solid = true
  Symmetric = false
FEATURE [Sketcher::SketchObject] Sketch053  label="topSketch013"
  FullyConstrained = true
  sketch-geometry (22):
    g0: LineSegment StartX=5.21097e-06 StartY=3 StartZ=0 EndX=5.21097e-06 EndY=19 EndZ=0
    g1: ArcOfCircle CenterX=19 CenterY=19 CenterZ=0 NormalX=0 NormalY=0 NormalZ=1 AngleXU=0 Radius=19 StartAngle=1.5708 EndAngle=3.14159
    g2: ArcOfCircle CenterX=19 CenterY=19 CenterZ=0 NormalX=0 NormalY=0 NormalZ=1 AngleXU=0 Radius=16 StartAngle=1.5708 EndAngle=3.14159
    g3: LineSegment StartX=114 StartY=35 StartZ=0 EndX=19 EndY=35 EndZ=0
    g4: LineSegment StartX=5.21097e-06 StartY=3 StartZ=0 EndX=5.21097e-06 EndY=0 EndZ=0
    g5: LineSegment StartX=3 StartY=0 StartZ=0 EndX=5.21097e-06 EndY=0 EndZ=0
    g6: LineSegment StartX=3 StartY=19 StartZ=0 EndX=3 EndY=0 EndZ=0
    g7: LineSegment StartX=19 StartY=38 StartZ=0 EndX=124 EndY=38 EndZ=0
    g8: Circle CenterX=119 CenterY=35 CenterZ=0 NormalX=0 NormalY=0 NormalZ=1 AngleXU=0 Radius=1
    g9: Circle CenterX=121 CenterY=35 CenterZ=0 NormalX=0 NormalY=0 NormalZ=1 AngleXU=0 Radius=1
    g10: Circle CenterX=121 CenterY=33 CenterZ=0 NormalX=0 NormalY=0 NormalZ=1 AngleXU=0 Radius=1
    g11: BSplineCurve PolesCount=3 KnotsCount=2 Degree=2 IsPeriodic=0
    g12: GeomPoint X=119 Y=35 Z=0
    g13: GeomPoint X=121 Y=33 Z=0
    g14: LineSegment StartX=119 StartY=35 StartZ=0 EndX=114 EndY=35 EndZ=0
    g15: ArcOfCircle CenterX=105 CenterY=19 CenterZ=0 NormalX=0 NormalY=0 NormalZ=1 AngleXU=0 Radius=16 StartAngle=5.60905 EndAngle=6.28319
    g16: LineSegment StartX=121 StartY=33 StartZ=0 EndX=121 EndY=19 EndZ=0
    g17: LineSegment StartX=117.5 StartY=9.01251 StartZ=0 EndX=121.163 EndY=9.0125 EndZ=0
    g18: ArcOfCircle CenterX=105 CenterY=19 CenterZ=0 NormalX=0 NormalY=0 NormalZ=1 AngleXU=0 Radius=20.6155 StartAngle=5.7297 EndAngle=6.28319
    g19: LineSegment StartX=121.163 StartY=9.0125 StartZ=0 EndX=122.538 EndY=8.16329 EndZ=0
    g20: LineSegment StartX=124 StartY=38 StartZ=0 EndX=125.616 EndY=38 EndZ=0
    g21: LineSegment StartX=125.616 StartY=19 StartZ=0 EndX=125.616 EndY=38 EndZ=0
  constraints (50):
    c: Vertical(g0)
    c: Block(g0)
    c: Coincident(g1,g0)
    c: Block(g1)
    c: Coincident(g2,g1)
    c: Block(g2)
    c: Coincident(g3,g2)
    c: Horizontal(g3)
    c: Tangent(g3,g2)
    c: Coincident(g4,g0)
    c: Distance(g4) = 3
    c: Vertical(g4)
    c: Coincident(g5,g4)
    c: Horizontal(g5)
    c: Coincident(g6,g2)
    c: Coincident(g6,g5)
    c: Vertical(g6)
    c: Horizontal(g7)
    c: Distance(g7) = 105
    c: Coincident(g7,g1)
    c: Block(g3)
    c: Weight(g8) = 1
    c: Equal(g8,g9)
    c: Equal(g8,g10)
    c: InternalAlignment(g8,g11)
    c: InternalAlignment(g9,g11)
    c: InternalAlignment(g10,g11)
    c: InternalAlignment(g12,g11)
    c: InternalAlignment(g13,g11)
    c: Block(g11)
    c: Coincident(g14,g11)
    c: Coincident(g14,g3)
    c: Horizontal(g14)
    c: Block(g15)
    c: Coincident(g16,g11)
    c: Coincident(g16,g15)
    c: Vertical(g16)
    c: Distance(g16) = 14
    c: Coincident(g17,g15)
    c: Block(g18)
    c: Coincident(g19,g18)
    c: Coincident(g20,g7)
    c: Horizontal(g20)
    c: Vertical(g21)
    c: Coincident(g20,g21)
    c: Block(g20)
    c: Block(g21)
    c: Block(g19)
    c: Block(g17)
    c: Distance(g20) = 1.61553
FEATURE [Part::Extrusion] Extrude044
  Base = -> Sketch053
  Dir = (0,0,1)
  DirMode = 2
  FaceMakerClass = Part::FaceMakerBullseye
  LengthFwd = 72
  LengthRev = 0
  Solid = true
  Symmetric = false
FEATURE [Part::Fillet] Fillet036  label="top018"
  Base = -> Extrude044
  Edges = 1 edges r=2: [Edge41]
FEATURE [Sketcher::SketchObject] Sketch054
  FullyConstrained = false
  Placement = pos=(0,0,0) rot=(1,0,0;1.5708rad)
  sketch-geometry (24):
    g0: ArcOfCircle CenterX=-4 CenterY=-10.5 CenterZ=0 NormalX=0 NormalY=0 NormalZ=1 AngleXU=0 Radius=1.5 StartAngle=6e-16 EndAngle=3.14159
    g1: ArcOfCircle CenterX=-34.2 CenterY=-10.5 CenterZ=0 NormalX=0 NormalY=0 NormalZ=1 AngleXU=0 Radius=1.5 StartAngle=0 EndAngle=3.14159
    g2: ArcOfCircle CenterX=-34.2 CenterY=-27.7 CenterZ=0 NormalX=0 NormalY=0 NormalZ=1 AngleXU=0 Radius=1.5 StartAngle=3.14159 EndAngle=6.28319
    g3: ArcOfCircle CenterX=-4 CenterY=-27.7 CenterZ=0 NormalX=0 NormalY=0 NormalZ=1 AngleXU=0 Radius=1.5 StartAngle=3.1416 EndAngle=6.28319
    g4: ArcOfCircle CenterX=-10 CenterY=-4.3 CenterZ=0 NormalX=0 NormalY=0 NormalZ=1 AngleXU=0 Radius=1.5 StartAngle=2e-16 EndAngle=3.14159
    g5: ArcOfCircle CenterX=-16.1 CenterY=-1.8 CenterZ=0 NormalX=0 NormalY=0 NormalZ=1 AngleXU=0 Radius=1.5 StartAngle=5e-16 EndAngle=3.14159
    g6: ArcOfCircle CenterX=-22.1 CenterY=-1.8 CenterZ=0 NormalX=0 NormalY=0 NormalZ=1 AngleXU=0 Radius=1.5 StartAngle=5e-16 EndAngle=3.14159
    g7: ArcOfCircle CenterX=-28.2 CenterY=-4.3 CenterZ=0 NormalX=0 NormalY=0 NormalZ=1 AngleXU=0 Radius=1.5 StartAngle=2e-16 EndAngle=3.14159
    g8: ArcOfCircle CenterX=-10 CenterY=-33.9 CenterZ=0 NormalX=0 NormalY=0 NormalZ=1 AngleXU=0 Radius=1.5 StartAngle=3.14159 EndAngle=6.28319
    g9: ArcOfCircle CenterX=-16.1 CenterY=-36.4 CenterZ=0 NormalX=0 NormalY=0 NormalZ=1 AngleXU=0 Radius=1.5 StartAngle=3.14159 EndAngle=6.28319
    g10: ArcOfCircle CenterX=-22.1 CenterY=-36.4 CenterZ=0 NormalX=0 NormalY=0 NormalZ=1 AngleXU=0 Radius=1.5 StartAngle=3.14159 EndAngle=6.28319
    g11: ArcOfCircle CenterX=-28.2 CenterY=-33.9 CenterZ=0 NormalX=0 NormalY=0 NormalZ=1 AngleXU=0 Radius=1.5 StartAngle=3.14159 EndAngle=6.28319
    g12: LineSegment StartX=-35.7 StartY=-10.5 StartZ=0 EndX=-35.7 EndY=-27.7 EndZ=0
    g13: LineSegment StartX=-32.7 StartY=-10.5 StartZ=0 EndX=-32.7 EndY=-27.7 EndZ=0
    g14: LineSegment StartX=-29.7 StartY=-33.9 StartZ=0 EndX=-29.7 EndY=-4.3 EndZ=0
    g15: LineSegment StartX=-26.7 StartY=-33.9 StartZ=0 EndX=-26.7 EndY=-4.3 EndZ=0
    g16: LineSegment StartX=-2.5 StartY=-10.5 StartZ=0 EndX=-2.5 EndY=-27.7 EndZ=0
    g17: LineSegment StartX=-8.5 StartY=-4.3 StartZ=0 EndX=-8.5 EndY=-33.9 EndZ=0
    g18: LineSegment StartX=-5.5 StartY=-10.5 StartZ=0 EndX=-5.5 EndY=-27.7 EndZ=0
    g19: LineSegment StartX=-11.5 StartY=-4.3 StartZ=0 EndX=-11.5 EndY=-33.9 EndZ=0
    g20: LineSegment StartX=-14.6 StartY=-1.8 StartZ=0 EndX=-14.6 EndY=-36.4 EndZ=0
    g21: LineSegment StartX=-17.6 StartY=-1.8 StartZ=0 EndX=-17.6 EndY=-36.4 EndZ=0
    g22: LineSegment StartX=-20.6 StartY=-36.4 StartZ=0 EndX=-20.6 EndY=-1.8 EndZ=0
    g23: LineSegment StartX=-23.6 StartY=-1.8 StartZ=0 EndX=-23.6 EndY=-36.4 EndZ=0
  constraints (48):
    c: Block(g0)
    c: Block(g1)
    c: Block(g2)
    c: Block(g3)
    c: Block(g4)
    c: Block(g5)
    c: Block(g6)
    c: Block(g7)
    c: Block(g8)
    c: Block(g9)
    c: Block(g10)
    c: Block(g11)
    c: Coincident(g12,g1)
    c: Coincident(g12,g2)
    c: Vertical(g12)
    c: Coincident(g13,g1)
    c: Coincident(g13,g2)
    c: Vertical(g13)
    c: Coincident(g14,g11)
    c: Coincident(g14,g7)
    c: Vertical(g14)
    c: Coincident(g15,g11)
    c: Coincident(g15,g7)
    c: Vertical(g15)
    c: Coincident(g16,g0)
    c: Coincident(g16,g3)
    c: Vertical(g16)
    c: Coincident(g17,g4)
    c: Coincident(g17,g8)
    c: Vertical(g17)
    c: Coincident(g18,g0)
    c: Coincident(g18,g3)
    c: Vertical(g18)
    c: Coincident(g19,g4)
    c: Coincident(g19,g8)
    c: Vertical(g19)
    c: Coincident(g20,g5)
    c: Coincident(g20,g9)
    c: Vertical(g20)
    c: Coincident(g21,g5)
    c: Coincident(g21,g9)
    c: Vertical(g21)
    c: Coincident(g22,g10)
    c: Coincident(g22,g6)
    c: Vertical(g22)
    c: Coincident(g23,g6)
    c: Coincident(g23,g10)
    c: Vertical(g23)
FEATURE [Part::Extrusion] Extrude045  label="removeToCreateFanGrillHoles003"
  Base = -> Sketch054
  Dir = (0,-1,6e-16)
  DirMode = 2
  FaceMakerClass = Part::FaceMakerBullseye
  LengthFwd = 10
  LengthRev = 0
  Placement = pos=(65.4,44,54.82) rot=(0,0,1;0rad)
  Solid = true
  Symmetric = false
FEATURE [Part::Feature] Face105 .. Face108  x4 (patterned run collapsed; names and placements below)
  shape: bbox 3.5 x 17.8 x 2e-07 mm, 1 faces, 0 solids (baked)
FEATURE [Part::Revolution] Revolve113  label="removeToCreateScrewAndThreadedInsertHole041"
  Angle = 360
  Axis = (0,1,0)
  Base = (0,0,0)
  FaceMakerClass = Part::FaceMakerBullseye
  Placement = pos=(62.3,30.3,19.7) rot=(0,0,1;0rad)
  Solid = false
  Source = -> Face105
  Symmetric = false
FEATURE [Part::Revolution] Revolve114  label="removeToCreateScrewAndThreadedInsertHole042"
  Angle = 360
  Axis = (0,1,0)
  Base = (0,0,0)
  FaceMakerClass = Part::FaceMakerBullseye
  Placement = pos=(62.3,30.3,51.7) rot=(0,0,1;0rad)
  Solid = false
  Source = -> Face106
  Symmetric = false
FEATURE [Part::Revolution] Revolve115  label="removeToCreateScrewAndThreadedInsertHole043"
  Angle = 360
  Axis = (0,1,0)
  Base = (0,0,0)
  FaceMakerClass = Part::FaceMakerBullseye
  Placement = pos=(30.3,30.3,19.7) rot=(0,0,1;0rad)
  Solid = false
  Source = -> Face107
  Symmetric = false
FEATURE [Part::Revolution] Revolve116  label="removeToCreateScrewAndThreadedInsertHole044"
  Angle = 360
  Axis = (0,1,0)
  Base = (0,0,0)
  FaceMakerClass = Part::FaceMakerBullseye
  Placement = pos=(30.3,30.3,51.7) rot=(0,0,1;0rad)
  Solid = false
  Source = -> Face108
  Symmetric = false
FEATURE [Part::MultiFuse] Fusion083  label="createThreadedInsertHolesForFan004"
  Shapes = -> [Revolve113,Revolve114,Revolve115,Revolve116]
FEATURE [Part::Box] Box024  label="removeToCreteHoleForPlugHousing026"
  AttacherType = Attacher::AttachEngine3D
  Height = 28.6
  Length = 10
  Placement = pos=(-2,0,21.7) rot=(0,0,1;0rad)
  Width = 19
FEATURE [Part::Cylinder] Cylinder038  label="removeToCreteHoleForPlugHousing027"
  Angle = 360
  AttacherType = Attacher::AttachEngine3D
  Height = 20
  Placement = pos=(-2,19,36) rot=(0,1,0;1.5708rad)
  Radius = 14.3
FEATURE [Part::MultiFuse] Fusion084  label="removeToCreteHoleForPlugHousing028"
  Shapes = -> [Box024,Cylinder038]
FEATURE [Part::Cylinder] Cylinder039
  Angle = 360
  AttacherType = Attacher::AttachEngine3D
  Height = 20
  Placement = pos=(0,0,36.15) rot=(0,0,1;0rad)
  Radius = 14.3
FEATURE [Part::Cylinder] Cylinder040
  Angle = 360
  AttacherType = Attacher::AttachEngine3D
  Height = 10
  Placement = pos=(0,0,36.15) rot=(0,0,1;0rad)
  Radius = 4
FEATURE [Part::Box] Box025  label="removeToCreteHoleForPlugHousing030"
  AttacherType = Attacher::AttachEngine3D
  Height = 28.6
  Length = 20
  Placement = pos=(106.15,0,21.7) rot=(0,0,1;0rad)
  Width = 19
FEATURE [Part::MultiFuse] Fusion086  label="removeToCreteHoleForPlugHousing031"
  Placement = pos=(70,19,36) rot=(0,1,0;1.5708rad)
  Shapes = -> [Cylinder039,Cylinder040]
FEATURE [Part::MultiFuse] Fusion085  label="removeToCreteHoleForPlugHousing029"
  Shapes = -> [Box025,Fusion086]
FEATURE [Sketcher::SketchObject] Sketch055
  FullyConstrained = true
  Placement = pos=(117,19,0) rot=(0.57735,0.57735,0.57735;2.0944rad)
  sketch-geometry (48):
    g0: LineSegment StartX=-49.19 StartY=69.25 StartZ=0 EndX=-49.19 EndY=66.25 EndZ=0
    g1: LineSegment StartX=-49.19 StartY=63.5 StartZ=0 EndX=-49.19 EndY=60.5 EndZ=0
    g2: LineSegment StartX=-49.19 StartY=57.75 StartZ=0 EndX=-49.19 EndY=54.75 EndZ=0
    g3: LineSegment StartX=-49.19 StartY=52 StartZ=0 EndX=-49.19 EndY=49 EndZ=0
    g4: LineSegment StartX=-49.19 StartY=46.25 StartZ=0 EndX=-49.19 EndY=43.25 EndZ=0
    g5: LineSegment StartX=-49.19 StartY=40.5 StartZ=0 EndX=-49.19 EndY=37.5 EndZ=0
    g6: LineSegment StartX=-49.19 StartY=34.5 StartZ=0 EndX=-49.19 EndY=31.5 EndZ=0
    g7: LineSegment StartX=-49.19 StartY=28.75 StartZ=0 EndX=-49.19 EndY=25.75 EndZ=0
    g8: LineSegment StartX=-49.19 StartY=23 StartZ=0 EndX=-49.19 EndY=20 EndZ=0
    g9: LineSegment StartX=-49.19 StartY=17.25 StartZ=0 EndX=-49.19 EndY=14.25 EndZ=0
    g10: LineSegment StartX=-49.19 StartY=11.5 StartZ=0 EndX=-49.19 EndY=8.5 EndZ=0
    g11: LineSegment StartX=-49.19 StartY=5.75 StartZ=0 EndX=-49.19 EndY=2.75 EndZ=0
    g12: ArcOfCircle CenterX=-1.5 CenterY=67.75 CenterZ=0 NormalX=0 NormalY=0 NormalZ=1 AngleXU=0 Radius=1.5 StartAngle=4.71239 EndAngle=7.85398
    g13: ArcOfCircle CenterX=-1.5 CenterY=62 CenterZ=0 NormalX=0 NormalY=0 NormalZ=1 AngleXU=0 Radius=1.5 StartAngle=4.71239 EndAngle=7.85398
    g14: ArcOfCircle CenterX=-1.5 CenterY=56.25 CenterZ=0 NormalX=0 NormalY=0 NormalZ=1 AngleXU=0 Radius=1.5 StartAngle=4.71239 EndAngle=7.85398
    g15: ArcOfCircle CenterX=-11.49 CenterY=50.5 CenterZ=0 NormalX=0 NormalY=0 NormalZ=1 AngleXU=0 Radius=1.5 StartAngle=4.71239 EndAngle=7.85398
    g16: ArcOfCircle CenterX=-16.28 CenterY=44.75 CenterZ=0 NormalX=0 NormalY=0 NormalZ=1 AngleXU=0 Radius=1.5 StartAngle=4.71239 EndAngle=7.85398
    g17: ArcOfCircle CenterX=-18.2337 CenterY=39 CenterZ=0 NormalX=0 NormalY=0 NormalZ=1 AngleXU=0 Radius=1.5 StartAngle=4.71485 EndAngle=7.85398
    g18: ArcOfCircle CenterX=-16.2837 CenterY=27.25 CenterZ=0 NormalX=0 NormalY=0 NormalZ=1 AngleXU=0 Radius=1.5 StartAngle=4.71485 EndAngle=7.85398
    g19: ArcOfCircle CenterX=-18.2337 CenterY=33 CenterZ=0 NormalX=0 NormalY=0 NormalZ=1 AngleXU=0 Radius=1.5 StartAngle=4.71485 EndAngle=7.85398
    g20: ArcOfCircle CenterX=-11.49 CenterY=21.5 CenterZ=0 NormalX=0 NormalY=0 NormalZ=1 AngleXU=0 Radius=1.5 StartAngle=4.71239 EndAngle=7.85398
    g21: ArcOfCircle CenterX=-1.5 CenterY=4.25 CenterZ=0 NormalX=0 NormalY=0 NormalZ=1 AngleXU=0 Radius=1.5 StartAngle=4.71239 EndAngle=7.85398
    g22: ArcOfCircle CenterX=-1.5 CenterY=10 CenterZ=0 NormalX=0 NormalY=0 NormalZ=1 AngleXU=0 Radius=1.5 StartAngle=4.71239 EndAngle=7.85398
    g23: ArcOfCircle CenterX=-1.5 CenterY=15.75 CenterZ=0 NormalX=0 NormalY=0 NormalZ=1 AngleXU=0 Radius=1.5 StartAngle=4.71239 EndAngle=7.85398
    g24: LineSegment StartX=-49.19 StartY=69.25 StartZ=0 EndX=-1.5 EndY=69.25 EndZ=0
    g25: LineSegment StartX=-49.19 StartY=66.25 StartZ=0 EndX=-1.5 EndY=66.25 EndZ=0
    g26: LineSegment StartX=-49.19 StartY=63.5 StartZ=0 EndX=-1.5 EndY=63.5 EndZ=0
    g27: LineSegment StartX=-49.19 StartY=60.5 StartZ=0 EndX=-1.5 EndY=60.5 EndZ=0
    g28: LineSegment StartX=-49.19 StartY=57.75 StartZ=0 EndX=-1.5 EndY=57.75 EndZ=0
    g29: LineSegment StartX=-49.19 StartY=54.75 StartZ=0 EndX=-1.5 EndY=54.75 EndZ=0
    g30: LineSegment StartX=-49.19 StartY=52 StartZ=0 EndX=-11.49 EndY=52 EndZ=0
    g31: LineSegment StartX=-49.19 StartY=49 StartZ=0 EndX=-11.49 EndY=49 EndZ=0
    g32: LineSegment StartX=-49.19 StartY=46.25 StartZ=0 EndX=-16.28 EndY=46.25 EndZ=0
    g33: LineSegment StartX=-49.19 StartY=43.25 StartZ=0 EndX=-16.28 EndY=43.25 EndZ=0
    g34: LineSegment StartX=-49.19 StartY=40.5 StartZ=0 EndX=-18.2337 EndY=40.5 EndZ=0
    g35: LineSegment StartX=-49.19 StartY=37.5 StartZ=0 EndX=-18.23 EndY=37.5 EndZ=0
    g36: LineSegment StartX=-49.19 StartY=34.5 StartZ=0 EndX=-18.2337 EndY=34.5 EndZ=0
    g37: LineSegment StartX=-49.19 StartY=31.5 StartZ=0 EndX=-18.23 EndY=31.5 EndZ=0
    g38: LineSegment StartX=-49.19 StartY=28.75 StartZ=0 EndX=-16.2837 EndY=28.75 EndZ=0
    g39: LineSegment StartX=-49.19 StartY=25.75 StartZ=0 EndX=-16.28 EndY=25.75 EndZ=0
    g40: LineSegment StartX=-49.19 StartY=23 StartZ=0 EndX=-11.49 EndY=23 EndZ=0
    g41: LineSegment StartX=-49.19 StartY=20 StartZ=0 EndX=-11.49 EndY=20 EndZ=0
    g42: LineSegment StartX=-49.19 StartY=17.25 StartZ=0 EndX=-1.5 EndY=17.25 EndZ=0
    g43: LineSegment StartX=-49.19 StartY=14.25 StartZ=0 EndX=-1.5 EndY=14.25 EndZ=0
    g44: LineSegment StartX=-49.19 StartY=11.5 StartZ=0 EndX=-1.5 EndY=11.5 EndZ=0
    g45: LineSegment StartX=-49.19 StartY=8.5 StartZ=0 EndX=-1.5 EndY=8.5 EndZ=0
    g46: LineSegment StartX=-49.19 StartY=5.75 StartZ=0 EndX=-1.5 EndY=5.75 EndZ=0
    g47: LineSegment StartX=-49.19 StartY=2.75 StartZ=0 EndX=-1.5 EndY=2.75 EndZ=0
  constraints (120):
    c: Vertical(g0)
    c: Distance(g0) = 3
    c: Block(g0)
    c: Vertical(g1)
    c: Distance(g1) = 3
    c: Vertical(g2)
    c: Equal(g0,g2) = 3
    c: Block(g2)
    c: Vertical(g3)
    c: Equal(g1,g3) = 3
    c: Vertical(g4)
    c: Equal(g0,g4) = 3
    c: Block(g4)
    c: Vertical(g5)
    c: Equal(g1,g5) = 3
    c: Vertical(g6)
    c: Equal(g0,g6) = 3
    c: Block(g6)
    c: Vertical(g7)
    c: Equal(g1,g7) = 3
    c: Vertical(g8)
    c: Equal(g0,g8) = 3
    c: Block(g8)
    c: Vertical(g9)
    c: Equal(g1,g9) = 3
    c: Vertical(g10)
    c: Equal(g0,g10) = 3
    c: Block(g10)
    c: Vertical(g11)
    c: Equal(g1,g11) = 3
    c: Block(g12)
    c: Block(g13)
    c: Block(g14)
    c: Block(g15)
    c: Block(g16)
    c: Block(g17)
    c: Block(g18)
    c: Block(g19)
    c: Block(g20)
    c: Block(g21)
    c: Block(g22)
    c: Block(g23)
    c: Block(g11)
    c: Block(g9)
    c: Block(g7)
    c: Block(g5)
    c: Block(g3)
    c: Block(g1)
    c: Coincident(g24,g0)
    c: Coincident(g24,g12)
    c: Horizontal(g24)
    c: Coincident(g25,g0)
    c: Coincident(g25,g12)
    c: Horizontal(g25)
    c: Coincident(g26,g1)
    c: Coincident(g26,g13)
    c: Horizontal(g26)
    c: Coincident(g27,g1)
    c: Coincident(g27,g13)
    c: Horizontal(g27)
    c: Coincident(g28,g2)
    c: Coincident(g28,g14)
    c: Horizontal(g28)
    c: Coincident(g29,g2)
    c: Coincident(g29,g14)
    c: Horizontal(g29)
    c: Coincident(g30,g3)
    c: Coincident(g30,g15)
    c: Horizontal(g30)
    c: Coincident(g31,g3)
    c: Coincident(g31,g15)
    c: Horizontal(g31)
    c: Coincident(g32,g4)
    c: Coincident(g32,g16)
    c: Horizontal(g32)
    c: Coincident(g33,g4)
    c: Coincident(g33,g16)
    c: Horizontal(g33)
    c: Coincident(g34,g5)
    c: Coincident(g34,g17)
    c: Horizontal(g34)
    c: Coincident(g35,g5)
    c: Coincident(g35,g17)
    c: Horizontal(g35)
    c: Coincident(g36,g6)
    c: Coincident(g36,g19)
    c: Horizontal(g36)
    c: Coincident(g37,g6)
    c: Coincident(g37,g19)
    c: Horizontal(g37)
    c: Coincident(g38,g7)
    c: Coincident(g38,g18)
    c: Horizontal(g38)
    c: Coincident(g39,g7)
    c: Coincident(g39,g18)
    c: Horizontal(g39)
    c: Coincident(g40,g8)
    c: Coincident(g40,g20)
    c: Horizontal(g40)
    c: Coincident(g41,g8)
    c: Coincident(g41,g20)
    c: Horizontal(g41)
    c: Coincident(g42,g9)
    c: Coincident(g42,g23)
    c: Horizontal(g42)
    c: Coincident(g43,g9)
    c: Coincident(g43,g23)
    c: Horizontal(g43)
    c: Coincident(g44,g10)
    c: Coincident(g44,g22)
    c: Horizontal(g44)
    c: Coincident(g45,g10)
    c: Coincident(g45,g22)
    c: Horizontal(g45)
    c: Coincident(g46,g11)
    c: Coincident(g46,g21)
    c: Horizontal(g46)
    c: Coincident(g47,g11)
    c: Coincident(g47,g21)
    c: Horizontal(g47)
FEATURE [Part::Extrusion] Extrude046
  Base = -> Sketch055
  Dir = (1,0,0)
  DirMode = 2
  FaceMakerClass = Part::FaceMakerBullseye
  LengthFwd = 23
  LengthRev = 0
  Placement = pos=(-19,0,0) rot=(0,0,1;0rad)
  Solid = true
  Symmetric = false
FEATURE [Part::Fillet] Fillet038  label="removeToCreateVentalationHoles001"
  Base = -> Extrude046
  Edges = <same value as first occurrence — deduplicated (x5 in doc)>
  Placement = pos=(7,0,0) rot=(0,0,1;0rad)
FEATURE [Sketcher::SketchObject] Sketch056  label="topSketch014"
  FullyConstrained = true
  sketch-geometry (22):
    g0: LineSegment StartX=5.21097e-06 StartY=3 StartZ=0 EndX=5.21097e-06 EndY=19 EndZ=0
    g1: ArcOfCircle CenterX=19 CenterY=19 CenterZ=0 NormalX=0 NormalY=0 NormalZ=1 AngleXU=0 Radius=19 StartAngle=1.5708 EndAngle=3.14159
    g2: ArcOfCircle CenterX=19 CenterY=19 CenterZ=0 NormalX=0 NormalY=0 NormalZ=1 AngleXU=0 Radius=16 StartAngle=1.5708 EndAngle=3.14159
    g3: LineSegment StartX=114 StartY=35 StartZ=0 EndX=19 EndY=35 EndZ=0
    g4: LineSegment StartX=5.21097e-06 StartY=3 StartZ=0 EndX=5.21097e-06 EndY=0 EndZ=0
    g5: LineSegment StartX=3 StartY=0 StartZ=0 EndX=5.21097e-06 EndY=0 EndZ=0
    g6: LineSegment StartX=3 StartY=19 StartZ=0 EndX=3 EndY=0 EndZ=0
    g7: LineSegment StartX=19 StartY=38 StartZ=0 EndX=124 EndY=38 EndZ=0
    g8: Circle CenterX=119 CenterY=35 CenterZ=0 NormalX=0 NormalY=0 NormalZ=1 AngleXU=0 Radius=1
    g9: Circle CenterX=121 CenterY=35 CenterZ=0 NormalX=0 NormalY=0 NormalZ=1 AngleXU=0 Radius=1
    g10: Circle CenterX=121 CenterY=33 CenterZ=0 NormalX=0 NormalY=0 NormalZ=1 AngleXU=0 Radius=1
    g11: BSplineCurve PolesCount=3 KnotsCount=2 Degree=2 IsPeriodic=0
    g12: GeomPoint X=119 Y=35 Z=0
    g13: GeomPoint X=121 Y=33 Z=0
    g14: LineSegment StartX=119 StartY=35 StartZ=0 EndX=114 EndY=35 EndZ=0
    g15: ArcOfCircle CenterX=105 CenterY=19 CenterZ=0 NormalX=0 NormalY=0 NormalZ=1 AngleXU=0 Radius=16 StartAngle=5.60905 EndAngle=6.28319
    g16: LineSegment StartX=121 StartY=33 StartZ=0 EndX=121 EndY=19 EndZ=0
    g17: LineSegment StartX=117.5 StartY=9.01251 StartZ=0 EndX=121.163 EndY=9.0125 EndZ=0
    g18: ArcOfCircle CenterX=105 CenterY=19 CenterZ=0 NormalX=0 NormalY=0 NormalZ=1 AngleXU=0 Radius=20.6155 StartAngle=5.7297 EndAngle=6.28319
    g19: LineSegment StartX=121.163 StartY=9.0125 StartZ=0 EndX=122.538 EndY=8.16329 EndZ=0
    g20: LineSegment StartX=124 StartY=38 StartZ=0 EndX=125.616 EndY=38 EndZ=0
    g21: LineSegment StartX=125.616 StartY=19 StartZ=0 EndX=125.616 EndY=38 EndZ=0
  constraints (49):
    c: Vertical(g0)
    c: Block(g0)
    c: Coincident(g1,g0)
    c: Block(g1)
    c: Coincident(g2,g1)
    c: Block(g2)
    c: Coincident(g3,g2)
    c: Horizontal(g3)
    c: Tangent(g3,g2)
    c: Coincident(g4,g0)
    c: Distance(g4) = 3
    c: Vertical(g4)
    c: Coincident(g5,g4)
    c: Horizontal(g5)
    c: Coincident(g6,g2)
    c: Coincident(g6,g5)
    c: Vertical(g6)
    c: Horizontal(g7)
    c: Distance(g7) = 105
    c: Coincident(g7,g1)
    c: Block(g3)
    c: Weight(g8) = 1
    c: Equal(g8,g9)
    c: Equal(g8,g10)
    c: InternalAlignment(g8,g11)
    c: InternalAlignment(g9,g11)
    c: InternalAlignment(g10,g11)
    c: InternalAlignment(g12,g11)
    c: InternalAlignment(g13,g11)
    c: Block(g11)
    c: Coincident(g14,g11)
    c: Coincident(g14,g3)
    c: Horizontal(g14)
    c: Block(g15)
    c: Coincident(g16,g11)
    c: Coincident(g16,g15)
    c: Vertical(g16)
    c: Distance(g16) = 14
    c: Coincident(g17,g15)
    c: Block(g18)
    c: Coincident(g19,g18)
    c: Coincident(g20,g7)
    c: Horizontal(g20)
    c: Vertical(g21)
    c: Coincident(g20,g21)
    c: Block(g20)
    c: Block(g21)
    c: Block(g19)
    c: Block(g17)
FEATURE [Part::Box] Box026  label="removeToCreteHoleForPlugHousing032"
  AttacherType = Attacher::AttachEngine3D
  Height = 28.6
  Length = 10
  Placement = pos=(-2,0,21.7) rot=(0,0,1;0rad)
  Width = 19
FEATURE [Part::Feature] Face109 .. Face112  x4 (patterned run collapsed; names and placements below)
  shape: bbox 3.5 x 17.8 x 2e-07 mm, 1 faces, 0 solids (baked)
FEATURE [Part::Revolution] Revolve117  label="removeToCreateScrewAndThreadedInsertHole045"
  Angle = 360
  Axis = (0,1,0)
  Base = (0,0,0)
  FaceMakerClass = Part::FaceMakerBullseye
  Placement = pos=(62.3,30.3,19.7) rot=(0,0,1;0rad)
  Solid = false
  Source = -> Face109
  Symmetric = false
FEATURE [Part::Revolution] Revolve118  label="removeToCreateScrewAndThreadedInsertHole046"
  Angle = 360
  Axis = (0,1,0)
  Base = (0,0,0)
  FaceMakerClass = Part::FaceMakerBullseye
  Placement = pos=(62.3,30.3,51.7) rot=(0,0,1;0rad)
  Solid = false
  Source = -> Face110
  Symmetric = false
FEATURE [Part::Revolution] Revolve119  label="removeToCreateScrewAndThreadedInsertHole047"
  Angle = 360
  Axis = (0,1,0)
  Base = (0,0,0)
  FaceMakerClass = Part::FaceMakerBullseye
  Placement = pos=(30.3,30.3,19.7) rot=(0,0,1;0rad)
  Solid = false
  Source = -> Face111
  Symmetric = false
FEATURE [Part::Revolution] Revolve120  label="removeToCreateScrewAndThreadedInsertHole048"
  Angle = 360
  Axis = (0,1,0)
  Base = (0,0,0)
  FaceMakerClass = Part::FaceMakerBullseye
  Placement = pos=(30.3,30.3,51.7) rot=(0,0,1;0rad)
  Solid = false
  Source = -> Face112
  Symmetric = false
FEATURE [Part::MultiFuse] Fusion087  label="createThreadedInsertHolesForFan005"
  Shapes = -> [Revolve117,Revolve118,Revolve119,Revolve120]
FEATURE [Part::Extrusion] Extrude047
  Base = -> Sketch056
  Dir = (0,0,1)
  DirMode = 2
  FaceMakerClass = Part::FaceMakerBullseye
  LengthFwd = 72
  LengthRev = 0
  Solid = true
  Symmetric = false
FEATURE [Part::Fillet] Fillet039  label="top019"
  Base = -> Extrude047
  Edges = 1 edges r=2: [Edge35]
FEATURE [Sketcher::SketchObject] Sketch057
  FullyConstrained = false
  Placement = pos=(0,0,0) rot=(1,0,0;1.5708rad)
  sketch-geometry (24):
    g0: ArcOfCircle CenterX=-4 CenterY=-10.5 CenterZ=0 NormalX=0 NormalY=0 NormalZ=1 AngleXU=0 Radius=1.5 StartAngle=6e-16 EndAngle=3.14159
    g1: ArcOfCircle CenterX=-34.2 CenterY=-10.5 CenterZ=0 NormalX=0 NormalY=0 NormalZ=1 AngleXU=0 Radius=1.5 StartAngle=0 EndAngle=3.14159
    g2: ArcOfCircle CenterX=-34.2 CenterY=-27.7 CenterZ=0 NormalX=0 NormalY=0 NormalZ=1 AngleXU=0 Radius=1.5 StartAngle=3.14159 EndAngle=6.28319
    g3: ArcOfCircle CenterX=-4 CenterY=-27.7 CenterZ=0 NormalX=0 NormalY=0 NormalZ=1 AngleXU=0 Radius=1.5 StartAngle=3.1416 EndAngle=6.28319
    g4: ArcOfCircle CenterX=-10 CenterY=-4.3 CenterZ=0 NormalX=0 NormalY=0 NormalZ=1 AngleXU=0 Radius=1.5 StartAngle=2e-16 EndAngle=3.14159
    g5: ArcOfCircle CenterX=-16.1 CenterY=-1.8 CenterZ=0 NormalX=0 NormalY=0 NormalZ=1 AngleXU=0 Radius=1.5 StartAngle=5e-16 EndAngle=3.14159
    g6: ArcOfCircle CenterX=-22.1 CenterY=-1.8 CenterZ=0 NormalX=0 NormalY=0 NormalZ=1 AngleXU=0 Radius=1.5 StartAngle=5e-16 EndAngle=3.14159
    g7: ArcOfCircle CenterX=-28.2 CenterY=-4.3 CenterZ=0 NormalX=0 NormalY=0 NormalZ=1 AngleXU=0 Radius=1.5 StartAngle=2e-16 EndAngle=3.14159
    g8: ArcOfCircle CenterX=-10 CenterY=-33.9 CenterZ=0 NormalX=0 NormalY=0 NormalZ=1 AngleXU=0 Radius=1.5 StartAngle=3.14159 EndAngle=6.28319
    g9: ArcOfCircle CenterX=-16.1 CenterY=-36.4 CenterZ=0 NormalX=0 NormalY=0 NormalZ=1 AngleXU=0 Radius=1.5 StartAngle=3.14159 EndAngle=6.28319
    g10: ArcOfCircle CenterX=-22.1 CenterY=-36.4 CenterZ=0 NormalX=0 NormalY=0 NormalZ=1 AngleXU=0 Radius=1.5 StartAngle=3.14159 EndAngle=6.28319
    g11: ArcOfCircle CenterX=-28.2 CenterY=-33.9 CenterZ=0 NormalX=0 NormalY=0 NormalZ=1 AngleXU=0 Radius=1.5 StartAngle=3.14159 EndAngle=6.28319
    g12: LineSegment StartX=-35.7 StartY=-10.5 StartZ=0 EndX=-35.7 EndY=-27.7 EndZ=0
    g13: LineSegment StartX=-32.7 StartY=-10.5 StartZ=0 EndX=-32.7 EndY=-27.7 EndZ=0
    g14: LineSegment StartX=-29.7 StartY=-33.9 StartZ=0 EndX=-29.7 EndY=-4.3 EndZ=0
    g15: LineSegment StartX=-26.7 StartY=-33.9 StartZ=0 EndX=-26.7 EndY=-4.3 EndZ=0
    g16: LineSegment StartX=-2.5 StartY=-10.5 StartZ=0 EndX=-2.5 EndY=-27.7 EndZ=0
    g17: LineSegment StartX=-8.5 StartY=-4.3 StartZ=0 EndX=-8.5 EndY=-33.9 EndZ=0
    g18: LineSegment StartX=-5.5 StartY=-10.5 StartZ=0 EndX=-5.5 EndY=-27.7 EndZ=0
    g19: LineSegment StartX=-11.5 StartY=-4.3 StartZ=0 EndX=-11.5 EndY=-33.9 EndZ=0
    g20: LineSegment StartX=-14.6 StartY=-1.8 StartZ=0 EndX=-14.6 EndY=-36.4 EndZ=0
    g21: LineSegment StartX=-17.6 StartY=-1.8 StartZ=0 EndX=-17.6 EndY=-36.4 EndZ=0
    g22: LineSegment StartX=-20.6 StartY=-36.4 StartZ=0 EndX=-20.6 EndY=-1.8 EndZ=0
    g23: LineSegment StartX=-23.6 StartY=-1.8 StartZ=0 EndX=-23.6 EndY=-36.4 EndZ=0
  constraints (48):
    c: Block(g0)
    c: Block(g1)
    c: Block(g2)
    c: Block(g3)
    c: Block(g4)
    c: Block(g5)
    c: Block(g6)
    c: Block(g7)
    c: Block(g8)
    c: Block(g9)
    c: Block(g10)
    c: Block(g11)
    c: Coincident(g12,g1)
    c: Coincident(g12,g2)
    c: Vertical(g12)
    c: Coincident(g13,g1)
    c: Coincident(g13,g2)
    c: Vertical(g13)
    c: Coincident(g14,g11)
    c: Coincident(g14,g7)
    c: Vertical(g14)
    c: Coincident(g15,g11)
    c: Coincident(g15,g7)
    c: Vertical(g15)
    c: Coincident(g16,g0)
    c: Coincident(g16,g3)
    c: Vertical(g16)
    c: Coincident(g17,g4)
    c: Coincident(g17,g8)
    c: Vertical(g17)
    c: Coincident(g18,g0)
    c: Coincident(g18,g3)
    c: Vertical(g18)
    c: Coincident(g19,g4)
    c: Coincident(g19,g8)
    c: Vertical(g19)
    c: Coincident(g20,g5)
    c: Coincident(g20,g9)
    c: Vertical(g20)
    c: Coincident(g21,g5)
    c: Coincident(g21,g9)
    c: Vertical(g21)
    c: Coincident(g22,g10)
    c: Coincident(g22,g6)
    c: Vertical(g22)
    c: Coincident(g23,g6)
    c: Coincident(g23,g10)
    c: Vertical(g23)
FEATURE [Part::Extrusion] Extrude048  label="removeToCreateFanGrillHoles004"
  Base = -> Sketch057
  Dir = (0,-1,6e-16)
  DirMode = 2
  FaceMakerClass = Part::FaceMakerBullseye
  LengthFwd = 10
  LengthRev = 0
  Placement = pos=(65.4,44,54.82) rot=(0,0,1;0rad)
  Solid = true
  Symmetric = false
FEATURE [Part::Cut] Cut040  label="top021"
  Base = -> Fillet039
  Tool = -> Extrude048
FEATURE [Part::Cylinder] Cylinder041  label="removeToCreteHoleForPlugHousing034"
  Angle = 360
  AttacherType = Attacher::AttachEngine3D
  Height = 20
  Placement = pos=(-2,19,36) rot=(0,1,0;1.5708rad)
  Radius = 14.3
FEATURE [Part::MultiFuse] Fusion089  label="removeToCreteHoleForPlugHousing035"
  Shapes = -> [Box026,Cylinder041]
FEATURE [Part::Cylinder] Cylinder042
  Angle = 360
  AttacherType = Attacher::AttachEngine3D
  Height = 20
  Placement = pos=(0,0,36.15) rot=(0,0,1;0rad)
  Radius = 14.3
FEATURE [Part::Cylinder] Cylinder043
  Angle = 360
  AttacherType = Attacher::AttachEngine3D
  Height = 10
  Placement = pos=(0,0,36.15) rot=(0,0,1;0rad)
  Radius = 4
FEATURE [Part::Box] Box027  label="removeToCreteHoleForPlugHousing036"
  AttacherType = Attacher::AttachEngine3D
  Height = 28.6
  Length = 20
  Placement = pos=(106.15,0,21.7) rot=(0,0,1;0rad)
  Width = 19
FEATURE [Part::Cut] Cut041  label="top022"
  Base = -> Cut040
  Tool = -> Fusion087
FEATURE [Part::Cut] Cut039  label="top020"
  Base = -> Cut041
  Tool = -> Fusion089
FEATURE [Part::MultiFuse] Fusion090  label="removeToCreteHoleForPlugHousing037"
  Placement = pos=(70,19,36) rot=(0,1,0;1.5708rad)
  Shapes = -> [Cylinder042,Cylinder043]
FEATURE [Part::MultiFuse] Fusion088  label="removeToCreteHoleForPlugHousing033"
  Shapes = -> [Box027,Fusion090]
FEATURE [Part::Cut] Cut042  label="removeToCreteHoleForPlugHousing038"
  Base = -> Cut039
  Tool = -> Fusion088
FEATURE [Part::MultiFuse] Fusion091  label="removeFromTop"
  Shapes = -> [Fillet038,Fusion085,Fusion084,Fusion083,Extrude045]
FEATURE [Part::Cut] Cut043  label="REAL TOP ====="
  Base = -> Fillet036
  Tool = -> Fusion091
FEATURE [Part::MultiFuse] Fusion092  label="caseScrewPillarBracket016"
  Shapes = -> [Extrude030,Extrude031,Extrude032,Extrude033,Extrude034,Extrude035,Extrude036,Extrude037,Box013,Box014]
FEATURE [Sketcher::SketchObject] Sketch058  label="topSketch015"
  FullyConstrained = true
  sketch-geometry (20):
    g0: LineSegment StartX=5.21097e-06 StartY=3 StartZ=0 EndX=5.21097e-06 EndY=19 EndZ=0
    g1: ArcOfCircle CenterX=19 CenterY=19 CenterZ=0 NormalX=0 NormalY=0 NormalZ=1 AngleXU=0 Radius=19 StartAngle=1.5708 EndAngle=3.14159
    g2: ArcOfCircle CenterX=19 CenterY=19 CenterZ=0 NormalX=0 NormalY=0 NormalZ=1 AngleXU=0 Radius=16 StartAngle=1.5708 EndAngle=3.14159
    g3: LineSegment StartX=114 StartY=35 StartZ=0 EndX=19 EndY=35 EndZ=0
    g4: LineSegment StartX=5.21097e-06 StartY=3 StartZ=0 EndX=5.21097e-06 EndY=0 EndZ=0
    g5: LineSegment StartX=3 StartY=0 StartZ=0 EndX=5.21097e-06 EndY=0 EndZ=0
    g6: LineSegment StartX=3 StartY=19 StartZ=0 EndX=3 EndY=0 EndZ=0
    g7: LineSegment StartX=19 StartY=38 StartZ=0 EndX=124 EndY=38 EndZ=0
    g8: Circle CenterX=119 CenterY=35 CenterZ=0 NormalX=0 NormalY=0 NormalZ=1 AngleXU=0 Radius=1
    g9: Circle CenterX=121 CenterY=35 CenterZ=0 NormalX=0 NormalY=0 NormalZ=1 AngleXU=0 Radius=1
    g10: Circle CenterX=121 CenterY=33 CenterZ=0 NormalX=0 NormalY=0 NormalZ=1 AngleXU=0 Radius=1
    g11: BSplineCurve PolesCount=3 KnotsCount=2 Degree=2 IsPeriodic=0
    g12: GeomPoint X=119 Y=35 Z=0
    g13: GeomPoint X=121 Y=33 Z=0
    g14: LineSegment StartX=119 StartY=35 StartZ=0 EndX=114 EndY=35 EndZ=0
    g15: ArcOfCircle CenterX=105 CenterY=19 CenterZ=0 NormalX=0 NormalY=0 NormalZ=1 AngleXU=0 Radius=19 StartAngle=5.7297 EndAngle=6.28319
    g16: ArcOfCircle CenterX=105 CenterY=19 CenterZ=0 NormalX=0 NormalY=0 NormalZ=1 AngleXU=0 Radius=16 StartAngle=5.60905 EndAngle=6.28319
    g17: LineSegment StartX=121 StartY=33 StartZ=0 EndX=121 EndY=19 EndZ=0
    g18: LineSegment StartX=124 StartY=38 StartZ=0 EndX=124 EndY=19 EndZ=0
    g19: LineSegment StartX=117.5 StartY=9.01251 StartZ=0 EndX=121.163 EndY=9.0125 EndZ=0
  constraints (46):
    c: Vertical(g0)
    c: Block(g0)
    c: Coincident(g1,g0)
    c: Block(g1)
    c: Coincident(g2,g1)
    c: Block(g2)
    c: Coincident(g3,g2)
    c: Horizontal(g3)
    c: Tangent(g3,g2)
    c: Coincident(g4,g0)
    c: Distance(g4) = 3
    c: Vertical(g4)
    c: Coincident(g5,g4)
    c: Horizontal(g5)
    c: Coincident(g6,g2)
    c: Coincident(g6,g5)
    c: Vertical(g6)
    c: Horizontal(g7)
    c: Distance(g7) = 105
    c: Coincident(g7,g1)
    c: Block(g3)
    c: Weight(g8) = 1
    c: Equal(g8,g9)
    c: Equal(g8,g10)
    c: InternalAlignment(g8,g11)
    c: InternalAlignment(g9,g11)
    c: InternalAlignment(g10,g11)
    c: InternalAlignment(g12,g11)
    c: InternalAlignment(g13,g11)
    c: Block(g11)
    c: Coincident(g14,g11)
    c: Coincident(g14,g3)
    c: Horizontal(g14)
    c: Block(g15)
    c: Coincident(g16,g15)
    c: Block(g16)
    c: Coincident(g17,g11)
    c: Coincident(g17,g16)
    c: Vertical(g17)
    c: Distance(g17) = 14
    c: Coincident(g18,g7)
    c: Coincident(g18,g15)
    c: Vertical(g18)
    c: Distance(g18) = 19
    c: Coincident(g19,g16)
    c: Coincident(g19,g15)
FEATURE [Part::Extrusion] Extrude049  label="top023"
  Base = -> Sketch058
  Dir = (0,0,1)
  DirMode = 2
  FaceMakerClass = Part::FaceMakerBullseye
  LengthFwd = 72
  LengthRev = 0
  Solid = true
  Symmetric = false
FEATURE [Sketcher::SketchObject] Sketch059
  FullyConstrained = true
  MapMode = 3
  Placement = pos=(0,0,0) rot=(1,0,0;1.5708rad)
  Support = -> [Extrude049]
  sketch-geometry (8):
    g0: Circle CenterX=80.351 CenterY=-67.6202 CenterZ=0 NormalX=0 NormalY=0 NormalZ=1 AngleXU=0 Radius=2
    g1: Circle CenterX=80.351 CenterY=-67.6202 CenterZ=0 NormalX=0 NormalY=0 NormalZ=1 AngleXU=0 Radius=3
    g2: Circle CenterX=80.351 CenterY=-4.92017 CenterZ=0 NormalX=0 NormalY=0 NormalZ=1 AngleXU=0 Radius=2
    g3: Circle CenterX=80.351 CenterY=-4.92017 CenterZ=0 NormalX=0 NormalY=0 NormalZ=1 AngleXU=0 Radius=3
    g4: Circle CenterX=23.851 CenterY=-4.92017 CenterZ=0 NormalX=0 NormalY=0 NormalZ=1 AngleXU=0 Radius=2
    g5: Circle CenterX=23.851 CenterY=-4.92017 CenterZ=0 NormalX=0 NormalY=0 NormalZ=1 AngleXU=0 Radius=3
    g6: Circle CenterX=23.851 CenterY=-67.6202 CenterZ=0 NormalX=0 NormalY=0 NormalZ=1 AngleXU=0 Radius=2
    g7: Circle CenterX=23.851 CenterY=-67.6202 CenterZ=0 NormalX=0 NormalY=0 NormalZ=1 AngleXU=0 Radius=3
  constraints (8):
    c: Block(g3)
    c: Block(g2)
    c: Block(g1)
    c: Block(g0)
    c: Block(g6)
    c: Block(g7)
    c: Block(g4)
    c: Block(g5)
FEATURE [Sketcher::SketchObject] Sketch060
  FullyConstrained = true
  MapMode = 3
  Placement = pos=(0,0,0) rot=(1,0,0;1.5708rad)
  Support = -> [Extrude049]
  sketch-geometry (8):
    g0: Circle CenterX=80.351 CenterY=-67.6202 CenterZ=0 NormalX=0 NormalY=0 NormalZ=1 AngleXU=0 Radius=3
    g1: Circle CenterX=80.351 CenterY=-4.92017 CenterZ=0 NormalX=0 NormalY=0 NormalZ=1 AngleXU=0 Radius=3
    g2: Circle CenterX=23.851 CenterY=-4.92017 CenterZ=0 NormalX=0 NormalY=0 NormalZ=1 AngleXU=0 Radius=3
    g3: Circle CenterX=23.851 CenterY=-67.6202 CenterZ=0 NormalX=0 NormalY=0 NormalZ=1 AngleXU=0 Radius=3
    g4: Circle CenterX=23.851 CenterY=-67.6202 CenterZ=0 NormalX=0 NormalY=0 NormalZ=1 AngleXU=0 Radius=5
    g5: Circle CenterX=80.351 CenterY=-67.6202 CenterZ=0 NormalX=0 NormalY=0 NormalZ=1 AngleXU=0 Radius=5
    g6: Circle CenterX=23.851 CenterY=-4.92017 CenterZ=0 NormalX=0 NormalY=0 NormalZ=1 AngleXU=0 Radius=5
    g7: Circle CenterX=80.351 CenterY=-4.92017 CenterZ=0 NormalX=0 NormalY=0 NormalZ=1 AngleXU=0 Radius=5
  constraints (8):
    c: Block(g1)
    c: Block(g0)
    c: Block(g3)
    c: Block(g2)
    c: Block(g5)
    c: Block(g4)
    c: Block(g6)
    c: Block(g7)
FEATURE [Sketcher::SketchObject] Sketch061
  FullyConstrained = true
  MapMode = 3
  Placement = pos=(0,0,0) rot=(1,0,0;1.5708rad)
  sketch-geometry (8):
    g0: Circle CenterX=80.351 CenterY=-67.6202 CenterZ=0 NormalX=0 NormalY=0 NormalZ=1 AngleXU=0 Radius=3
    g1: Circle CenterX=80.351 CenterY=-4.92017 CenterZ=0 NormalX=0 NormalY=0 NormalZ=1 AngleXU=0 Radius=3
    g2: Circle CenterX=23.851 CenterY=-4.92017 CenterZ=0 NormalX=0 NormalY=0 NormalZ=1 AngleXU=0 Radius=3
    g3: Circle CenterX=23.851 CenterY=-67.6202 CenterZ=0 NormalX=0 NormalY=0 NormalZ=1 AngleXU=0 Radius=3
    g4: Circle CenterX=23.851 CenterY=-67.6202 CenterZ=0 NormalX=0 NormalY=0 NormalZ=1 AngleXU=0 Radius=5
    g5: Circle CenterX=80.351 CenterY=-67.6202 CenterZ=0 NormalX=0 NormalY=0 NormalZ=1 AngleXU=0 Radius=5
    g6: Circle CenterX=23.851 CenterY=-4.92017 CenterZ=0 NormalX=0 NormalY=0 NormalZ=1 AngleXU=0 Radius=5
    g7: Circle CenterX=80.351 CenterY=-4.92017 CenterZ=0 NormalX=0 NormalY=0 NormalZ=1 AngleXU=0 Radius=5
  constraints (8):
    c: Block(g1)
    c: Block(g0)
    c: Block(g3)
    c: Block(g2)
    c: Block(g5)
    c: Block(g4)
    c: Block(g6)
    c: Block(g7)
FEATURE [Sketcher::SketchObject] Sketch062  label="topSketch016"
  FullyConstrained = true
  sketch-geometry (20):
    g0: LineSegment StartX=5.21097e-06 StartY=3 StartZ=0 EndX=5.21097e-06 EndY=19 EndZ=0
    g1: ArcOfCircle CenterX=19 CenterY=19 CenterZ=0 NormalX=0 NormalY=0 NormalZ=1 AngleXU=0 Radius=19 StartAngle=1.5708 EndAngle=3.14159
    g2: ArcOfCircle CenterX=19 CenterY=19 CenterZ=0 NormalX=0 NormalY=0 NormalZ=1 AngleXU=0 Radius=16 StartAngle=1.5708 EndAngle=3.14159
    g3: LineSegment StartX=114 StartY=35 StartZ=0 EndX=19 EndY=35 EndZ=0
    g4: LineSegment StartX=5.21097e-06 StartY=3 StartZ=0 EndX=5.21097e-06 EndY=0 EndZ=0
    g5: LineSegment StartX=3 StartY=0 StartZ=0 EndX=5.21097e-06 EndY=0 EndZ=0
    g6: LineSegment StartX=3 StartY=19 StartZ=0 EndX=3 EndY=0 EndZ=0
    g7: LineSegment StartX=19 StartY=38 StartZ=0 EndX=124 EndY=38 EndZ=0
    g8: Circle CenterX=119 CenterY=35 CenterZ=0 NormalX=0 NormalY=0 NormalZ=1 AngleXU=0 Radius=1
    g9: Circle CenterX=121 CenterY=35 CenterZ=0 NormalX=0 NormalY=0 NormalZ=1 AngleXU=0 Radius=1
    g10: Circle CenterX=121 CenterY=33 CenterZ=0 NormalX=0 NormalY=0 NormalZ=1 AngleXU=0 Radius=1
    g11: BSplineCurve PolesCount=3 KnotsCount=2 Degree=2 IsPeriodic=0
    g12: GeomPoint X=119 Y=35 Z=0
    g13: GeomPoint X=121 Y=33 Z=0
    g14: LineSegment StartX=119 StartY=35 StartZ=0 EndX=114 EndY=35 EndZ=0
    g15: ArcOfCircle CenterX=105 CenterY=19 CenterZ=0 NormalX=0 NormalY=0 NormalZ=1 AngleXU=0 Radius=19 StartAngle=5.7297 EndAngle=6.28319
    g16: ArcOfCircle CenterX=105 CenterY=19 CenterZ=0 NormalX=0 NormalY=0 NormalZ=1 AngleXU=0 Radius=16 StartAngle=5.60905 EndAngle=6.28319
    g17: LineSegment StartX=121 StartY=33 StartZ=0 EndX=121 EndY=19 EndZ=0
    g18: LineSegment StartX=124 StartY=38 StartZ=0 EndX=124 EndY=19 EndZ=0
    g19: LineSegment StartX=117.5 StartY=9.01251 StartZ=0 EndX=121.163 EndY=9.0125 EndZ=0
  constraints (46):
    c: Vertical(g0)
    c: Block(g0)
    c: Coincident(g1,g0)
    c: Block(g1)
    c: Coincident(g2,g1)
    c: Block(g2)
    c: Coincident(g3,g2)
    c: Horizontal(g3)
    c: Tangent(g3,g2)
    c: Coincident(g4,g0)
    c: Distance(g4) = 3
    c: Vertical(g4)
    c: Coincident(g5,g4)
    c: Horizontal(g5)
    c: Coincident(g6,g2)
    c: Coincident(g6,g5)
    c: Vertical(g6)
    c: Horizontal(g7)
    c: Distance(g7) = 105
    c: Coincident(g7,g1)
    c: Block(g3)
    c: Weight(g8) = 1
    c: Equal(g8,g9)
    c: Equal(g8,g10)
    c: InternalAlignment(g8,g11)
    c: InternalAlignment(g9,g11)
    c: InternalAlignment(g10,g11)
    c: InternalAlignment(g12,g11)
    c: InternalAlignment(g13,g11)
    c: Block(g11)
    c: Coincident(g14,g11)
    c: Coincident(g14,g3)
    c: Horizontal(g14)
    c: Block(g15)
    c: Coincident(g16,g15)
    c: Block(g16)
    c: Coincident(g17,g11)
    c: Coincident(g17,g16)
    c: Vertical(g17)
    c: Distance(g17) = 14
    c: Coincident(g18,g7)
    c: Coincident(g18,g15)
    c: Vertical(g18)
    c: Distance(g18) = 19
    c: Coincident(g19,g16)
    c: Coincident(g19,g15)
FEATURE [Part::Extrusion] Extrude053  label="top024"
  Base = -> Sketch062
  Dir = (0,0,1)
  DirMode = 2
  FaceMakerClass = Part::FaceMakerBullseye
  LengthFwd = 72
  LengthRev = 0
  Solid = true
  Symmetric = false
FEATURE [Sketcher::SketchObject] Sketch063
  FullyConstrained = true
  MapMode = 3
  Placement = pos=(0,0,0) rot=(1,0,0;1.5708rad)
  Support = -> [Extrude053]
  sketch-geometry (8):
    g0: Circle CenterX=80.351 CenterY=-67.6202 CenterZ=0 NormalX=0 NormalY=0 NormalZ=1 AngleXU=0 Radius=2
    g1: Circle CenterX=80.351 CenterY=-67.6202 CenterZ=0 NormalX=0 NormalY=0 NormalZ=1 AngleXU=0 Radius=3
    g2: Circle CenterX=80.351 CenterY=-4.92017 CenterZ=0 NormalX=0 NormalY=0 NormalZ=1 AngleXU=0 Radius=2
    g3: Circle CenterX=80.351 CenterY=-4.92017 CenterZ=0 NormalX=0 NormalY=0 NormalZ=1 AngleXU=0 Radius=3
    g4: Circle CenterX=23.851 CenterY=-4.92017 CenterZ=0 NormalX=0 NormalY=0 NormalZ=1 AngleXU=0 Radius=2
    g5: Circle CenterX=23.851 CenterY=-4.92017 CenterZ=0 NormalX=0 NormalY=0 NormalZ=1 AngleXU=0 Radius=3
    g6: Circle CenterX=23.851 CenterY=-67.6202 CenterZ=0 NormalX=0 NormalY=0 NormalZ=1 AngleXU=0 Radius=2
    g7: Circle CenterX=23.851 CenterY=-67.6202 CenterZ=0 NormalX=0 NormalY=0 NormalZ=1 AngleXU=0 Radius=3
  constraints (8):
    c: Block(g3)
    c: Block(g2)
    c: Block(g1)
    c: Block(g0)
    c: Block(g6)
    c: Block(g7)
    c: Block(g4)
    c: Block(g5)
FEATURE [Part::Extrusion] Extrude054
  Base = -> Sketch063
  Dir = (0,-1,2e-16)
  DirMode = 2
  FaceMakerClass = Part::FaceMakerBullseye
  LengthFwd = 6
  LengthRev = 0
  Placement = pos=(0,9,0) rot=(0,0,1;0rad)
  Solid = true
  Symmetric = false
FEATURE [Sketcher::SketchObject] Sketch064  label="topSketch017"
  FullyConstrained = true
  sketch-geometry (20):
    g0: LineSegment StartX=5.21097e-06 StartY=3 StartZ=0 EndX=5.21097e-06 EndY=19 EndZ=0
    g1: ArcOfCircle CenterX=19 CenterY=19 CenterZ=0 NormalX=0 NormalY=0 NormalZ=1 AngleXU=0 Radius=19 StartAngle=1.5708 EndAngle=3.14159
    g2: ArcOfCircle CenterX=19 CenterY=19 CenterZ=0 NormalX=0 NormalY=0 NormalZ=1 AngleXU=0 Radius=16 StartAngle=1.5708 EndAngle=3.14159
    g3: LineSegment StartX=114 StartY=35 StartZ=0 EndX=19 EndY=35 EndZ=0
    g4: LineSegment StartX=5.21097e-06 StartY=3 StartZ=0 EndX=5.21097e-06 EndY=0 EndZ=0
    g5: LineSegment StartX=3 StartY=0 StartZ=0 EndX=5.21097e-06 EndY=0 EndZ=0
    g6: LineSegment StartX=3 StartY=19 StartZ=0 EndX=3 EndY=0 EndZ=0
    g7: LineSegment StartX=19 StartY=38 StartZ=0 EndX=124 EndY=38 EndZ=0
    g8: Circle CenterX=119 CenterY=35 CenterZ=0 NormalX=0 NormalY=0 NormalZ=1 AngleXU=0 Radius=1
    g9: Circle CenterX=121 CenterY=35 CenterZ=0 NormalX=0 NormalY=0 NormalZ=1 AngleXU=0 Radius=1
    g10: Circle CenterX=121 CenterY=33 CenterZ=0 NormalX=0 NormalY=0 NormalZ=1 AngleXU=0 Radius=1
    g11: BSplineCurve PolesCount=3 KnotsCount=2 Degree=2 IsPeriodic=0
    g12: GeomPoint X=119 Y=35 Z=0
    g13: GeomPoint X=121 Y=33 Z=0
    g14: LineSegment StartX=119 StartY=35 StartZ=0 EndX=114 EndY=35 EndZ=0
    g15: ArcOfCircle CenterX=105 CenterY=19 CenterZ=0 NormalX=0 NormalY=0 NormalZ=1 AngleXU=0 Radius=19 StartAngle=5.7297 EndAngle=6.28319
    g16: ArcOfCircle CenterX=105 CenterY=19 CenterZ=0 NormalX=0 NormalY=0 NormalZ=1 AngleXU=0 Radius=16 StartAngle=5.60905 EndAngle=6.28319
    g17: LineSegment StartX=121 StartY=33 StartZ=0 EndX=121 EndY=19 EndZ=0
    g18: LineSegment StartX=124 StartY=38 StartZ=0 EndX=124 EndY=19 EndZ=0
    g19: LineSegment StartX=117.5 StartY=9.01251 StartZ=0 EndX=121.163 EndY=9.0125 EndZ=0
  constraints (46):
    c: Vertical(g0)
    c: Block(g0)
    c: Coincident(g1,g0)
    c: Block(g1)
    c: Coincident(g2,g1)
    c: Block(g2)
    c: Coincident(g3,g2)
    c: Horizontal(g3)
    c: Tangent(g3,g2)
    c: Coincident(g4,g0)
    c: Distance(g4) = 3
    c: Vertical(g4)
    c: Coincident(g5,g4)
    c: Horizontal(g5)
    c: Coincident(g6,g2)
    c: Coincident(g6,g5)
    c: Vertical(g6)
    c: Horizontal(g7)
    c: Distance(g7) = 105
    c: Coincident(g7,g1)
    c: Block(g3)
    c: Weight(g8) = 1
    c: Equal(g8,g9)
    c: Equal(g8,g10)
    c: InternalAlignment(g8,g11)
    c: InternalAlignment(g9,g11)
    c: InternalAlignment(g10,g11)
    c: InternalAlignment(g12,g11)
    c: InternalAlignment(g13,g11)
    c: Block(g11)
    c: Coincident(g14,g11)
    c: Coincident(g14,g3)
    c: Horizontal(g14)
    c: Block(g15)
    c: Coincident(g16,g15)
    c: Block(g16)
    c: Coincident(g17,g11)
    c: Coincident(g17,g16)
    c: Vertical(g17)
    c: Distance(g17) = 14
    c: Coincident(g18,g7)
    c: Coincident(g18,g15)
    c: Vertical(g18)
    c: Distance(g18) = 19
    c: Coincident(g19,g16)
    c: Coincident(g19,g15)
FEATURE [Sketcher::SketchObject] Sketch065
  FullyConstrained = true
  MapMode = 3
  Placement = pos=(0,0,0) rot=(1,0,0;1.5708rad)
  sketch-geometry (8):
    g0: Circle CenterX=80.351 CenterY=-67.6202 CenterZ=0 NormalX=0 NormalY=0 NormalZ=1 AngleXU=0 Radius=3
    g1: Circle CenterX=80.351 CenterY=-4.92017 CenterZ=0 NormalX=0 NormalY=0 NormalZ=1 AngleXU=0 Radius=3
    g2: Circle CenterX=23.851 CenterY=-4.92017 CenterZ=0 NormalX=0 NormalY=0 NormalZ=1 AngleXU=0 Radius=3
    g3: Circle CenterX=23.851 CenterY=-67.6202 CenterZ=0 NormalX=0 NormalY=0 NormalZ=1 AngleXU=0 Radius=3
    g4: Circle CenterX=23.851 CenterY=-67.6202 CenterZ=0 NormalX=0 NormalY=0 NormalZ=1 AngleXU=0 Radius=5
    g5: Circle CenterX=80.351 CenterY=-67.6202 CenterZ=0 NormalX=0 NormalY=0 NormalZ=1 AngleXU=0 Radius=5
    g6: Circle CenterX=23.851 CenterY=-4.92017 CenterZ=0 NormalX=0 NormalY=0 NormalZ=1 AngleXU=0 Radius=5
    g7: Circle CenterX=80.351 CenterY=-4.92017 CenterZ=0 NormalX=0 NormalY=0 NormalZ=1 AngleXU=0 Radius=5
  constraints (8):
    c: Block(g1)
    c: Block(g0)
    c: Block(g3)
    c: Block(g2)
    c: Block(g5)
    c: Block(g4)
    c: Block(g6)
    c: Block(g7)
FEATURE [Part::Extrusion] Extrude056
  Base = -> Sketch065
  Dir = (0,-1,2e-16)
  DirMode = 2
  FaceMakerClass = Part::FaceMakerBullseye
  LengthFwd = 2
  LengthRev = 0
  Solid = true
  Symmetric = false
FEATURE [Part::Extrusion] Extrude057  label="top025"
  Base = -> Sketch064
  Dir = (0,0,1)
  DirMode = 2
  FaceMakerClass = Part::FaceMakerBullseye
  LengthFwd = 72
  LengthRev = 0
  Solid = true
  Symmetric = false
FEATURE [Sketcher::SketchObject] Sketch066
  FullyConstrained = true
  MapMode = 3
  Placement = pos=(0,0,0) rot=(1,0,0;1.5708rad)
  Support = -> [Extrude057]
  sketch-geometry (8):
    g0: Circle CenterX=80.351 CenterY=-67.6202 CenterZ=0 NormalX=0 NormalY=0 NormalZ=1 AngleXU=0 Radius=3
    g1: Circle CenterX=80.351 CenterY=-4.92017 CenterZ=0 NormalX=0 NormalY=0 NormalZ=1 AngleXU=0 Radius=3
    g2: Circle CenterX=23.851 CenterY=-4.92017 CenterZ=0 NormalX=0 NormalY=0 NormalZ=1 AngleXU=0 Radius=3
    g3: Circle CenterX=23.851 CenterY=-67.6202 CenterZ=0 NormalX=0 NormalY=0 NormalZ=1 AngleXU=0 Radius=3
    g4: Circle CenterX=23.851 CenterY=-67.6202 CenterZ=0 NormalX=0 NormalY=0 NormalZ=1 AngleXU=0 Radius=5
    g5: Circle CenterX=80.351 CenterY=-67.6202 CenterZ=0 NormalX=0 NormalY=0 NormalZ=1 AngleXU=0 Radius=5
    g6: Circle CenterX=23.851 CenterY=-4.92017 CenterZ=0 NormalX=0 NormalY=0 NormalZ=1 AngleXU=0 Radius=5
    g7: Circle CenterX=80.351 CenterY=-4.92017 CenterZ=0 NormalX=0 NormalY=0 NormalZ=1 AngleXU=0 Radius=5
  constraints (8):
    c: Block(g1)
    c: Block(g0)
    c: Block(g3)
    c: Block(g2)
    c: Block(g5)
    c: Block(g4)
    c: Block(g6)
    c: Block(g7)
FEATURE [Part::Extrusion] Extrude055
  Base = -> Sketch066
  Dir = (0,-1,2e-16)
  DirMode = 2
  FaceMakerClass = Part::FaceMakerBullseye
  LengthFwd = 2
  LengthRev = 0
  Solid = true
  Symmetric = false
FEATURE [Part::Fillet] Fillet041
  Base = -> Extrude056
  Edges = 4 edges r=1.99: [Edge6,Edge12,Edge18,Edge24]
FEATURE [Part::Cut] Cut045
  Base = -> Extrude055
  Placement = pos=(0,6,0) rot=(0,0,1;0rad)
  Tool = -> Fillet041
FEATURE [Part::MultiFuse] Fusion095  label="pcbScrewPillars"
  Placement = pos=(-3.2,-1,72.3) rot=(0,0,1;0rad)
  Shapes = -> [Cut045,Extrude054]
FEATURE [Part::Feature] Face113
  shape: bbox 3.2 x 1.5 x 2e-07 mm, 1 faces, 0 solids (baked)
FEATURE [Part::Revolution] Revolve121  label="backCaseScrewRetainer002"
  Angle = 360
  Axis = (0,1,0)
  Base = (0,0,0)
  FaceMakerClass = Part::FaceMakerBullseye
  Placement = pos=(12.5,3,62) rot=(0,0,1;0rad)
  Solid = false
  Source = -> Face113
  Symmetric = false
FEATURE [Part::Feature] Face114
  shape: bbox 3.2 x 1.5 x 2e-07 mm, 1 faces, 0 solids (baked)
FEATURE [Part::Feature] Face115
  shape: bbox 3.2 x 1.5 x 2e-07 mm, 1 faces, 0 solids (baked)
FEATURE [Part::Feature] Face116
  shape: bbox 3.2 x 1.5 x 2e-07 mm, 1 faces, 0 solids (baked)
FEATURE [Part::Revolution] Revolve122  label="frontCaseScrewRetainer004"
  Angle = 360
  Axis = (0,1,0)
  Base = (0,0,0)
  FaceMakerClass = Part::FaceMakerBullseye
  Placement = pos=(89.5,3,68.5) rot=(0,0,1;0rad)
  Solid = false
  Source = -> Face115
  Symmetric = false
FEATURE [Part::Revolution] Revolve123  label="frontCaseScrewRetainer005"
  Angle = 360
  Axis = (0,1,0)
  Base = (0,0,0)
  FaceMakerClass = Part::FaceMakerBullseye
  Placement = pos=(89.5,3,3.5) rot=(0,0,1;0rad)
  Solid = false
  Source = -> Face116
  Symmetric = false
FEATURE [Part::Revolution] Revolve124  label="backCaseScrewRetainer003"
  Angle = 360
  Axis = (0,1,0)
  Base = (0,0,0)
  FaceMakerClass = Part::FaceMakerBullseye
  Placement = pos=(12.5,3,10) rot=(0,0,1;0rad)
  Solid = false
  Source = -> Face114
  Symmetric = false
FEATURE [Part::Feature] Face117
  shape: bbox 3.6 x 3.2 x 2e-07 mm, 1 faces, 0 solids (baked)
FEATURE [Part::Revolution] Revolve125  label="moreFrontCaseScrewRetainer004"
  Angle = 360
  Axis = (0,1,0)
  Base = (0,0,0)
  FaceMakerClass = Part::FaceMakerBullseye
  Placement = pos=(109.5,4.5,68.5) rot=(0,0,1;0rad)
  Solid = false
  Source = -> Face117
  Symmetric = false
FEATURE [Part::Feature] Face118
  shape: bbox 3.6 x 3.2 x 2e-07 mm, 1 faces, 0 solids (baked)
FEATURE [Part::Revolution] Revolve126  label="moreFrontCaseScrewRetainer005"
  Angle = 360
  Axis = (0,1,0)
  Base = (0,0,0)
  FaceMakerClass = Part::FaceMakerBullseye
  Placement = pos=(109.5,4.5,3.5) rot=(0,0,1;0rad)
  Solid = false
  Source = -> Face118
  Symmetric = false
FEATURE [Part::MultiFuse] Fusion096  label="screwRetainers001"
  Shapes = -> [Revolve126,Revolve125,Revolve124,Revolve123,Revolve122,Revolve121]
FEATURE [Part::Feature] Face119
  shape: bbox 10 x 16.5 x 2e-07 mm, 1 faces, 0 solids (baked)
FEATURE [Part::Revolution] Revolve130  label="plugHousing050"
  Angle = 360
  Axis = (0,1,0)
  Base = (0,0,0)
  FaceMakerClass = Part::FaceMakerBullseye
  Placement = pos=(0,0,36.15) rot=(0,0,1;0rad)
  Solid = false
  Source = -> Face119
  Symmetric = false
FEATURE [Part::Feature] Face120
  shape: bbox 10 x 16.5 x 2e-07 mm, 1 faces, 0 solids (baked)
FEATURE [Part::Feature] Face121
  shape: bbox 10 x 16.5 x 2e-07 mm, 1 faces, 0 solids (baked)
FEATURE [Part::Revolution] Revolve127  label="plugHousing047"
  Angle = 360
  Axis = (0,1,0)
  Base = (0,0,0)
  FaceMakerClass = Part::FaceMakerBullseye
  Placement = pos=(0,0,36.15) rot=(0,0,1;0rad)
  Solid = false
  Source = -> Face121
  Symmetric = false
FEATURE [Part::Feature] Face122
  shape: bbox 10 x 16.5 x 2e-07 mm, 1 faces, 0 solids (baked)
FEATURE [Part::Feature] Face123
  shape: bbox 10 x 16.5 x 2e-07 mm, 1 faces, 0 solids (baked)
FEATURE [Part::Revolution] Revolve128  label="plugHousing048"
  Angle = 360
  Axis = (0,1,0)
  Base = (0,0,0)
  FaceMakerClass = Part::FaceMakerBullseye
  Placement = pos=(0,0,36.15) rot=(0,0,1;0rad)
  Solid = false
  Source = -> Face123
  Symmetric = false
FEATURE [Part::MultiFuse] Fusion100  label="plugHousing054"
  Placement = pos=(0,0,0) rot=(0,0,1;1.5708rad)
  Shapes = -> [Revolve130,Revolve128]
FEATURE [Part::Feature] Face124
  shape: bbox 10 x 16.5 x 2e-07 mm, 1 faces, 0 solids (baked)
FEATURE [Part::Feature] Face125
  shape: bbox 10 x 16.5 x 2e-07 mm, 1 faces, 0 solids (baked)
FEATURE [Part::Revolution] Revolve129  label="plugHousing049"
  Angle = 360
  Axis = (0,1,0)
  Base = (0,0,0)
  FaceMakerClass = Part::FaceMakerBullseye
  Placement = pos=(0,0,36.15) rot=(0,0,1;0rad)
  Solid = false
  Source = -> Face125
  Symmetric = false
FEATURE [Part::Feature] Face126
  shape: bbox 10 x 16.5 x 2e-07 mm, 1 faces, 0 solids (baked)
FEATURE [Part::Revolution] Revolve131  label="plugHousing058"
  Angle = 360
  Axis = (0,1,0)
  Base = (0,0,0)
  FaceMakerClass = Part::FaceMakerBullseye
  Placement = pos=(0,0,36.15) rot=(0,0,1;0rad)
  Solid = false
  Source = -> Face120
  Symmetric = false
FEATURE [Part::MultiFuse] Fusion099  label="plugHousing053"
  Placement = pos=(0,0,0) rot=(0,0,1;1.5708rad)
  Shapes = -> [Revolve127,Revolve131]
FEATURE [Part::MultiFuse] Fusion102  label="plugHousing056"
  Placement = pos=(0,19,0) rot=(0,0,1;3.14159rad)
  Shapes = -> [Fusion100,Fusion099]
FEATURE [Part::Revolution] Revolve132  label="plugHousing059"
  Angle = 360
  Axis = (0,1,0)
  Base = (0,0,0)
  FaceMakerClass = Part::FaceMakerBullseye
  Placement = pos=(0,0,36.15) rot=(0,0,1;0rad)
  Solid = false
  Source = -> Face126
  Symmetric = false
FEATURE [Part::Revolution] Revolve133  label="plugHousing060"
  Angle = 360
  Axis = (0,1,0)
  Base = (0,0,0)
  FaceMakerClass = Part::FaceMakerBullseye
  Placement = pos=(0,0,36.15) rot=(0,0,1;0rad)
  Solid = false
  Source = -> Face122
  Symmetric = false
FEATURE [Part::MultiFuse] Fusion097  label="plugHousing051"
  Placement = pos=(0,0,0) rot=(0,0,1;1.5708rad)
  Shapes = -> [Revolve133,Revolve132]
FEATURE [Part::Revolution] Revolve134  label="plugHousing061"
  Angle = 360
  Axis = (0,1,0)
  Base = (0,0,0)
  FaceMakerClass = Part::FaceMakerBullseye
  Placement = pos=(0,0,36.15) rot=(0,0,1;0rad)
  Solid = false
  Source = -> Face124
  Symmetric = false
FEATURE [Part::MultiFuse] Fusion101  label="plugHousing055"
  Placement = pos=(0,0,0) rot=(0,0,1;1.5708rad)
  Shapes = -> [Revolve129,Revolve134]
FEATURE [Part::MultiFuse] Fusion098  label="plugHousing052"
  Placement = pos=(0,19,0) rot=(0,0,1;3.14159rad)
  Shapes = -> [Fusion097,Fusion101]
FEATURE [Part::MultiFuse] Fusion103  label="plugHousing057"
  Placement = pos=(122.621,0,-0.15) rot=(0,0,1;0rad)
  Shapes = -> [Fusion102,Fusion098]
FEATURE [Part::Box] Box028  label="Cube015"
  AttacherType = Attacher::AttachEngine3D
  Height = 28
  Length = 3
  Placement = pos=(110.7,19,22) rot=(0,0,1;0rad)
  Width = 15.7
FEATURE [Part::Cylinder] Cylinder044
  Angle = 360
  AttacherType = Attacher::AttachEngine3D
  Height = 20
  Placement = pos=(0,0,36.15) rot=(0,0,1;0rad)
  Radius = 10.3
FEATURE [Part::Cylinder] Cylinder045
  Angle = 360
  AttacherType = Attacher::AttachEngine3D
  Height = 10
  Placement = pos=(0,0,36.15) rot=(0,0,1;0rad)
  Radius = 4
FEATURE [Part::MultiFuse] Fusion104  label="removeToCreteHoleForPlugHousing040"
  Placement = pos=(70,19,36) rot=(0,1,0;1.5708rad)
  Shapes = -> [Cylinder044,Cylinder045]
FEATURE [Part::Cut] Cut046  label="plugHousingTab003"
  Base = -> Box028
  Tool = -> Fusion104
FEATURE [Part::MultiFuse] Fusion105  label="plugHousing062"
  Shapes = -> [Fusion103,Cut046]
FEATURE [Part::Fillet] Fillet042
  Base = -> Fusion105
  Edges = 1 edges r=2: [Edge25]
FEATURE [Part::Fillet] Fillet043  label="plugHousing063"
  Base = -> Fillet042
  Edges = 1 edges r=2: [Edge8]
  Placement = pos=(7,0,0) rot=(0,0,1;0rad)
FEATURE [Part::Feature] Face127
  shape: bbox 10 x 16.5 x 2e-07 mm, 1 faces, 0 solids (baked)
FEATURE [Part::Feature] Face128
  shape: bbox 10 x 16.5 x 2e-07 mm, 1 faces, 0 solids (baked)
FEATURE [Part::Revolution] Revolve137  label="plugHousing070"
  Angle = 360
  Axis = (0,1,0)
  Base = (0,0,0)
  FaceMakerClass = Part::FaceMakerBullseye
  Placement = pos=(0,0,36.15) rot=(0,0,1;0rad)
  Solid = false
  Source = -> Face127
  Symmetric = false
FEATURE [Part::Revolution] Revolve140  label="plugHousing073"
  Angle = 360
  Axis = (0,1,0)
  Base = (0,0,0)
  FaceMakerClass = Part::FaceMakerBullseye
  Placement = pos=(0,0,36.15) rot=(0,0,1;0rad)
  Solid = false
  Source = -> Face128
  Symmetric = false
FEATURE [Part::Feature] Face129
  shape: bbox 10 x 16.5 x 2e-07 mm, 1 faces, 0 solids (baked)
FEATURE [Part::Revolution] Revolve138  label="plugHousing071"
  Angle = 360
  Axis = (0,1,0)
  Base = (0,0,0)
  FaceMakerClass = Part::FaceMakerBullseye
  Placement = pos=(0,0,36.15) rot=(0,0,1;0rad)
  Solid = false
  Source = -> Face129
  Symmetric = false
FEATURE [Part::Feature] Face130
  shape: bbox 10 x 16.5 x 2e-07 mm, 1 faces, 0 solids (baked)
FEATURE [Part::Revolution] Revolve139  label="plugHousing072"
  Angle = 360
  Axis = (0,1,0)
  Base = (0,0,0)
  FaceMakerClass = Part::FaceMakerBullseye
  Placement = pos=(0,0,36.15) rot=(0,0,1;0rad)
  Solid = false
  Source = -> Face130
  Symmetric = false
FEATURE [Part::Feature] Face131
  shape: bbox 10 x 16.5 x 2e-07 mm, 1 faces, 0 solids (baked)
FEATURE [Part::Revolution] Revolve135  label="plugHousing068"
  Angle = 360
  Axis = (0,1,0)
  Base = (0,0,0)
  FaceMakerClass = Part::FaceMakerBullseye
  Placement = pos=(0,0,36.15) rot=(0,0,1;0rad)
  Solid = false
  Source = -> Face131
  Symmetric = false
FEATURE [Part::MultiFuse] Fusion112  label="plugHousing078"
  Placement = pos=(0,0,0) rot=(0,0,1;1.5708rad)
  Shapes = -> [Revolve135,Revolve139]
FEATURE [Part::Feature] Face132
  shape: bbox 10 x 16.5 x 2e-07 mm, 1 faces, 0 solids (baked)
FEATURE [Part::Revolution] Revolve141  label="plugHousing074"
  Angle = 360
  Axis = (0,1,0)
  Base = (0,0,0)
  FaceMakerClass = Part::FaceMakerBullseye
  Placement = pos=(0,0,36.15) rot=(0,0,1;0rad)
  Solid = false
  Source = -> Face132
  Symmetric = false
FEATURE [Part::MultiFuse] Fusion110  label="plugHousing076"
  Placement = pos=(0,0,0) rot=(0,0,1;1.5708rad)
  Shapes = -> [Revolve141,Revolve140]
FEATURE [Part::Feature] Face133
  shape: bbox 10 x 16.5 x 2e-07 mm, 1 faces, 0 solids (baked)
FEATURE [Part::Revolution] Revolve136  label="plugHousing069"
  Angle = 360
  Axis = (0,1,0)
  Base = (0,0,0)
  FaceMakerClass = Part::FaceMakerBullseye
  Placement = pos=(0,0,36.15) rot=(0,0,1;0rad)
  Solid = false
  Source = -> Face133
  Symmetric = false
FEATURE [Part::MultiFuse] Fusion106  label="plugHousing064"
  Placement = pos=(0,0,0) rot=(0,0,1;1.5708rad)
  Shapes = -> [Revolve138,Revolve136]
FEATURE [Part::MultiFuse] Fusion108  label="plugHousing066"
  Placement = pos=(0,19,0) rot=(0,0,1;3.14159rad)
  Shapes = -> [Fusion106,Fusion112]
FEATURE [Part::Feature] Face134
  shape: bbox 10 x 16.5 x 2e-07 mm, 1 faces, 0 solids (baked)
FEATURE [Part::Revolution] Revolve142  label="plugHousing075"
  Angle = 360
  Axis = (0,1,0)
  Base = (0,0,0)
  FaceMakerClass = Part::FaceMakerBullseye
  Placement = pos=(0,0,36.15) rot=(0,0,1;0rad)
  Solid = false
  Source = -> Face134
  Symmetric = false
FEATURE [Part::MultiFuse] Fusion107  label="plugHousing065"
  Placement = pos=(0,0,0) rot=(0,0,1;1.5708rad)
  Shapes = -> [Revolve137,Revolve142]
FEATURE [Part::MultiFuse] Fusion111  label="plugHousing077"
  Placement = pos=(0,19,0) rot=(0,0,1;3.14159rad)
  Shapes = -> [Fusion110,Fusion107]
FEATURE [Part::MultiFuse] Fusion109  label="plugHousing067"
  Placement = pos=(131.236,0,-0.15) rot=(0,0,1;0rad)
  Shapes = -> [Fusion108,Fusion111]
FEATURE [Part::MultiFuse] Fusion113  label="plugHousing079"
  Shapes = -> [Fillet043,Fusion109]
FEATURE [Part::Feature] Face135
  shape: bbox 3.5 x 17.8 x 2e-07 mm, 1 faces, 0 solids (baked)
FEATURE [Part::Revolution] Revolve143  label="removeToCreateScrewAndThreadedInsertHole049"
  Angle = 360
  Axis = (0,1,0)
  Base = (0,0,0)
  FaceMakerClass = Part::FaceMakerBullseye
  Placement = pos=(12.5,0,10) rot=(0,0,1;0rad)
  Solid = false
  Source = -> Face135
  Symmetric = false
FEATURE [Part::Feature] Face136
  shape: bbox 3.5 x 17.8 x 2e-07 mm, 1 faces, 0 solids (baked)
FEATURE [Part::Revolution] Revolve144  label="removeToCreateScrewAndThreadedInsertHole050"
  Angle = 360
  Axis = (0,1,0)
  Base = (0,0,0)
  FaceMakerClass = Part::FaceMakerBullseye
  Placement = pos=(12.5,0,62) rot=(0,0,1;0rad)
  Solid = false
  Source = -> Face136
  Symmetric = false
FEATURE [Part::Feature] Face137
  shape: bbox 3.5 x 17.8 x 2e-07 mm, 1 faces, 0 solids (baked)
FEATURE [Part::Revolution] Revolve145  label="removeToCreateScrewAndThreadedInsertHole051"
  Angle = 360
  Axis = (0,1,0)
  Base = (0,0,0)
  FaceMakerClass = Part::FaceMakerBullseye
  Placement = pos=(89.5,0,68.5) rot=(0,0,1;0rad)
  Solid = false
  Source = -> Face137
  Symmetric = false
FEATURE [Part::Feature] Face138
  shape: bbox 3.5 x 17.8 x 2e-07 mm, 1 faces, 0 solids (baked)
FEATURE [Part::Revolution] Revolve146  label="removeToCreateScrewAndThreadedInsertHole052"
  Angle = 360
  Axis = (0,1,0)
  Base = (0,0,0)
  FaceMakerClass = Part::FaceMakerBullseye
  Placement = pos=(89.5,0,3.5) rot=(0,0,1;0rad)
  Solid = false
  Source = -> Face138
  Symmetric = false
FEATURE [Part::Feature] Face139
  shape: bbox 3.5 x 17.8 x 2e-07 mm, 1 faces, 0 solids (baked)
FEATURE [Part::Revolution] Revolve147  label="removeToCreateScrewAndThreadedInsertHole053"
  Angle = 360
  Axis = (0,1,0)
  Base = (0,0,0)
  FaceMakerClass = Part::FaceMakerBullseye
  Placement = pos=(109.5,4.7,3.5) rot=(0,0,1;0rad)
  Solid = false
  Source = -> Face139
  Symmetric = false
FEATURE [Part::Feature] Face140
  shape: bbox 3.5 x 17.8 x 2e-07 mm, 1 faces, 0 solids (baked)
FEATURE [Part::Revolution] Revolve148  label="removeToCreateScrewAndThreadedInsertHole054"
  Angle = 360
  Axis = (0,1,0)
  Base = (0,0,0)
  FaceMakerClass = Part::FaceMakerBullseye
  Placement = pos=(109.5,4.7,68.5) rot=(0,0,1;0rad)
  Solid = false
  Source = -> Face140
  Symmetric = false
FEATURE [Part::MultiFuse] Fusion114  label="removeToCreateScrewAndThreadedInsertHole055"
  Shapes = -> [Revolve148,Revolve147,Revolve146,Revolve145,Revolve144,Revolve143]
FEATURE [Part::Cut] Cut047  label="casePillars004"
  Base = -> Cut037
  Tool = -> Fusion114
FEATURE [Part::Feature] Face141
  shape: bbox 3.5 x 17.8 x 2e-07 mm, 1 faces, 0 solids (baked)
FEATURE [Part::Feature] Face142
  shape: bbox 3.5 x 17.8 x 2e-07 mm, 1 faces, 0 solids (baked)
FEATURE [Part::Feature] Face143
  shape: bbox 3.5 x 17.8 x 2e-07 mm, 1 faces, 0 solids (baked)
FEATURE [Part::Revolution] Revolve149  label="removeToCreateScrewAndThreadedInsertHole057"
  Angle = 360
  Axis = (0,1,0)
  Base = (0,0,0)
  FaceMakerClass = Part::FaceMakerBullseye
  Placement = pos=(12.5,0,10) rot=(0,0,1;0rad)
  Solid = false
  Source = -> Face141
  Symmetric = false
FEATURE [Part::Feature] Face144
  shape: bbox 3.5 x 17.8 x 2e-07 mm, 1 faces, 0 solids (baked)
FEATURE [Part::Feature] Face145
  shape: bbox 3.5 x 17.8 x 2e-07 mm, 1 faces, 0 solids (baked)
FEATURE [Part::Feature] Face146
  shape: bbox 3.5 x 17.8 x 2e-07 mm, 1 faces, 0 solids (baked)
FEATURE [Part::Revolution] Revolve150  label="removeToCreateScrewAndThreadedInsertHole058"
  Angle = 360
  Axis = (0,1,0)
  Base = (0,0,0)
  FaceMakerClass = Part::FaceMakerBullseye
  Placement = pos=(12.5,0,62) rot=(0,0,1;0rad)
  Solid = false
  Source = -> Face146
  Symmetric = false
FEATURE [Part::Revolution] Revolve151  label="removeToCreateScrewAndThreadedInsertHole059"
  Angle = 360
  Axis = (0,1,0)
  Base = (0,0,0)
  FaceMakerClass = Part::FaceMakerBullseye
  Placement = pos=(89.5,0,68.5) rot=(0,0,1;0rad)
  Solid = false
  Source = -> Face143
  Symmetric = false
FEATURE [Part::Revolution] Revolve152  label="removeToCreateScrewAndThreadedInsertHole060"
  Angle = 360
  Axis = (0,1,0)
  Base = (0,0,0)
  FaceMakerClass = Part::FaceMakerBullseye
  Placement = pos=(89.5,0,3.5) rot=(0,0,1;0rad)
  Solid = false
  Source = -> Face142
  Symmetric = false
FEATURE [Part::Revolution] Revolve153  label="removeToCreateScrewAndThreadedInsertHole061"
  Angle = 360
  Axis = (0,1,0)
  Base = (0,0,0)
  FaceMakerClass = Part::FaceMakerBullseye
  Placement = pos=(109.5,4.7,3.5) rot=(0,0,1;0rad)
  Solid = false
  Source = -> Face145
  Symmetric = false
FEATURE [Part::Revolution] Revolve154  label="removeToCreateScrewAndThreadedInsertHole062"
  Angle = 360
  Axis = (0,1,0)
  Base = (0,0,0)
  FaceMakerClass = Part::FaceMakerBullseye
  Placement = pos=(109.5,4.7,68.5) rot=(0,0,1;0rad)
  Solid = false
  Source = -> Face144
  Symmetric = false
FEATURE [Part::MultiFuse] Fusion115  label="removeToCreateScrewAndThreadedInsertHole056"
  Shapes = -> [Revolve154,Revolve153,Revolve152,Revolve151,Revolve150,Revolve149]
FEATURE [Part::Feature] Face147
  shape: bbox 9.8 x 26.5 x 2e-07 mm, 1 faces, 0 solids (baked)
FEATURE [Part::Revolution] Revolve155
  Angle = 360
  Axis = (0,1,0)
  Base = (0,0,0)
  FaceMakerClass = Part::FaceMakerBullseye
  Placement = pos=(0,0,0) rot=(0,0,1;1.5708rad)
  Solid = false
  Source = -> Face147
  Symmetric = false
FEATURE [Part::Feature] Face148
  shape: bbox 9.8 x 26.5 x 2e-07 mm, 1 faces, 0 solids (baked)
FEATURE [Part::Revolution] Revolve156
  Angle = 360
  Axis = (0,1,0)
  Base = (0,0,0)
  FaceMakerClass = Part::FaceMakerBullseye
  Placement = pos=(0,0,0) rot=(0,0,1;1.5708rad)
  Solid = false
  Source = -> Face148
  Symmetric = false
FEATURE [Part::MultiFuse] Fusion116
  Placement = pos=(-18,19,36) rot=(0,0,1;0rad)
  Shapes = -> [Revolve156,Revolve155]
FEATURE [Part::Box] Box029  label="Cube016"
  AttacherType = Attacher::AttachEngine3D
  Height = 28
  Length = 3
  Placement = pos=(110.7,19,22) rot=(0,0,1;0rad)
  Width = 15.7
FEATURE [Part::Cylinder] Cylinder046
  Angle = 360
  AttacherType = Attacher::AttachEngine3D
  Height = 10
  Placement = pos=(0,0,36.15) rot=(0,0,1;0rad)
  Radius = 4
FEATURE [Part::Cylinder] Cylinder047
  Angle = 360
  AttacherType = Attacher::AttachEngine3D
  Height = 20
  Placement = pos=(0,0,36.15) rot=(0,0,1;0rad)
  Radius = 10.3
FEATURE [Part::MultiFuse] Fusion117  label="removeToCreteHoleForPlugHousing041"
  Placement = pos=(70,19,36) rot=(0,1,0;1.5708rad)
  Shapes = -> [Cylinder047,Cylinder046]
FEATURE [Part::Cut] Cut049  label="plugHousingTab004"
  Base = -> Box029
  Placement = pos=(-107.4,-14,0) rot=(0,0,1;0rad)
  Tool = -> Fusion117
FEATURE [Part::Box] Box030  label="Cube017"
  AttacherType = Attacher::AttachEngine3D
  Height = 28
  Length = 3
  Placement = pos=(110.7,19,22) rot=(0,0,1;0rad)
  Width = 15.7
FEATURE [Part::Cylinder] Cylinder048
  Angle = 360
  AttacherType = Attacher::AttachEngine3D
  Height = 10
  Placement = pos=(0,0,36.15) rot=(0,0,1;0rad)
  Radius = 4
FEATURE [Part::Cylinder] Cylinder049
  Angle = 360
  AttacherType = Attacher::AttachEngine3D
  Height = 20
  Placement = pos=(0,0,36.15) rot=(0,0,1;0rad)
  Radius = 10.3
FEATURE [Part::MultiFuse] Fusion118  label="removeToCreteHoleForPlugHousing042"
  Placement = pos=(70,19,36) rot=(0,1,0;1.5708rad)
  Shapes = -> [Cylinder049,Cylinder048]
FEATURE [Part::Cut] Cut050  label="plugHousingTab005"
  Base = -> Box030
  Placement = pos=(-107.4,-14,0) rot=(0,0,1;0rad)
  Tool = -> Fusion118
FEATURE [Part::MultiFuse] Fusion119
  Placement = pos=(9.6,23,0) rot=(0,0,1;3.14159rad)
  Shapes = -> [Cut049,Cut050]
FEATURE [Part::Box] Box031  label="Cube018"
  AttacherType = Attacher::AttachEngine3D
  Height = 10
  Length = 3
  Placement = pos=(3.3,4,12) rot=(0,0,1;0rad)
  Width = 10
FEATURE [Part::Fillet] Fillet044
  Base = -> Box031
  Edges = 1 edges r=2: [Edge11]
FEATURE [Part::Box] Box032  label="Cube019"
  AttacherType = Attacher::AttachEngine3D
  Height = 10
  Length = 3
  Placement = pos=(3.3,4,50) rot=(0,0,1;0rad)
  Width = 10
FEATURE [Part::Fillet] Fillet045
  Base = -> Box032
  Edges = 1 edges r=2: [Edge12]
FEATURE [Part::Box] Box033  label="Cube020"
  AttacherType = Attacher::AttachEngine3D
  Height = 28
  Length = 4
  Placement = pos=(5,0,22) rot=(0,0,1;0rad)
  Width = 10
FEATURE [Part::Fillet] Fillet046
  Base = -> Box033
  Edges = 1 edges r=1: [Edge7]
FEATURE [Part::Fillet] Fillet047
  Base = -> Fillet046
  Edges = 1 edges r=2: [Edge5]
FEATURE [Part::Fillet] Fillet048
  Base = -> Fillet047
  Edges = 1 edges r=2: [Edge2]
FEATURE [Part::Cylinder] Cylinder050
  Angle = 360
  AttacherType = Attacher::AttachEngine3D
  Height = 20
  Placement = pos=(0,0,36.15) rot=(0,0,1;0rad)
  Radius = 8.2
FEATURE [Part::Cylinder] Cylinder051
  Angle = 360
  AttacherType = Attacher::AttachEngine3D
  Height = 10
  Placement = pos=(0,0,36.15) rot=(0,0,1;0rad)
  Radius = 4
FEATURE [Part::MultiFuse] Fusion120  label="removeToCreteHoleForPlugHousing043"
  Placement = pos=(-42,19,36) rot=(0,1,0;1.5708rad)
  Shapes = -> [Cylinder050,Cylinder051]
FEATURE [Sketcher::SketchObject] Sketch067  label="topSketch018"
  FullyConstrained = true
  sketch-geometry (4):
    g0: LineSegment StartX=16.8446 StartY=31.512 StartZ=0 EndX=16.3251 EndY=34.4666 EndZ=0
    g1: ArcOfCircle CenterX=19 CenterY=19.2524 CenterZ=0 NormalX=0 NormalY=0 NormalZ=1 AngleXU=0 Radius=15.4476 StartAngle=1.74483 EndAngle=2.72717
    g2: ArcOfCircle CenterX=19 CenterY=19.2524 CenterZ=0 NormalX=0 NormalY=0 NormalZ=1 AngleXU=0 Radius=12.4476 StartAngle=1.74483 EndAngle=2.73189
    g3: LineSegment StartX=4.86004 StartY=25.4725 StartZ=0 EndX=7.58253 EndY=24.2107 EndZ=0
  constraints (7):
    c: Block(g0)
    c: Coincident(g1,g0)
    c: Coincident(g2,g0)
    c: Coincident(g3,g1)
    c: Coincident(g3,g2)
    c: Block(g1)
    c: Block(g2)
FEATURE [Part::Extrusion] Extrude058
  Base = -> Sketch067
  Dir = (0,0,1)
  DirMode = 2
  FaceMakerClass = Part::FaceMakerBullseye
  LengthFwd = 10
  LengthRev = 0
  Placement = pos=(0,0,31) rot=(0,0,1;0rad)
  Solid = true
  Symmetric = false
FEATURE [Part::Cut] Cut051
  Base = -> Extrude058
  Tool = -> Fusion120
FEATURE [Part::Fillet] Fillet049
  Base = -> Cut051
  Edges = 1 edges r=2: [Edge1]
FEATURE [Part::Fillet] Fillet050
  Base = -> Fillet049
  Edges = 1 edges r=2.5: [Edge1]
FEATURE [Part::Fillet] Fillet051
  Base = -> Fillet050
  Edges = 1 edges r=2.5: [Edge2]
FEATURE [Part::MultiFuse] Fusion121  label="wireHolder003"
  Shapes = -> [Fusion116,Fillet051]
FEATURE [Part::MultiFuse] Fusion122
  Shapes = -> [Fillet045,Fusion121]
FEATURE [Part::MultiFuse] Fusion123  label="wireHolder004"
  Shapes = -> [Fusion122,Fillet048]
FEATURE [Part::MultiFuse] Fusion124  label="wireHolder005"
  Shapes = -> [Fillet044,Fusion119,Fusion123]
FEATURE [Part::MultiFuse] Fusion126  label="casePillars005"
  Shapes = -> [Fusion092,Cut047]
FEATURE [Sketcher::SketchObject] Sketch068  label="topSketch019"
  FullyConstrained = true
  sketch-geometry (6):
    g0: LineSegment StartX=19 StartY=38 StartZ=0 EndX=117 EndY=38 EndZ=0
    g1: ArcOfCircle CenterX=19 CenterY=19 CenterZ=0 NormalX=0 NormalY=0 NormalZ=1 AngleXU=0 Radius=19 StartAngle=1.5708 EndAngle=3.14159
    g2: LineSegment StartX=117 StartY=38 StartZ=0 EndX=117 EndY=19 EndZ=0
    g3: LineSegment StartX=98 StartY=1.0161e-12 StartZ=0 EndX=5.22862e-06 EndY=1.0161e-12 EndZ=0
    g4: LineSegment StartX=5.22862e-06 StartY=19 StartZ=0 EndX=5.22862e-06 EndY=1.0161e-12 EndZ=0
    g5: ArcOfCircle CenterX=98 CenterY=19 CenterZ=0 NormalX=0 NormalY=0 NormalZ=1 AngleXU=0 Radius=19 StartAngle=4.71239 EndAngle=6.28319
  constraints (16):
    c: Horizontal(g0)
    c: Distance(g0) = 98
    c: Coincident(g1,g0)
    c: Block(g1)
    c: Coincident(g2,g0)
    c: Vertical(g2)
    c: Distance(g2) = 19
    c: Horizontal(g3)
    c: Coincident(g4,g1)
    c: Vertical(g4)
    c: Coincident(g3,g4)
    c: Block(g3)
    c: Coincident(g5,g2)
    c: Coincident(g5,g3)
    c: Block(g0)
    c: Block(g5)
FEATURE [Part::Extrusion] Extrude059  label="sideA002"
  Base = -> Sketch068
  Dir = (0,0,1)
  DirMode = 2
  FaceMakerClass = Part::FaceMakerBullseye
  LengthFwd = 3
  LengthRev = 0
  Placement = pos=(0,0,-2.7) rot=(0,0,1;0rad)
  Solid = true
  Symmetric = false
FEATURE [Sketcher::SketchObject] Sketch069  label="topSketch020"
  FullyConstrained = true
  sketch-geometry (6):
    g0: LineSegment StartX=19 StartY=38 StartZ=0 EndX=117 EndY=38 EndZ=0
    g1: ArcOfCircle CenterX=19 CenterY=19 CenterZ=0 NormalX=0 NormalY=0 NormalZ=1 AngleXU=0 Radius=19 StartAngle=1.5708 EndAngle=3.14159
    g2: LineSegment StartX=117 StartY=38 StartZ=0 EndX=117 EndY=19 EndZ=0
    g3: LineSegment StartX=98 StartY=1.0161e-12 StartZ=0 EndX=5.22862e-06 EndY=1.0161e-12 EndZ=0
    g4: LineSegment StartX=5.22862e-06 StartY=19 StartZ=0 EndX=5.22862e-06 EndY=1.0161e-12 EndZ=0
    g5: ArcOfCircle CenterX=98 CenterY=19 CenterZ=0 NormalX=0 NormalY=0 NormalZ=1 AngleXU=0 Radius=19 StartAngle=4.71239 EndAngle=6.28319
  constraints (16):
    c: Horizontal(g0)
    c: Distance(g0) = 98
    c: Coincident(g1,g0)
    c: Block(g1)
    c: Coincident(g2,g0)
    c: Vertical(g2)
    c: Distance(g2) = 19
    c: Horizontal(g3)
    c: Coincident(g4,g1)
    c: Vertical(g4)
    c: Coincident(g3,g4)
    c: Block(g3)
    c: Coincident(g5,g2)
    c: Coincident(g5,g3)
    c: Block(g0)
    c: Block(g5)
FEATURE [Part::Extrusion] Extrude060  label="sideB002"
  Base = -> Sketch069
  Dir = (0,0,1)
  DirMode = 2
  FaceMakerClass = Part::FaceMakerBullseye
  LengthFwd = 3
  LengthRev = 0
  Placement = pos=(0,0,71.7) rot=(0,0,1;0rad)
  Solid = true
  Symmetric = false
FEATURE [Part::MultiFuse] Fusion127  label="removeFromBottom001"
  Placement = pos=(2,0,0) rot=(0,0,1;0rad)
  Shapes = -> [Extrude059,Extrude060]
FEATURE [Part::Cylinder] Cylinder052
  Angle = 360
  AttacherType = Attacher::AttachEngine3D
  Height = 20
  Placement = pos=(0,0,36.15) rot=(0,0,1;0rad)
  Radius = 14
FEATURE [Part::Cylinder] Cylinder053
  Angle = 360
  AttacherType = Attacher::AttachEngine3D
  Height = 10
  Placement = pos=(0,0,36.15) rot=(0,0,1;0rad)
  Radius = 4
FEATURE [Part::MultiFuse] Fusion128  label="removeToCreteHoleForPlugHousing044"
  Placement = pos=(70,19,36) rot=(0,1,0;1.5708rad)
  Shapes = -> [Cylinder052,Cylinder053]
FEATURE [Part::Cut] Cut052  label="bottom011"
  Base = -> Extrude043
  Tool = -> Fusion128
FEATURE [Part::MultiFuse] Fusion129  label="screwRetainersAndInsertHolders"
  Shapes = -> [Fusion095,Fusion096]
FEATURE [Part::Cut] Cut053  label="screwRetainersAndInsertHolders001"
  Base = -> Fusion129
  Tool = -> Fusion127
FEATURE [Part::Cut] Cut054  label="bottom012"
  Base = -> Cut052
  Tool = -> Fusion115
FEATURE [Sketcher::SketchObject] Sketch070
  FullyConstrained = true
  Placement = pos=(117,19,0) rot=(0.57735,0.57735,0.57735;2.0944rad)
  sketch-geometry (48):
    g0: LineSegment StartX=-49.19 StartY=69.25 StartZ=0 EndX=-49.19 EndY=66.25 EndZ=0
    g1: LineSegment StartX=-49.19 StartY=63.5 StartZ=0 EndX=-49.19 EndY=60.5 EndZ=0
    g2: LineSegment StartX=-49.19 StartY=57.75 StartZ=0 EndX=-49.19 EndY=54.75 EndZ=0
    g3: LineSegment StartX=-49.19 StartY=52 StartZ=0 EndX=-49.19 EndY=49 EndZ=0
    g4: LineSegment StartX=-49.19 StartY=46.25 StartZ=0 EndX=-49.19 EndY=43.25 EndZ=0
    g5: LineSegment StartX=-49.19 StartY=40.5 StartZ=0 EndX=-49.19 EndY=37.5 EndZ=0
    g6: LineSegment StartX=-49.19 StartY=34.5 StartZ=0 EndX=-49.19 EndY=31.5 EndZ=0
    g7: LineSegment StartX=-49.19 StartY=28.75 StartZ=0 EndX=-49.19 EndY=25.75 EndZ=0
    g8: LineSegment StartX=-49.19 StartY=23 StartZ=0 EndX=-49.19 EndY=20 EndZ=0
    g9: LineSegment StartX=-49.19 StartY=17.25 StartZ=0 EndX=-49.19 EndY=14.25 EndZ=0
    g10: LineSegment StartX=-49.19 StartY=11.5 StartZ=0 EndX=-49.19 EndY=8.5 EndZ=0
    g11: LineSegment StartX=-49.19 StartY=5.75 StartZ=0 EndX=-49.19 EndY=2.75 EndZ=0
    g12: ArcOfCircle CenterX=-1.5 CenterY=67.75 CenterZ=0 NormalX=0 NormalY=0 NormalZ=1 AngleXU=0 Radius=1.5 StartAngle=4.71239 EndAngle=7.85398
    g13: ArcOfCircle CenterX=-1.5 CenterY=62 CenterZ=0 NormalX=0 NormalY=0 NormalZ=1 AngleXU=0 Radius=1.5 StartAngle=4.71239 EndAngle=7.85398
    g14: ArcOfCircle CenterX=-1.5 CenterY=56.25 CenterZ=0 NormalX=0 NormalY=0 NormalZ=1 AngleXU=0 Radius=1.5 StartAngle=4.71239 EndAngle=7.85398
    g15: ArcOfCircle CenterX=-11.49 CenterY=50.5 CenterZ=0 NormalX=0 NormalY=0 NormalZ=1 AngleXU=0 Radius=1.5 StartAngle=4.71239 EndAngle=7.85398
    g16: ArcOfCircle CenterX=-16.28 CenterY=44.75 CenterZ=0 NormalX=0 NormalY=0 NormalZ=1 AngleXU=0 Radius=1.5 StartAngle=4.71239 EndAngle=7.85398
    g17: ArcOfCircle CenterX=-18.2337 CenterY=39 CenterZ=0 NormalX=0 NormalY=0 NormalZ=1 AngleXU=0 Radius=1.5 StartAngle=4.71485 EndAngle=7.85398
    g18: ArcOfCircle CenterX=-16.2837 CenterY=27.25 CenterZ=0 NormalX=0 NormalY=0 NormalZ=1 AngleXU=0 Radius=1.5 StartAngle=4.71485 EndAngle=7.85398
    g19: ArcOfCircle CenterX=-18.2337 CenterY=33 CenterZ=0 NormalX=0 NormalY=0 NormalZ=1 AngleXU=0 Radius=1.5 StartAngle=4.71485 EndAngle=7.85398
    g20: ArcOfCircle CenterX=-11.49 CenterY=21.5 CenterZ=0 NormalX=0 NormalY=0 NormalZ=1 AngleXU=0 Radius=1.5 StartAngle=4.71239 EndAngle=7.85398
    g21: ArcOfCircle CenterX=-1.5 CenterY=4.25 CenterZ=0 NormalX=0 NormalY=0 NormalZ=1 AngleXU=0 Radius=1.5 StartAngle=4.71239 EndAngle=7.85398
    g22: ArcOfCircle CenterX=-1.5 CenterY=10 CenterZ=0 NormalX=0 NormalY=0 NormalZ=1 AngleXU=0 Radius=1.5 StartAngle=4.71239 EndAngle=7.85398
    g23: ArcOfCircle CenterX=-1.5 CenterY=15.75 CenterZ=0 NormalX=0 NormalY=0 NormalZ=1 AngleXU=0 Radius=1.5 StartAngle=4.71239 EndAngle=7.85398
    g24: LineSegment StartX=-49.19 StartY=69.25 StartZ=0 EndX=-1.5 EndY=69.25 EndZ=0
    g25: LineSegment StartX=-49.19 StartY=66.25 StartZ=0 EndX=-1.5 EndY=66.25 EndZ=0
    g26: LineSegment StartX=-49.19 StartY=63.5 StartZ=0 EndX=-1.5 EndY=63.5 EndZ=0
    g27: LineSegment StartX=-49.19 StartY=60.5 StartZ=0 EndX=-1.5 EndY=60.5 EndZ=0
    g28: LineSegment StartX=-49.19 StartY=57.75 StartZ=0 EndX=-1.5 EndY=57.75 EndZ=0
    g29: LineSegment StartX=-49.19 StartY=54.75 StartZ=0 EndX=-1.5 EndY=54.75 EndZ=0
    g30: LineSegment StartX=-49.19 StartY=52 StartZ=0 EndX=-11.49 EndY=52 EndZ=0
    g31: LineSegment StartX=-49.19 StartY=49 StartZ=0 EndX=-11.49 EndY=49 EndZ=0
    g32: LineSegment StartX=-49.19 StartY=46.25 StartZ=0 EndX=-16.28 EndY=46.25 EndZ=0
    g33: LineSegment StartX=-49.19 StartY=43.25 StartZ=0 EndX=-16.28 EndY=43.25 EndZ=0
    g34: LineSegment StartX=-49.19 StartY=40.5 StartZ=0 EndX=-18.2337 EndY=40.5 EndZ=0
    g35: LineSegment StartX=-49.19 StartY=37.5 StartZ=0 EndX=-18.23 EndY=37.5 EndZ=0
    g36: LineSegment StartX=-49.19 StartY=34.5 StartZ=0 EndX=-18.2337 EndY=34.5 EndZ=0
    g37: LineSegment StartX=-49.19 StartY=31.5 StartZ=0 EndX=-18.23 EndY=31.5 EndZ=0
    g38: LineSegment StartX=-49.19 StartY=28.75 StartZ=0 EndX=-16.2837 EndY=28.75 EndZ=0
    g39: LineSegment StartX=-49.19 StartY=25.75 StartZ=0 EndX=-16.28 EndY=25.75 EndZ=0
    g40: LineSegment StartX=-49.19 StartY=23 StartZ=0 EndX=-11.49 EndY=23 EndZ=0
    g41: LineSegment StartX=-49.19 StartY=20 StartZ=0 EndX=-11.49 EndY=20 EndZ=0
    g42: LineSegment StartX=-49.19 StartY=17.25 StartZ=0 EndX=-1.5 EndY=17.25 EndZ=0
    g43: LineSegment StartX=-49.19 StartY=14.25 StartZ=0 EndX=-1.5 EndY=14.25 EndZ=0
    g44: LineSegment StartX=-49.19 StartY=11.5 StartZ=0 EndX=-1.5 EndY=11.5 EndZ=0
    g45: LineSegment StartX=-49.19 StartY=8.5 StartZ=0 EndX=-1.5 EndY=8.5 EndZ=0
    g46: LineSegment StartX=-49.19 StartY=5.75 StartZ=0 EndX=-1.5 EndY=5.75 EndZ=0
    g47: LineSegment StartX=-49.19 StartY=2.75 StartZ=0 EndX=-1.5 EndY=2.75 EndZ=0
  constraints (120):
    c: Vertical(g0)
    c: Distance(g0) = 3
    c: Block(g0)
    c: Vertical(g1)
    c: Distance(g1) = 3
    c: Vertical(g2)
    c: Equal(g0,g2) = 3
    c: Block(g2)
    c: Vertical(g3)
    c: Equal(g1,g3) = 3
    c: Vertical(g4)
    c: Equal(g0,g4) = 3
    c: Block(g4)
    c: Vertical(g5)
    c: Equal(g1,g5) = 3
    c: Vertical(g6)
    c: Equal(g0,g6) = 3
    c: Block(g6)
    c: Vertical(g7)
    c: Equal(g1,g7) = 3
    c: Vertical(g8)
    c: Equal(g0,g8) = 3
    c: Block(g8)
    c: Vertical(g9)
    c: Equal(g1,g9) = 3
    c: Vertical(g10)
    c: Equal(g0,g10) = 3
    c: Block(g10)
    c: Vertical(g11)
    c: Equal(g1,g11) = 3
    c: Block(g12)
    c: Block(g13)
    c: Block(g14)
    c: Block(g15)
    c: Block(g16)
    c: Block(g17)
    c: Block(g18)
    c: Block(g19)
    c: Block(g20)
    c: Block(g21)
    c: Block(g22)
    c: Block(g23)
    c: Block(g11)
    c: Block(g9)
    c: Block(g7)
    c: Block(g5)
    c: Block(g3)
    c: Block(g1)
    c: Coincident(g24,g0)
    c: Coincident(g24,g12)
    c: Horizontal(g24)
    c: Coincident(g25,g0)
    c: Coincident(g25,g12)
    c: Horizontal(g25)
    c: Coincident(g26,g1)
    c: Coincident(g26,g13)
    c: Horizontal(g26)
    c: Coincident(g27,g1)
    c: Coincident(g27,g13)
    c: Horizontal(g27)
    c: Coincident(g28,g2)
    c: Coincident(g28,g14)
    c: Horizontal(g28)
    c: Coincident(g29,g2)
    c: Coincident(g29,g14)
    c: Horizontal(g29)
    c: Coincident(g30,g3)
    c: Coincident(g30,g15)
    c: Horizontal(g30)
    c: Coincident(g31,g3)
    c: Coincident(g31,g15)
    c: Horizontal(g31)
    c: Coincident(g32,g4)
    c: Coincident(g32,g16)
    c: Horizontal(g32)
    c: Coincident(g33,g4)
    c: Coincident(g33,g16)
    c: Horizontal(g33)
    c: Coincident(g34,g5)
    c: Coincident(g34,g17)
    c: Horizontal(g34)
    c: Coincident(g35,g5)
    c: Coincident(g35,g17)
    c: Horizontal(g35)
    c: Coincident(g36,g6)
    c: Coincident(g36,g19)
    c: Horizontal(g36)
    c: Coincident(g37,g6)
    c: Coincident(g37,g19)
    c: Horizontal(g37)
    c: Coincident(g38,g7)
    c: Coincident(g38,g18)
    c: Horizontal(g38)
    c: Coincident(g39,g7)
    c: Coincident(g39,g18)
    c: Horizontal(g39)
    c: Coincident(g40,g8)
    c: Coincident(g40,g20)
    c: Horizontal(g40)
    c: Coincident(g41,g8)
    c: Coincident(g41,g20)
    c: Horizontal(g41)
    c: Coincident(g42,g9)
    c: Coincident(g42,g23)
    c: Horizontal(g42)
    c: Coincident(g43,g9)
    c: Coincident(g43,g23)
    c: Horizontal(g43)
    c: Coincident(g44,g10)
    c: Coincident(g44,g22)
    c: Horizontal(g44)
    c: Coincident(g45,g10)
    c: Coincident(g45,g22)
    c: Horizontal(g45)
    c: Coincident(g46,g11)
    c: Coincident(g46,g21)
    c: Horizontal(g46)
    c: Coincident(g47,g11)
    c: Coincident(g47,g21)
    c: Horizontal(g47)
FEATURE [Part::Extrusion] Extrude061
  Base = -> Sketch070
  Dir = (1,0,0)
  DirMode = 2
  FaceMakerClass = Part::FaceMakerBullseye
  LengthFwd = 23
  LengthRev = 0
  Placement = pos=(-19,0,0) rot=(0,0,1;0rad)
  Solid = true
  Symmetric = false
FEATURE [Part::Fillet] Fillet052  label="removeToCreateVentalationHoles002"
  Base = -> Extrude061
  Edges = <same value as first occurrence — deduplicated (x5 in doc)>
  Placement = pos=(7,0,0) rot=(0,0,1;0rad)
FEATURE [Part::MultiFuse] Fusion130  label="bottom013"
  Shapes = -> [Cut054,Cut034]
